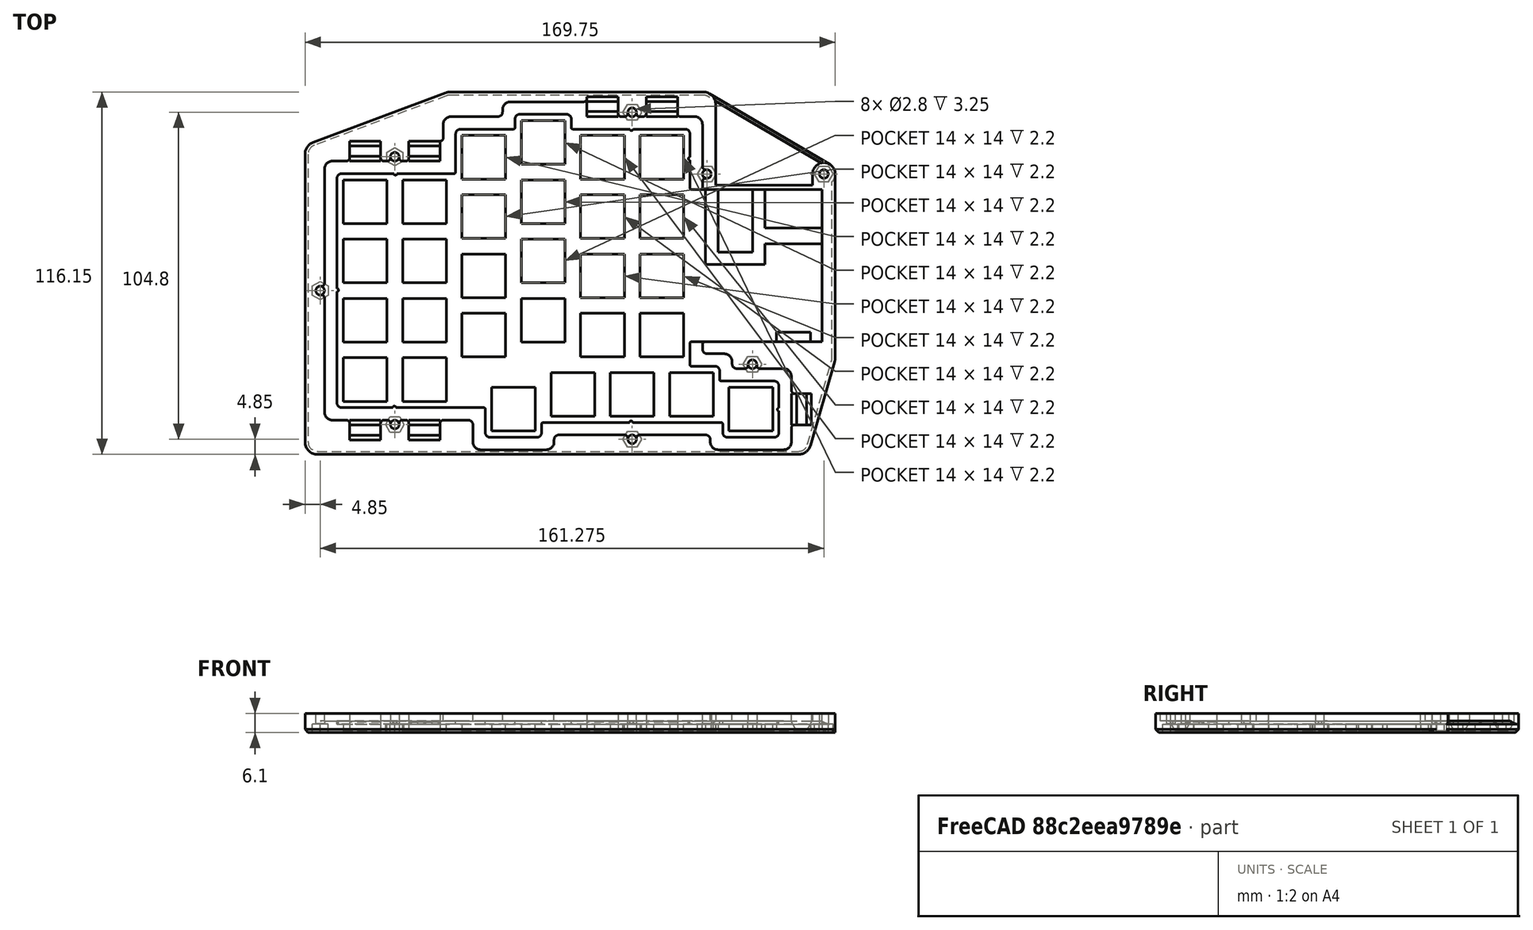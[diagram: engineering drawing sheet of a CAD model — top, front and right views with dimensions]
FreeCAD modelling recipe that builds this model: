
FCSTD DOCUMENT  (FreeCAD 0.21R33771 (Git))
Label: bottom
License: All rights reserved
LicenseURL: http://en.wikipedia.org/wiki/All_rights_reserved
objects: Sketcher::SketchObject×34, PartDesign::Pocket×21, PartDesign::Pad×14, PartDesign::Fillet×11, PartDesign::SubtractivePipe×5, PartDesign::Chamfer×4, PartDesign::Plane×3, Spreadsheet::Sheet×1, PartDesign::Body×1
note: 148 computed .brp shape members not serialized (recipe doc carries the construction recipe); baked Part::Feature solids carry a one-line shape summary decoded from their .brp

FEATURE [Sketcher::SketchObject] Sketch
  FullyConstrained = true
  MapMode = 5
  Support = -> [XY_Plane]
  expr: Constraints[10] = Spreadsheet.sw_wi
  expr: Constraints[11] = Spreadsheet.sw_he
  expr: Constraints[23] = Spreadsheet.pl_spacing
  expr: Constraints[343] = Spreadsheet.pl_spacing
  expr: Constraints[344] = Spreadsheet.pl_spacing
  expr: Constraints[345] = Spreadsheet.pl_spacing
  expr: Constraints[346] = Spreadsheet.pl_spacing
  expr: Constraints[347] = Spreadsheet.pl_spacing
  expr: Constraints[348] = Spreadsheet.pl_sp4
  expr: Constraints[349] = Spreadsheet.pl_sp4
  expr: Constraints[350] = Spreadsheet.pl_sp2
  expr: Constraints[351] = Spreadsheet.pl_spacing
  expr: Constraints[352] = Spreadsheet.pl_spacing
  expr: Constraints[353] = Spreadsheet.pl_spacing
  expr: Constraints[354] = Spreadsheet.pl_spacing
  expr: Constraints[355] = Spreadsheet.pl_spacing
  expr: Constraints[356] = Spreadsheet.pl_spacing
  expr: Constraints[357] = Spreadsheet.pl_spacing
  expr: Constraints[358] = Spreadsheet.pl_spacing
  expr: Constraints[359] = Spreadsheet.pl_spacing
  expr: Constraints[360] = Spreadsheet.pl_spacing
  expr: Constraints[361] = Spreadsheet.pl_spacing
  expr: Constraints[362] = Spreadsheet.pl_spacing
  expr: Constraints[363] = Spreadsheet.pl_spacing
  expr: Constraints[364] = Spreadsheet.pl_spacing
  expr: Constraints[365] = Spreadsheet.pl_spacing
  expr: Constraints[366] = Spreadsheet.pl_spacing
  expr: Constraints[367] = Spreadsheet.pl_spacing
  expr: Constraints[368] = Spreadsheet.pl_spacing
  expr: Constraints[369] = Spreadsheet.pl_spacing
  expr: Constraints[370] = Spreadsheet.pl_spacing
  expr: Constraints[373] = Spreadsheet.pl_sp4
  expr: Constraints[375] = Spreadsheet.pl_sp4
  expr: Constraints[379] = Spreadsheet.pl_case_ext
  expr: Constraints[37] = Spreadsheet.pl_spacing
  expr: Constraints[380] = Spreadsheet.pl_case
  expr: Constraints[381] = Spreadsheet.pl_case
  expr: Constraints[50] = Spreadsheet.pl_spacing
  sketch-geometry (149):
    g0: LineSegment StartX=-7 StartY=7 StartZ=0 EndX=-7 EndY=-7 EndZ=0
    g1: LineSegment StartX=-7 StartY=-7 StartZ=0 EndX=7 EndY=-7 EndZ=0
    g2: LineSegment StartX=7 StartY=-7 StartZ=0 EndX=7 EndY=7 EndZ=0
    g3: LineSegment StartX=7 StartY=7 StartZ=0 EndX=-7 EndY=7 EndZ=0
    g4: GeomPoint X=0 Y=0 Z=0
    g5: LineSegment StartX=-7 StartY=-12 StartZ=0 EndX=-7 EndY=-26 EndZ=0
    g6: LineSegment StartX=-7 StartY=-26 StartZ=0 EndX=7 EndY=-26 EndZ=0
    g7: LineSegment StartX=7 StartY=-26 StartZ=0 EndX=7 EndY=-12 EndZ=0
    g8: LineSegment StartX=7 StartY=-12 StartZ=0 EndX=-7 EndY=-12 EndZ=0
    g9: GeomPoint X=0 Y=-19 Z=0
    g10: LineSegment StartX=-7 StartY=26 StartZ=0 EndX=-7 EndY=12 EndZ=0
    g11: LineSegment StartX=-7 StartY=12 StartZ=0 EndX=7 EndY=12 EndZ=0
    g12: LineSegment StartX=7 StartY=12 StartZ=0 EndX=7 EndY=26 EndZ=0
    g13: LineSegment StartX=7 StartY=26 StartZ=0 EndX=-7 EndY=26 EndZ=0
    g14: GeomPoint X=0 Y=19 Z=0
    g15: LineSegment StartX=-7 StartY=45 StartZ=0 EndX=-7 EndY=31 EndZ=0
    g16: LineSegment StartX=-7 StartY=31 StartZ=0 EndX=7 EndY=31 EndZ=0
    g17: LineSegment StartX=7 StartY=31 StartZ=0 EndX=7 EndY=45 EndZ=0
    g18: LineSegment StartX=7 StartY=45 StartZ=0 EndX=-7 EndY=45 EndZ=0
    g19: GeomPoint X=0 Y=38 Z=0
    g20: LineSegment StartX=-26 StartY=45 StartZ=0 EndX=-26 EndY=31 EndZ=0
    g21: LineSegment StartX=-26 StartY=31 StartZ=0 EndX=-12 EndY=31 EndZ=0
    g22: LineSegment StartX=-12 StartY=31 StartZ=0 EndX=-12 EndY=45 EndZ=0
    g23: LineSegment StartX=-12 StartY=45 StartZ=0 EndX=-26 EndY=45 EndZ=0
    g24: GeomPoint X=-19 Y=38 Z=0
    g25: LineSegment StartX=-26 StartY=26 StartZ=0 EndX=-26 EndY=12 EndZ=0
    g26: LineSegment StartX=-26 StartY=12 StartZ=0 EndX=-12 EndY=12 EndZ=0
    g27: LineSegment StartX=-12 StartY=12 StartZ=0 EndX=-12 EndY=26 EndZ=0
    g28: LineSegment StartX=-12 StartY=26 StartZ=0 EndX=-26 EndY=26 EndZ=0
    g29: GeomPoint X=-19 Y=19 Z=0
    g30: LineSegment StartX=-26 StartY=7 StartZ=0 EndX=-26 EndY=-7 EndZ=0
    g31: LineSegment StartX=-26 StartY=-7 StartZ=0 EndX=-12 EndY=-7 EndZ=0
    g32: LineSegment StartX=-12 StartY=-7 StartZ=0 EndX=-12 EndY=7 EndZ=0
    g33: LineSegment StartX=-12 StartY=7 StartZ=0 EndX=-26 EndY=7 EndZ=0
    g34: GeomPoint X=-19 Y=0 Z=0
    g35: LineSegment StartX=-26 StartY=-12 StartZ=0 EndX=-26 EndY=-26 EndZ=0
    g36: LineSegment StartX=-26 StartY=-26 StartZ=0 EndX=-12 EndY=-26 EndZ=0
    g37: LineSegment StartX=-12 StartY=-26 StartZ=0 EndX=-12 EndY=-12 EndZ=0
    g38: LineSegment StartX=-12 StartY=-12 StartZ=0 EndX=-26 EndY=-12 EndZ=0
    g39: GeomPoint X=-19 Y=-19 Z=0
    g40: LineSegment StartX=-45 StartY=49.75 StartZ=0 EndX=-45 EndY=35.75 EndZ=0
    g41: LineSegment StartX=-45 StartY=35.75 StartZ=0 EndX=-31 EndY=35.75 EndZ=0
    g42: LineSegment StartX=-31 StartY=35.75 StartZ=0 EndX=-31 EndY=49.75 EndZ=0
    g43: LineSegment StartX=-31 StartY=49.75 StartZ=0 EndX=-45 EndY=49.75 EndZ=0
    g44: GeomPoint X=-38 Y=42.75 Z=0
    g45: LineSegment StartX=-45 StartY=30.75 StartZ=0 EndX=-45 EndY=16.75 EndZ=0
    g46: LineSegment StartX=-45 StartY=16.75 StartZ=0 EndX=-31 EndY=16.75 EndZ=0
    g47: LineSegment StartX=-31 StartY=16.75 StartZ=0 EndX=-31 EndY=30.75 EndZ=0
    g48: LineSegment StartX=-31 StartY=30.75 StartZ=0 EndX=-45 EndY=30.75 EndZ=0
    g49: GeomPoint X=-38 Y=23.75 Z=0
    g50: LineSegment StartX=-45 StartY=11.75 StartZ=0 EndX=-45 EndY=-2.25 EndZ=0
    g51: LineSegment StartX=-45 StartY=-2.25 StartZ=0 EndX=-31 EndY=-2.25 EndZ=0
    g52: LineSegment StartX=-31 StartY=-2.25 StartZ=0 EndX=-31 EndY=11.75 EndZ=0
    g53: LineSegment StartX=-31 StartY=11.75 StartZ=0 EndX=-45 EndY=11.75 EndZ=0
    g54: GeomPoint X=-38 Y=4.75 Z=0
    g55: LineSegment StartX=-45 StartY=-7.25 StartZ=0 EndX=-45 EndY=-21.25 EndZ=0
    g56: LineSegment StartX=-45 StartY=-21.25 StartZ=0 EndX=-31 EndY=-21.25 EndZ=0
    g57: LineSegment StartX=-31 StartY=-21.25 StartZ=0 EndX=-31 EndY=-7.25 EndZ=0
    g58: LineSegment StartX=-31 StartY=-7.25 StartZ=0 EndX=-45 EndY=-7.25 EndZ=0
    g59: GeomPoint X=-38 Y=-14.25 Z=0
    g60: LineSegment StartX=-64 StartY=45 StartZ=0 EndX=-64 EndY=31 EndZ=0
    g61: LineSegment StartX=-64 StartY=31 StartZ=0 EndX=-50 EndY=31 EndZ=0
    g62: LineSegment StartX=-50 StartY=31 StartZ=0 EndX=-50 EndY=45 EndZ=0
    g63: LineSegment StartX=-50 StartY=45 StartZ=0 EndX=-64 EndY=45 EndZ=0
    g64: GeomPoint X=-57 Y=38 Z=0
    g65: LineSegment StartX=-64 StartY=26 StartZ=0 EndX=-64 EndY=12 EndZ=0
    g66: LineSegment StartX=-64 StartY=12 StartZ=0 EndX=-50 EndY=12 EndZ=0
    g67: LineSegment StartX=-50 StartY=12 StartZ=0 EndX=-50 EndY=26 EndZ=0
    g68: LineSegment StartX=-50 StartY=26 StartZ=0 EndX=-64 EndY=26 EndZ=0
    g69: GeomPoint X=-57 Y=19 Z=0
    g70: LineSegment StartX=-64 StartY=7 StartZ=0 EndX=-64 EndY=-7 EndZ=0
    g71: LineSegment StartX=-64 StartY=-7 StartZ=0 EndX=-50 EndY=-7 EndZ=0
    g72: LineSegment StartX=-50 StartY=-7 StartZ=0 EndX=-50 EndY=7 EndZ=0
    g73: LineSegment StartX=-50 StartY=7 StartZ=0 EndX=-64 EndY=7 EndZ=0
    g74: GeomPoint X=-57 Y=0 Z=0
    g75: LineSegment StartX=-64 StartY=-12 StartZ=0 EndX=-64 EndY=-26 EndZ=0
    g76: LineSegment StartX=-64 StartY=-26 StartZ=0 EndX=-50 EndY=-26 EndZ=0
    g77: LineSegment StartX=-50 StartY=-26 StartZ=0 EndX=-50 EndY=-12 EndZ=0
    g78: LineSegment StartX=-50 StartY=-12 StartZ=0 EndX=-64 EndY=-12 EndZ=0
    g79: GeomPoint X=-57 Y=-19 Z=0
    g80: LineSegment StartX=-83 StartY=30.75 StartZ=0 EndX=-83 EndY=16.75 EndZ=0
    g81: LineSegment StartX=-83 StartY=16.75 StartZ=0 EndX=-69 EndY=16.75 EndZ=0
    g82: LineSegment StartX=-69 StartY=16.75 StartZ=0 EndX=-69 EndY=30.75 EndZ=0
    g83: LineSegment StartX=-69 StartY=30.75 StartZ=0 EndX=-83 EndY=30.75 EndZ=0
    g84: GeomPoint X=-76 Y=23.75 Z=0
    g85: LineSegment StartX=-102 StartY=30.75 StartZ=0 EndX=-102 EndY=16.75 EndZ=0
    g86: LineSegment StartX=-102 StartY=16.75 StartZ=0 EndX=-88 EndY=16.75 EndZ=0
    g87: LineSegment StartX=-88 StartY=16.75 StartZ=0 EndX=-88 EndY=30.75 EndZ=0
    g88: LineSegment StartX=-88 StartY=30.75 StartZ=0 EndX=-102 EndY=30.75 EndZ=0
    g89: GeomPoint X=-95 Y=23.75 Z=0
    g90: LineSegment StartX=-83 StartY=11.75 StartZ=0 EndX=-83 EndY=-2.25 EndZ=0
    g91: LineSegment StartX=-83 StartY=-2.25 StartZ=0 EndX=-69 EndY=-2.25 EndZ=0
    g92: LineSegment StartX=-69 StartY=-2.25 StartZ=0 EndX=-69 EndY=11.75 EndZ=0
    g93: LineSegment StartX=-69 StartY=11.75 StartZ=0 EndX=-83 EndY=11.75 EndZ=0
    g94: GeomPoint X=-76 Y=4.75 Z=0
    g95: LineSegment StartX=-83 StartY=-7.25 StartZ=0 EndX=-83 EndY=-21.25 EndZ=0
    g96: LineSegment StartX=-83 StartY=-21.25 StartZ=0 EndX=-69 EndY=-21.25 EndZ=0
    g97: LineSegment StartX=-69 StartY=-21.25 StartZ=0 EndX=-69 EndY=-7.25 EndZ=0
    g98: LineSegment StartX=-69 StartY=-7.25 StartZ=0 EndX=-83 EndY=-7.25 EndZ=0
    g99: GeomPoint X=-76 Y=-14.25 Z=0
    g100: LineSegment StartX=-83 StartY=-26.25 StartZ=0 EndX=-83 EndY=-40.25 EndZ=0
    g101: LineSegment StartX=-83 StartY=-40.25 StartZ=0 EndX=-69 EndY=-40.25 EndZ=0
    g102: LineSegment StartX=-69 StartY=-40.25 StartZ=0 EndX=-69 EndY=-26.25 EndZ=0
    g103: LineSegment StartX=-69 StartY=-26.25 StartZ=0 EndX=-83 EndY=-26.25 EndZ=0
    g104: GeomPoint X=-76 Y=-33.25 Z=0
    g105: LineSegment StartX=-102 StartY=11.75 StartZ=0 EndX=-102 EndY=-2.25 EndZ=0
    g106: LineSegment StartX=-102 StartY=-2.25 StartZ=0 EndX=-88 EndY=-2.25 EndZ=0
    g107: LineSegment StartX=-88 StartY=-2.25 StartZ=0 EndX=-88 EndY=11.75 EndZ=0
    g108: LineSegment StartX=-88 StartY=11.75 StartZ=0 EndX=-102 EndY=11.75 EndZ=0
    g109: GeomPoint X=-95 Y=4.75 Z=0
    g110: LineSegment StartX=-102 StartY=-7.25 StartZ=0 EndX=-102 EndY=-21.25 EndZ=0
    g111: LineSegment StartX=-102 StartY=-21.25 StartZ=0 EndX=-88 EndY=-21.25 EndZ=0
    g112: LineSegment StartX=-88 StartY=-21.25 StartZ=0 EndX=-88 EndY=-7.25 EndZ=0
    g113: LineSegment StartX=-88 StartY=-7.25 StartZ=0 EndX=-102 EndY=-7.25 EndZ=0
    g114: GeomPoint X=-95 Y=-14.25 Z=0
    g115: LineSegment StartX=-102 StartY=-26.25 StartZ=0 EndX=-102 EndY=-40.25 EndZ=0
    g116: LineSegment StartX=-102 StartY=-40.25 StartZ=0 EndX=-88 EndY=-40.25 EndZ=0
    g117: LineSegment StartX=-88 StartY=-40.25 StartZ=0 EndX=-88 EndY=-26.25 EndZ=0
    g118: LineSegment StartX=-88 StartY=-26.25 StartZ=0 EndX=-102 EndY=-26.25 EndZ=0
    g119: GeomPoint X=-95 Y=-33.25 Z=0
    g120: LineSegment StartX=-16.5 StartY=-31 StartZ=0 EndX=-16.5 EndY=-45 EndZ=0
    g121: LineSegment StartX=-16.5 StartY=-45 StartZ=0 EndX=-2.5 EndY=-45 EndZ=0
    g122: LineSegment StartX=-2.5 StartY=-45 StartZ=0 EndX=-2.5 EndY=-31 EndZ=0
    g123: LineSegment StartX=-2.5 StartY=-31 StartZ=0 EndX=-16.5 EndY=-31 EndZ=0
    g124: GeomPoint X=-9.5 Y=-38 Z=0
    g125: LineSegment StartX=2.5 StartY=-31 StartZ=0 EndX=2.5 EndY=-45 EndZ=0
    g126: LineSegment StartX=2.5 StartY=-45 StartZ=0 EndX=16.5 EndY=-45 EndZ=0
    g127: LineSegment StartX=16.5 StartY=-45 StartZ=0 EndX=16.5 EndY=-31 EndZ=0
    g128: LineSegment StartX=16.5 StartY=-31 StartZ=0 EndX=2.5 EndY=-31 EndZ=0
    g129: GeomPoint X=9.5 Y=-38 Z=0
    g130: LineSegment StartX=-35.5 StartY=-31 StartZ=0 EndX=-35.5 EndY=-45 EndZ=0
    g131: LineSegment StartX=-35.5 StartY=-45 StartZ=0 EndX=-21.5 EndY=-45 EndZ=0
    g132: LineSegment StartX=-21.5 StartY=-45 StartZ=0 EndX=-21.5 EndY=-31 EndZ=0
    g133: LineSegment StartX=-21.5 StartY=-31 StartZ=0 EndX=-35.5 EndY=-31 EndZ=0
    g134: GeomPoint X=-28.5 Y=-38 Z=0
    g135: LineSegment StartX=21.5 StartY=-35.75 StartZ=0 EndX=21.5 EndY=-49.75 EndZ=0
    g136: LineSegment StartX=21.5 StartY=-49.75 StartZ=0 EndX=35.5 EndY=-49.75 EndZ=0
    g137: LineSegment StartX=35.5 StartY=-49.75 StartZ=0 EndX=35.5 EndY=-35.75 EndZ=0
    g138: LineSegment StartX=35.5 StartY=-35.75 StartZ=0 EndX=21.5 EndY=-35.75 EndZ=0
    g139: GeomPoint X=28.5 Y=-42.75 Z=0
    g140: LineSegment StartX=-54.5 StartY=-35.75 StartZ=0 EndX=-54.5 EndY=-49.75 EndZ=0
    g141: LineSegment StartX=-54.5 StartY=-49.75 StartZ=0 EndX=-40.5 EndY=-49.75 EndZ=0
    g142: LineSegment StartX=-40.5 StartY=-49.75 StartZ=0 EndX=-40.5 EndY=-35.75 EndZ=0
    g143: LineSegment StartX=-40.5 StartY=-35.75 StartZ=0 EndX=-54.5 EndY=-35.75 EndZ=0
    g144: GeomPoint X=-47.5 Y=-42.75 Z=0
    g145: LineSegment StartX=52.75 StartY=-57.25 StartZ=0 EndX=-114.25 EndY=-57.25 EndZ=0
    g146: LineSegment StartX=-114.25 StartY=-57.25 StartZ=0 EndX=-114.25 EndY=57.25 EndZ=0
    g147: LineSegment StartX=-114.25 StartY=57.25 StartZ=0 EndX=52.75 EndY=57.25 EndZ=0
    g148: LineSegment StartX=52.75 StartY=57.25 StartZ=0 EndX=52.75 EndY=-57.25 EndZ=0
  constraints (388):
    c: Coincident(g0,g1)
    c: Coincident(g1,g2)
    c: Coincident(g2,g3)
    c: Coincident(g3,g0)
    c: Horizontal(g1)
    c: Horizontal(g3)
    c: Vertical(g0)
    c: Vertical(g2)
    c: Symmetric(g1,g0,g4)
    c: Coincident(g4,g-1)
    c: DistanceX(g3,g3) = 14
    c: DistanceY(g0,g0) = 14
    c: Coincident(g5,g6)
    c: Coincident(g6,g7)
    c: Coincident(g7,g8)
    c: Coincident(g8,g5)
    c: Horizontal(g6)
    c: Horizontal(g8)
    c: Vertical(g5)
    c: Vertical(g7)
    c: Symmetric(g6,g5,g9)
    c: Equal(g3,g8) = 14.15
    c: Equal(g0,g5) = 14.15
    c: DistanceY(g9,g4) = 19
    c: Vertical(g9,g4)
    c: Coincident(g10,g11)
    c: Coincident(g11,g12)
    c: Coincident(g12,g13)
    c: Coincident(g13,g10)
    c: Horizontal(g11)
    c: Horizontal(g13)
    c: Vertical(g10)
    c: Vertical(g12)
    c: Symmetric(g11,g10,g14)
    c: Equal(g3,g13) = 14.15
    c: Equal(g0,g10) = 14.15
    c: Vertical(g4,g14)
    c: DistanceY(g4,g14) = 19
    c: Coincident(g15,g16)
    c: Coincident(g16,g17)
    c: Coincident(g17,g18)
    c: Coincident(g18,g15)
    c: Horizontal(g16)
    c: Horizontal(g18)
    c: Vertical(g15)
    c: Vertical(g17)
    c: Symmetric(g16,g15,g19)
    c: Equal(g3,g18) = 14.15
    c: Equal(g0,g15) = 14.15
    c: Vertical(g19,g4)
    c: DistanceY(g14,g19) = 19
    c: Coincident(g20,g21)
    c: Coincident(g21,g22)
    c: Coincident(g22,g23)
    c: Coincident(g23,g20)
    c: Horizontal(g21)
    c: Horizontal(g23)
    c: Vertical(g20)
    c: Vertical(g22)
    c: Symmetric(g21,g20,g24)
    c: Equal(g3,g23) = 14.15
    c: Equal(g0,g20) = 14.15
    c: Coincident(g25,g26)
    c: Coincident(g26,g27)
    c: Coincident(g27,g28)
    c: Coincident(g28,g25)
    c: Horizontal(g26)
    c: Horizontal(g28)
    c: Vertical(g25)
    c: Vertical(g27)
    c: Symmetric(g26,g25,g29)
    c: Equal(g3,g28) = 14.15
    c: Equal(g0,g25) = 14.15
    c: Coincident(g30,g31)
    c: Coincident(g31,g32)
    c: Coincident(g32,g33)
    c: Coincident(g33,g30)
    c: Horizontal(g31)
    c: Horizontal(g33)
    c: Vertical(g30)
    c: Vertical(g32)
    c: Symmetric(g31,g30,g34)
    c: Equal(g3,g33) = 14.15
    c: Equal(g0,g30) = 14.15
    c: Coincident(g35,g36)
    c: Coincident(g36,g37)
    c: Coincident(g37,g38)
    c: Coincident(g38,g35)
    c: Horizontal(g36)
    c: Horizontal(g38)
    c: Vertical(g35)
    c: Vertical(g37)
    c: Symmetric(g36,g35,g39)
    c: Equal(g3,g38) = 14.15
    c: Equal(g0,g35) = 14.15
    c: Coincident(g40,g41)
    c: Coincident(g41,g42)
    c: Coincident(g42,g43)
    c: Coincident(g43,g40)
    c: Horizontal(g41)
    c: Horizontal(g43)
    c: Vertical(g40)
    c: Vertical(g42)
    c: Symmetric(g41,g40,g44)
    c: Equal(g3,g43) = 14.15
    c: Equal(g0,g40) = 14.15
    c: Coincident(g45,g46)
    c: Coincident(g46,g47)
    c: Coincident(g47,g48)
    c: Coincident(g48,g45)
    c: Horizontal(g46)
    c: Horizontal(g48)
    c: Vertical(g45)
    c: Vertical(g47)
    c: Symmetric(g46,g45,g49)
    c: Equal(g3,g48) = 14.15
    c: Equal(g0,g45) = 14.15
    c: Coincident(g50,g51)
    c: Coincident(g51,g52)
    c: Coincident(g52,g53)
    c: Coincident(g53,g50)
    c: Horizontal(g51)
    c: Horizontal(g53)
    c: Vertical(g50)
    c: Vertical(g52)
    c: Symmetric(g51,g50,g54)
    c: Equal(g3,g53) = 14.15
    c: Equal(g0,g50) = 14.15
    c: Coincident(g55,g56)
    c: Coincident(g56,g57)
    c: Coincident(g57,g58)
    c: Coincident(g58,g55)
    c: Horizontal(g56)
    c: Horizontal(g58)
    c: Vertical(g55)
    c: Vertical(g57)
    c: Symmetric(g56,g55,g59)
    c: Equal(g3,g58) = 14.15
    c: Equal(g0,g55) = 14.15
    c: Coincident(g60,g61)
    c: Coincident(g61,g62)
    c: Coincident(g62,g63)
    c: Coincident(g63,g60)
    c: Horizontal(g61)
    c: Horizontal(g63)
    c: Vertical(g60)
    c: Vertical(g62)
    c: Symmetric(g61,g60,g64)
    c: Equal(g3,g63) = 14.15
    c: Equal(g0,g60) = 14.15
    c: Coincident(g65,g66)
    c: Coincident(g66,g67)
    c: Coincident(g67,g68)
    c: Coincident(g68,g65)
    c: Horizontal(g66)
    c: Horizontal(g68)
    c: Vertical(g65)
    c: Vertical(g67)
    c: Symmetric(g66,g65,g69)
    c: Equal(g3,g68) = 14.15
    c: Equal(g0,g65) = 14.15
    c: Coincident(g70,g71)
    c: Coincident(g71,g72)
    c: Coincident(g72,g73)
    c: Coincident(g73,g70)
    c: Horizontal(g71)
    c: Horizontal(g73)
    c: Vertical(g70)
    c: Vertical(g72)
    c: Symmetric(g71,g70,g74)
    c: Equal(g3,g73) = 14.15
    c: Equal(g0,g70) = 14.15
    c: Coincident(g75,g76)
    c: Coincident(g76,g77)
    c: Coincident(g77,g78)
    c: Coincident(g78,g75)
    c: Horizontal(g76)
    c: Horizontal(g78)
    c: Vertical(g75)
    c: Vertical(g77)
    c: Symmetric(g76,g75,g79)
    c: Equal(g3,g78) = 14.15
    c: Equal(g0,g75) = 14.15
    c: Coincident(g80,g81)
    c: Coincident(g81,g82)
    c: Coincident(g82,g83)
    c: Coincident(g83,g80)
    c: Horizontal(g81)
    c: Horizontal(g83)
    c: Vertical(g80)
    c: Vertical(g82)
    c: Symmetric(g81,g80,g84)
    c: Equal(g3,g83) = 14.15
    c: Equal(g0,g80) = 14.15
    c: Coincident(g85,g86)
    c: Coincident(g86,g87)
    c: Coincident(g87,g88)
    c: Coincident(g88,g85)
    c: Horizontal(g86)
    c: Horizontal(g88)
    c: Vertical(g85)
    c: Vertical(g87)
    c: Symmetric(g86,g85,g89)
    c: Equal(g3,g88) = 14.15
    c: Equal(g0,g85) = 14.15
    c: Coincident(g90,g91)
    c: Coincident(g91,g92)
    c: Coincident(g92,g93)
    c: Coincident(g93,g90)
    c: Horizontal(g91)
    c: Horizontal(g93)
    c: Vertical(g90)
    c: Vertical(g92)
    c: Symmetric(g91,g90,g94)
    c: Equal(g3,g93) = 14.15
    c: Equal(g0,g90) = 14.15
    c: Coincident(g95,g96)
    c: Coincident(g96,g97)
    c: Coincident(g97,g98)
    c: Coincident(g98,g95)
    c: Horizontal(g96)
    c: Horizontal(g98)
    c: Vertical(g95)
    c: Vertical(g97)
    c: Symmetric(g96,g95,g99)
    c: Equal(g3,g98) = 14.15
    c: Equal(g0,g95) = 14.15
    c: Coincident(g100,g101)
    c: Coincident(g101,g102)
    c: Coincident(g102,g103)
    c: Coincident(g103,g100)
    c: Horizontal(g101)
    c: Horizontal(g103)
    c: Vertical(g100)
    c: Vertical(g102)
    c: Symmetric(g101,g100,g104)
    c: Equal(g3,g103) = 14.15
    c: Equal(g0,g100) = 14.15
    c: Coincident(g105,g106)
    c: Coincident(g106,g107)
    c: Coincident(g107,g108)
    c: Coincident(g108,g105)
    c: Horizontal(g106)
    c: Horizontal(g108)
    c: Vertical(g105)
    c: Vertical(g107)
    c: Symmetric(g106,g105,g109)
    c: Equal(g3,g108) = 14.15
    c: Equal(g0,g105) = 14.15
    c: Coincident(g110,g111)
    c: Coincident(g111,g112)
    c: Coincident(g112,g113)
    c: Coincident(g113,g110)
    c: Horizontal(g111)
    c: Horizontal(g113)
    c: Vertical(g110)
    c: Vertical(g112)
    c: Symmetric(g111,g110,g114)
    c: Equal(g3,g113) = 14.15
    c: Equal(g0,g110) = 14.15
    c: Coincident(g115,g116)
    c: Coincident(g116,g117)
    c: Coincident(g117,g118)
    c: Coincident(g118,g115)
    c: Horizontal(g116)
    c: Horizontal(g118)
    c: Vertical(g115)
    c: Vertical(g117)
    c: Symmetric(g116,g115,g119)
    c: Equal(g3,g118) = 14.15
    c: Equal(g0,g115) = 14.15
    c: Coincident(g120,g121)
    c: Coincident(g121,g122)
    c: Coincident(g122,g123)
    c: Coincident(g123,g120)
    c: Horizontal(g121)
    c: Horizontal(g123)
    c: Vertical(g120)
    c: Vertical(g122)
    c: Symmetric(g121,g120,g124)
    c: Equal(g3,g123) = 14.15
    c: Equal(g0,g120) = 14.15
    c: Coincident(g125,g126)
    c: Coincident(g126,g127)
    c: Coincident(g127,g128)
    c: Coincident(g128,g125)
    c: Horizontal(g126)
    c: Horizontal(g128)
    c: Vertical(g125)
    c: Vertical(g127)
    c: Symmetric(g126,g125,g129)
    c: Equal(g3,g128) = 14.15
    c: Equal(g0,g125) = 14.15
    c: Coincident(g130,g131)
    c: Coincident(g131,g132)
    c: Coincident(g132,g133)
    c: Coincident(g133,g130)
    c: Horizontal(g131)
    c: Horizontal(g133)
    c: Vertical(g130)
    c: Vertical(g132)
    c: Symmetric(g131,g130,g134)
    c: Equal(g3,g133) = 14.15
    c: Equal(g0,g130) = 14.15
    c: Coincident(g135,g136)
    c: Coincident(g136,g137)
    c: Coincident(g137,g138)
    c: Coincident(g138,g135)
    c: Horizontal(g136)
    c: Horizontal(g138)
    c: Vertical(g135)
    c: Vertical(g137)
    c: Symmetric(g136,g135,g139)
    c: Equal(g3,g138) = 14.15
    c: Equal(g0,g135) = 14.15
    c: Coincident(g140,g141)
    c: Coincident(g141,g142)
    c: Coincident(g142,g143)
    c: Coincident(g143,g140)
    c: Horizontal(g141)
    c: Horizontal(g143)
    c: Vertical(g140)
    c: Vertical(g142)
    c: Symmetric(g141,g140,g144)
    c: Equal(g3,g143) = 14.15
    c: Equal(g0,g140) = 14.15
    c: Vertical(g39,g34)
    c: Vertical(g34,g29)
    c: Vertical(g29,g24)
    c: Vertical(g59,g54)
    c: Vertical(g54,g49)
    c: Vertical(g49,g44)
    c: Vertical(g79,g74)
    c: Vertical(g74,g69)
    c: Vertical(g69,g64)
    c: Vertical(g104,g99)
    c: Vertical(g99,g94)
    c: Vertical(g94,g84)
    c: Vertical(g119,g114)
    c: Vertical(g114,g109)
    c: Vertical(g109,g89)
    c: Horizontal(g134,g124)
    c: Horizontal(g124,g129)
    c: DistanceY(g129,g9) = 19
    c: DistanceX(g129,g139) = 19
    c: DistanceX(g124,g129) = 19
    c: DistanceX(g134,g124) = 19
    c: DistanceX(g144,g134) = 19
    c: DistanceY(g139,g129) = 4.75
    c: DistanceY(g144,g134) = 4.75
    c: DistanceX(g9,g129) = 9.5
    c: DistanceY(g39,g34) = 19
    c: DistanceY(g34,g29) = 19
    c: DistanceY(g29,g24) = 19
    c: DistanceY(g59,g54) = 19
    c: DistanceY(g54,g49) = 19
    c: DistanceY(g49,g44) = 19
    c: DistanceY(g79,g74) = 19
    c: DistanceY(g74,g69) = 19
    c: DistanceY(g69,g64) = 19
    c: DistanceY(g104,g99) = 19
    c: DistanceY(g99,g94) = 19
    c: DistanceY(g94,g84) = 19
    c: DistanceY(g119,g114) = 19
    c: DistanceY(g114,g109) = 19
    c: DistanceY(g109,g89) = 19
    c: DistanceX(g34,g4) = 19
    c: DistanceX(g54,g34) = 19
    c: DistanceX(g74,g54) = 19
    c: DistanceX(g99,g74) = 19
    c: DistanceX(g114,g99) = 19
    c: Horizontal(g34,g4)
    c: Horizontal(g74,g34)
    c: DistanceY(g34,g54) = 4.75
    c: Horizontal(g114,g99)
    c: DistanceY(g74,g94) = 4.75
    c: Horizontal(g145)
    c: Vertical(g146)
    c: Horizontal(g147)
    c: DistanceX(g146,g89) = 19.25
    c: DistanceY(g44,g147) = 14.5
    c: DistanceY(g145,g139) = 14.5
    c: Coincident(g146,g145)
    c: Coincident(g147,g146)
    c: Coincident(g148,g147)
    c: Vertical(g148)
    c: Coincident(g148,g145)
    c: DistanceX(g4,g147) = 52.75
FEATURE [Spreadsheet::Sheet] Spreadsheet
  cells = B2='Switch Opening; F2='Thickness; H2='Total; B3='width; C3(sw_wi)=14; F3='bottom; G3=1; H3(th_bottom)==G3; B4='height; C4(sw_he)=14; F4='switch; G4=2; H4(th_switch)==G4 + H3; F5='pcb; G5=1; H5(th_pcb)==G5 + H4; B11='Plate; G11='Hole pattern; B12='spacing; C12(pl_spacing)=19; G12='edge distance; H12(hole_ext)=4.85; B13='spacing/2; C13(pl_sp2)==C12 / 2; G13='internal edge; H13(hole_int)=1.4; B14='spcing/4; C14(pl_sp4)==C12 / 4; G14='dia; H14(hole_dia)=2.8; B15='PCB edge offset; C15==17 / 2 + 0.5; D15(pl_edge)==C15; G15='hex; H15(hexnut)=5.1; B16='Case edge offset; C16==25 / 2 + 2; D16(pl_case)==C16; E16(pl_case_ext)==D16 + C14; B17='Plate edge offset; C17==25 / 2 + 0.5; D17(pl_plate)==C17
FEATURE [Sketcher::SketchObject] Sketch001
  AttachmentOffset = pos=(0,0,1) rot=(0,0,1;0rad)
  FullyConstrained = true
  MapMode = 5
  Placement = pos=(0,0,1) rot=(0,0,1;0rad)
  Support = -> [XY_Plane]
  expr: .AttachmentOffset.Base.z = Spreadsheet.th_bottom
  expr: Constraints[10] = Spreadsheet.sw_wi
  expr: Constraints[11] = Spreadsheet.sw_he
  expr: Constraints[23] = Spreadsheet.pl_spacing
  expr: Constraints[343] = Spreadsheet.pl_spacing
  expr: Constraints[344] = Spreadsheet.pl_spacing
  expr: Constraints[345] = Spreadsheet.pl_spacing
  expr: Constraints[346] = Spreadsheet.pl_spacing
  expr: Constraints[347] = Spreadsheet.pl_spacing
  expr: Constraints[348] = Spreadsheet.pl_sp4
  expr: Constraints[349] = Spreadsheet.pl_sp4
  expr: Constraints[350] = Spreadsheet.pl_sp2
  expr: Constraints[351] = Spreadsheet.pl_spacing
  expr: Constraints[352] = Spreadsheet.pl_spacing
  expr: Constraints[353] = Spreadsheet.pl_spacing
  expr: Constraints[354] = Spreadsheet.pl_spacing
  expr: Constraints[355] = Spreadsheet.pl_spacing
  expr: Constraints[356] = Spreadsheet.pl_spacing
  expr: Constraints[357] = Spreadsheet.pl_spacing
  expr: Constraints[358] = Spreadsheet.pl_spacing
  expr: Constraints[359] = Spreadsheet.pl_spacing
  expr: Constraints[360] = Spreadsheet.pl_spacing
  expr: Constraints[361] = Spreadsheet.pl_spacing
  expr: Constraints[362] = Spreadsheet.pl_spacing
  expr: Constraints[363] = Spreadsheet.pl_spacing
  expr: Constraints[364] = Spreadsheet.pl_spacing
  expr: Constraints[365] = Spreadsheet.pl_spacing
  expr: Constraints[366] = Spreadsheet.pl_spacing
  expr: Constraints[367] = Spreadsheet.pl_spacing
  expr: Constraints[368] = Spreadsheet.pl_spacing
  expr: Constraints[369] = Spreadsheet.pl_spacing
  expr: Constraints[370] = Spreadsheet.pl_spacing
  expr: Constraints[373] = Spreadsheet.pl_sp4
  expr: Constraints[375] = Spreadsheet.pl_sp4
  expr: Constraints[37] = Spreadsheet.pl_spacing
  expr: Constraints[50] = Spreadsheet.pl_spacing
  sketch-geometry (145):
    g0: LineSegment StartX=-7 StartY=7 StartZ=0 EndX=-7 EndY=-7 EndZ=0
    g1: LineSegment StartX=-7 StartY=-7 StartZ=0 EndX=7 EndY=-7 EndZ=0
    g2: LineSegment StartX=7 StartY=-7 StartZ=0 EndX=7 EndY=7 EndZ=0
    g3: LineSegment StartX=7 StartY=7 StartZ=0 EndX=-7 EndY=7 EndZ=0
    g4: GeomPoint X=0 Y=0 Z=0
    g5: LineSegment StartX=-7 StartY=-12 StartZ=0 EndX=-7 EndY=-26 EndZ=0
    g6: LineSegment StartX=-7 StartY=-26 StartZ=0 EndX=7 EndY=-26 EndZ=0
    g7: LineSegment StartX=7 StartY=-26 StartZ=0 EndX=7 EndY=-12 EndZ=0
    g8: LineSegment StartX=7 StartY=-12 StartZ=0 EndX=-7 EndY=-12 EndZ=0
    g9: GeomPoint X=0 Y=-19 Z=0
    g10: LineSegment StartX=-7 StartY=26 StartZ=0 EndX=-7 EndY=12 EndZ=0
    g11: LineSegment StartX=-7 StartY=12 StartZ=0 EndX=7 EndY=12 EndZ=0
    g12: LineSegment StartX=7 StartY=12 StartZ=0 EndX=7 EndY=26 EndZ=0
    g13: LineSegment StartX=7 StartY=26 StartZ=0 EndX=-7 EndY=26 EndZ=0
    g14: GeomPoint X=0 Y=19 Z=0
    g15: LineSegment StartX=-7 StartY=45 StartZ=0 EndX=-7 EndY=31 EndZ=0
    g16: LineSegment StartX=-7 StartY=31 StartZ=0 EndX=7 EndY=31 EndZ=0
    g17: LineSegment StartX=7 StartY=31 StartZ=0 EndX=7 EndY=45 EndZ=0
    g18: LineSegment StartX=7 StartY=45 StartZ=0 EndX=-7 EndY=45 EndZ=0
    g19: GeomPoint X=0 Y=38 Z=0
    g20: LineSegment StartX=-26 StartY=45 StartZ=0 EndX=-26 EndY=31 EndZ=0
    g21: LineSegment StartX=-26 StartY=31 StartZ=0 EndX=-12 EndY=31 EndZ=0
    g22: LineSegment StartX=-12 StartY=31 StartZ=0 EndX=-12 EndY=45 EndZ=0
    g23: LineSegment StartX=-12 StartY=45 StartZ=0 EndX=-26 EndY=45 EndZ=0
    g24: GeomPoint X=-19 Y=38 Z=0
    g25: LineSegment StartX=-26 StartY=26 StartZ=0 EndX=-26 EndY=12 EndZ=0
    g26: LineSegment StartX=-26 StartY=12 StartZ=0 EndX=-12 EndY=12 EndZ=0
    g27: LineSegment StartX=-12 StartY=12 StartZ=0 EndX=-12 EndY=26 EndZ=0
    g28: LineSegment StartX=-12 StartY=26 StartZ=0 EndX=-26 EndY=26 EndZ=0
    g29: GeomPoint X=-19 Y=19 Z=0
    g30: LineSegment StartX=-26 StartY=7 StartZ=0 EndX=-26 EndY=-7 EndZ=0
    g31: LineSegment StartX=-26 StartY=-7 StartZ=0 EndX=-12 EndY=-7 EndZ=0
    g32: LineSegment StartX=-12 StartY=-7 StartZ=0 EndX=-12 EndY=7 EndZ=0
    g33: LineSegment StartX=-12 StartY=7 StartZ=0 EndX=-26 EndY=7 EndZ=0
    g34: GeomPoint X=-19 Y=0 Z=0
    g35: LineSegment StartX=-26 StartY=-12 StartZ=0 EndX=-26 EndY=-26 EndZ=0
    g36: LineSegment StartX=-26 StartY=-26 StartZ=0 EndX=-12 EndY=-26 EndZ=0
    g37: LineSegment StartX=-12 StartY=-26 StartZ=0 EndX=-12 EndY=-12 EndZ=0
    g38: LineSegment StartX=-12 StartY=-12 StartZ=0 EndX=-26 EndY=-12 EndZ=0
    g39: GeomPoint X=-19 Y=-19 Z=0
    g40: LineSegment StartX=-45 StartY=49.75 StartZ=0 EndX=-45 EndY=35.75 EndZ=0
    g41: LineSegment StartX=-45 StartY=35.75 StartZ=0 EndX=-31 EndY=35.75 EndZ=0
    g42: LineSegment StartX=-31 StartY=35.75 StartZ=0 EndX=-31 EndY=49.75 EndZ=0
    g43: LineSegment StartX=-31 StartY=49.75 StartZ=0 EndX=-45 EndY=49.75 EndZ=0
    g44: GeomPoint X=-38 Y=42.75 Z=0
    g45: LineSegment StartX=-45 StartY=30.75 StartZ=0 EndX=-45 EndY=16.75 EndZ=0
    g46: LineSegment StartX=-45 StartY=16.75 StartZ=0 EndX=-31 EndY=16.75 EndZ=0
    g47: LineSegment StartX=-31 StartY=16.75 StartZ=0 EndX=-31 EndY=30.75 EndZ=0
    g48: LineSegment StartX=-31 StartY=30.75 StartZ=0 EndX=-45 EndY=30.75 EndZ=0
    g49: GeomPoint X=-38 Y=23.75 Z=0
    g50: LineSegment StartX=-45 StartY=11.75 StartZ=0 EndX=-45 EndY=-2.25 EndZ=0
    g51: LineSegment StartX=-45 StartY=-2.25 StartZ=0 EndX=-31 EndY=-2.25 EndZ=0
    g52: LineSegment StartX=-31 StartY=-2.25 StartZ=0 EndX=-31 EndY=11.75 EndZ=0
    g53: LineSegment StartX=-31 StartY=11.75 StartZ=0 EndX=-45 EndY=11.75 EndZ=0
    g54: GeomPoint X=-38 Y=4.75 Z=0
    g55: LineSegment StartX=-45 StartY=-7.25 StartZ=0 EndX=-45 EndY=-21.25 EndZ=0
    g56: LineSegment StartX=-45 StartY=-21.25 StartZ=0 EndX=-31 EndY=-21.25 EndZ=0
    g57: LineSegment StartX=-31 StartY=-21.25 StartZ=0 EndX=-31 EndY=-7.25 EndZ=0
    g58: LineSegment StartX=-31 StartY=-7.25 StartZ=0 EndX=-45 EndY=-7.25 EndZ=0
    g59: GeomPoint X=-38 Y=-14.25 Z=0
    g60: LineSegment StartX=-64 StartY=45 StartZ=0 EndX=-64 EndY=31 EndZ=0
    g61: LineSegment StartX=-64 StartY=31 StartZ=0 EndX=-50 EndY=31 EndZ=0
    g62: LineSegment StartX=-50 StartY=31 StartZ=0 EndX=-50 EndY=45 EndZ=0
    g63: LineSegment StartX=-50 StartY=45 StartZ=0 EndX=-64 EndY=45 EndZ=0
    g64: GeomPoint X=-57 Y=38 Z=0
    g65: LineSegment StartX=-64 StartY=26 StartZ=0 EndX=-64 EndY=12 EndZ=0
    g66: LineSegment StartX=-64 StartY=12 StartZ=0 EndX=-50 EndY=12 EndZ=0
    g67: LineSegment StartX=-50 StartY=12 StartZ=0 EndX=-50 EndY=26 EndZ=0
    g68: LineSegment StartX=-50 StartY=26 StartZ=0 EndX=-64 EndY=26 EndZ=0
    g69: GeomPoint X=-57 Y=19 Z=0
    g70: LineSegment StartX=-64 StartY=7 StartZ=0 EndX=-64 EndY=-7 EndZ=0
    g71: LineSegment StartX=-64 StartY=-7 StartZ=0 EndX=-50 EndY=-7 EndZ=0
    g72: LineSegment StartX=-50 StartY=-7 StartZ=0 EndX=-50 EndY=7 EndZ=0
    g73: LineSegment StartX=-50 StartY=7 StartZ=0 EndX=-64 EndY=7 EndZ=0
    g74: GeomPoint X=-57 Y=0 Z=0
    g75: LineSegment StartX=-64 StartY=-12 StartZ=0 EndX=-64 EndY=-26 EndZ=0
    g76: LineSegment StartX=-64 StartY=-26 StartZ=0 EndX=-50 EndY=-26 EndZ=0
    g77: LineSegment StartX=-50 StartY=-26 StartZ=0 EndX=-50 EndY=-12 EndZ=0
    g78: LineSegment StartX=-50 StartY=-12 StartZ=0 EndX=-64 EndY=-12 EndZ=0
    g79: GeomPoint X=-57 Y=-19 Z=0
    g80: LineSegment StartX=-83 StartY=30.75 StartZ=0 EndX=-83 EndY=16.75 EndZ=0
    g81: LineSegment StartX=-83 StartY=16.75 StartZ=0 EndX=-69 EndY=16.75 EndZ=0
    g82: LineSegment StartX=-69 StartY=16.75 StartZ=0 EndX=-69 EndY=30.75 EndZ=0
    g83: LineSegment StartX=-69 StartY=30.75 StartZ=0 EndX=-83 EndY=30.75 EndZ=0
    g84: GeomPoint X=-76 Y=23.75 Z=0
    g85: LineSegment StartX=-102 StartY=30.75 StartZ=0 EndX=-102 EndY=16.75 EndZ=0
    g86: LineSegment StartX=-102 StartY=16.75 StartZ=0 EndX=-88 EndY=16.75 EndZ=0
    g87: LineSegment StartX=-88 StartY=16.75 StartZ=0 EndX=-88 EndY=30.75 EndZ=0
    g88: LineSegment StartX=-88 StartY=30.75 StartZ=0 EndX=-102 EndY=30.75 EndZ=0
    g89: GeomPoint X=-95 Y=23.75 Z=0
    g90: LineSegment StartX=-83 StartY=11.75 StartZ=0 EndX=-83 EndY=-2.25 EndZ=0
    g91: LineSegment StartX=-83 StartY=-2.25 StartZ=0 EndX=-69 EndY=-2.25 EndZ=0
    g92: LineSegment StartX=-69 StartY=-2.25 StartZ=0 EndX=-69 EndY=11.75 EndZ=0
    g93: LineSegment StartX=-69 StartY=11.75 StartZ=0 EndX=-83 EndY=11.75 EndZ=0
    g94: GeomPoint X=-76 Y=4.75 Z=0
    g95: LineSegment StartX=-83 StartY=-7.25 StartZ=0 EndX=-83 EndY=-21.25 EndZ=0
    g96: LineSegment StartX=-83 StartY=-21.25 StartZ=0 EndX=-69 EndY=-21.25 EndZ=0
    g97: LineSegment StartX=-69 StartY=-21.25 StartZ=0 EndX=-69 EndY=-7.25 EndZ=0
    g98: LineSegment StartX=-69 StartY=-7.25 StartZ=0 EndX=-83 EndY=-7.25 EndZ=0
    g99: GeomPoint X=-76 Y=-14.25 Z=0
    g100: LineSegment StartX=-83 StartY=-26.25 StartZ=0 EndX=-83 EndY=-40.25 EndZ=0
    g101: LineSegment StartX=-83 StartY=-40.25 StartZ=0 EndX=-69 EndY=-40.25 EndZ=0
    g102: LineSegment StartX=-69 StartY=-40.25 StartZ=0 EndX=-69 EndY=-26.25 EndZ=0
    g103: LineSegment StartX=-69 StartY=-26.25 StartZ=0 EndX=-83 EndY=-26.25 EndZ=0
    g104: GeomPoint X=-76 Y=-33.25 Z=0
    g105: LineSegment StartX=-102 StartY=11.75 StartZ=0 EndX=-102 EndY=-2.25 EndZ=0
    g106: LineSegment StartX=-102 StartY=-2.25 StartZ=0 EndX=-88 EndY=-2.25 EndZ=0
    g107: LineSegment StartX=-88 StartY=-2.25 StartZ=0 EndX=-88 EndY=11.75 EndZ=0
    g108: LineSegment StartX=-88 StartY=11.75 StartZ=0 EndX=-102 EndY=11.75 EndZ=0
    g109: GeomPoint X=-95 Y=4.75 Z=0
    g110: LineSegment StartX=-102 StartY=-7.25 StartZ=0 EndX=-102 EndY=-21.25 EndZ=0
    g111: LineSegment StartX=-102 StartY=-21.25 StartZ=0 EndX=-88 EndY=-21.25 EndZ=0
    g112: LineSegment StartX=-88 StartY=-21.25 StartZ=0 EndX=-88 EndY=-7.25 EndZ=0
    g113: LineSegment StartX=-88 StartY=-7.25 StartZ=0 EndX=-102 EndY=-7.25 EndZ=0
    g114: GeomPoint X=-95 Y=-14.25 Z=0
    g115: LineSegment StartX=-102 StartY=-26.25 StartZ=0 EndX=-102 EndY=-40.25 EndZ=0
    g116: LineSegment StartX=-102 StartY=-40.25 StartZ=0 EndX=-88 EndY=-40.25 EndZ=0
    g117: LineSegment StartX=-88 StartY=-40.25 StartZ=0 EndX=-88 EndY=-26.25 EndZ=0
    g118: LineSegment StartX=-88 StartY=-26.25 StartZ=0 EndX=-102 EndY=-26.25 EndZ=0
    g119: GeomPoint X=-95 Y=-33.25 Z=0
    g120: LineSegment StartX=-16.5 StartY=-31 StartZ=0 EndX=-16.5 EndY=-45 EndZ=0
    g121: LineSegment StartX=-16.5 StartY=-45 StartZ=0 EndX=-2.5 EndY=-45 EndZ=0
    g122: LineSegment StartX=-2.5 StartY=-45 StartZ=0 EndX=-2.5 EndY=-31 EndZ=0
    g123: LineSegment StartX=-2.5 StartY=-31 StartZ=0 EndX=-16.5 EndY=-31 EndZ=0
    g124: GeomPoint X=-9.5 Y=-38 Z=0
    g125: LineSegment StartX=2.5 StartY=-31 StartZ=0 EndX=2.5 EndY=-45 EndZ=0
    g126: LineSegment StartX=2.5 StartY=-45 StartZ=0 EndX=16.5 EndY=-45 EndZ=0
    g127: LineSegment StartX=16.5 StartY=-45 StartZ=0 EndX=16.5 EndY=-31 EndZ=0
    g128: LineSegment StartX=16.5 StartY=-31 StartZ=0 EndX=2.5 EndY=-31 EndZ=0
    g129: GeomPoint X=9.5 Y=-38 Z=0
    g130: LineSegment StartX=-35.5 StartY=-31 StartZ=0 EndX=-35.5 EndY=-45 EndZ=0
    g131: LineSegment StartX=-35.5 StartY=-45 StartZ=0 EndX=-21.5 EndY=-45 EndZ=0
    g132: LineSegment StartX=-21.5 StartY=-45 StartZ=0 EndX=-21.5 EndY=-31 EndZ=0
    g133: LineSegment StartX=-21.5 StartY=-31 StartZ=0 EndX=-35.5 EndY=-31 EndZ=0
    g134: GeomPoint X=-28.5 Y=-38 Z=0
    g135: LineSegment StartX=21.5 StartY=-35.75 StartZ=0 EndX=21.5 EndY=-49.75 EndZ=0
    g136: LineSegment StartX=21.5 StartY=-49.75 StartZ=0 EndX=35.5 EndY=-49.75 EndZ=0
    g137: LineSegment StartX=35.5 StartY=-49.75 StartZ=0 EndX=35.5 EndY=-35.75 EndZ=0
    g138: LineSegment StartX=35.5 StartY=-35.75 StartZ=0 EndX=21.5 EndY=-35.75 EndZ=0
    g139: GeomPoint X=28.5 Y=-42.75 Z=0
    g140: LineSegment StartX=-54.5 StartY=-35.75 StartZ=0 EndX=-54.5 EndY=-49.75 EndZ=0
    g141: LineSegment StartX=-54.5 StartY=-49.75 StartZ=0 EndX=-40.5 EndY=-49.75 EndZ=0
    g142: LineSegment StartX=-40.5 StartY=-49.75 StartZ=0 EndX=-40.5 EndY=-35.75 EndZ=0
    g143: LineSegment StartX=-40.5 StartY=-35.75 StartZ=0 EndX=-54.5 EndY=-35.75 EndZ=0
    g144: GeomPoint X=-47.5 Y=-42.75 Z=0
  constraints (376):
    c: Coincident(g0,g1)
    c: Coincident(g1,g2)
    c: Coincident(g2,g3)
    c: Coincident(g3,g0)
    c: Horizontal(g1)
    c: Horizontal(g3)
    c: Vertical(g0)
    c: Vertical(g2)
    c: Symmetric(g1,g0,g4)
    c: Coincident(g4,g-1)
    c: DistanceX(g3,g3) = 14
    c: DistanceY(g0,g0) = 14
    c: Coincident(g5,g6)
    c: Coincident(g6,g7)
    c: Coincident(g7,g8)
    c: Coincident(g8,g5)
    c: Horizontal(g6)
    c: Horizontal(g8)
    c: Vertical(g5)
    c: Vertical(g7)
    c: Symmetric(g6,g5,g9)
    c: Equal(g3,g8) = 14.15
    c: Equal(g0,g5) = 14.15
    c: DistanceY(g9,g4) = 19
    c: Vertical(g9,g4)
    c: Coincident(g10,g11)
    c: Coincident(g11,g12)
    c: Coincident(g12,g13)
    c: Coincident(g13,g10)
    c: Horizontal(g11)
    c: Horizontal(g13)
    c: Vertical(g10)
    c: Vertical(g12)
    c: Symmetric(g11,g10,g14)
    c: Equal(g3,g13) = 14.15
    c: Equal(g0,g10) = 14.15
    c: Vertical(g4,g14)
    c: DistanceY(g4,g14) = 19
    c: Coincident(g15,g16)
    c: Coincident(g16,g17)
    c: Coincident(g17,g18)
    c: Coincident(g18,g15)
    c: Horizontal(g16)
    c: Horizontal(g18)
    c: Vertical(g15)
    c: Vertical(g17)
    c: Symmetric(g16,g15,g19)
    c: Equal(g3,g18) = 14.15
    c: Equal(g0,g15) = 14.15
    c: Vertical(g19,g4)
    c: DistanceY(g14,g19) = 19
    c: Coincident(g20,g21)
    c: Coincident(g21,g22)
    c: Coincident(g22,g23)
    c: Coincident(g23,g20)
    c: Horizontal(g21)
    c: Horizontal(g23)
    c: Vertical(g20)
    c: Vertical(g22)
    c: Symmetric(g21,g20,g24)
    c: Equal(g3,g23) = 14.15
    c: Equal(g0,g20) = 14.15
    c: Coincident(g25,g26)
    c: Coincident(g26,g27)
    c: Coincident(g27,g28)
    c: Coincident(g28,g25)
    c: Horizontal(g26)
    c: Horizontal(g28)
    c: Vertical(g25)
    c: Vertical(g27)
    c: Symmetric(g26,g25,g29)
    c: Equal(g3,g28) = 14.15
    c: Equal(g0,g25) = 14.15
    c: Coincident(g30,g31)
    c: Coincident(g31,g32)
    c: Coincident(g32,g33)
    c: Coincident(g33,g30)
    c: Horizontal(g31)
    c: Horizontal(g33)
    c: Vertical(g30)
    c: Vertical(g32)
    c: Symmetric(g31,g30,g34)
    c: Equal(g3,g33) = 14.15
    c: Equal(g0,g30) = 14.15
    c: Coincident(g35,g36)
    c: Coincident(g36,g37)
    c: Coincident(g37,g38)
    c: Coincident(g38,g35)
    c: Horizontal(g36)
    c: Horizontal(g38)
    c: Vertical(g35)
    c: Vertical(g37)
    c: Symmetric(g36,g35,g39)
    c: Equal(g3,g38) = 14.15
    c: Equal(g0,g35) = 14.15
    c: Coincident(g40,g41)
    c: Coincident(g41,g42)
    c: Coincident(g42,g43)
    c: Coincident(g43,g40)
    c: Horizontal(g41)
    c: Horizontal(g43)
    c: Vertical(g40)
    c: Vertical(g42)
    c: Symmetric(g41,g40,g44)
    c: Equal(g3,g43) = 14.15
    c: Equal(g0,g40) = 14.15
    c: Coincident(g45,g46)
    c: Coincident(g46,g47)
    c: Coincident(g47,g48)
    c: Coincident(g48,g45)
    c: Horizontal(g46)
    c: Horizontal(g48)
    c: Vertical(g45)
    c: Vertical(g47)
    c: Symmetric(g46,g45,g49)
    c: Equal(g3,g48) = 14.15
    c: Equal(g0,g45) = 14.15
    c: Coincident(g50,g51)
    c: Coincident(g51,g52)
    c: Coincident(g52,g53)
    c: Coincident(g53,g50)
    c: Horizontal(g51)
    c: Horizontal(g53)
    c: Vertical(g50)
    c: Vertical(g52)
    c: Symmetric(g51,g50,g54)
    c: Equal(g3,g53) = 14.15
    c: Equal(g0,g50) = 14.15
    c: Coincident(g55,g56)
    c: Coincident(g56,g57)
    c: Coincident(g57,g58)
    c: Coincident(g58,g55)
    c: Horizontal(g56)
    c: Horizontal(g58)
    c: Vertical(g55)
    c: Vertical(g57)
    c: Symmetric(g56,g55,g59)
    c: Equal(g3,g58) = 14.15
    c: Equal(g0,g55) = 14.15
    c: Coincident(g60,g61)
    c: Coincident(g61,g62)
    c: Coincident(g62,g63)
    c: Coincident(g63,g60)
    c: Horizontal(g61)
    c: Horizontal(g63)
    c: Vertical(g60)
    c: Vertical(g62)
    c: Symmetric(g61,g60,g64)
    c: Equal(g3,g63) = 14.15
    c: Equal(g0,g60) = 14.15
    c: Coincident(g65,g66)
    c: Coincident(g66,g67)
    c: Coincident(g67,g68)
    c: Coincident(g68,g65)
    c: Horizontal(g66)
    c: Horizontal(g68)
    c: Vertical(g65)
    c: Vertical(g67)
    c: Symmetric(g66,g65,g69)
    c: Equal(g3,g68) = 14.15
    c: Equal(g0,g65) = 14.15
    c: Coincident(g70,g71)
    c: Coincident(g71,g72)
    c: Coincident(g72,g73)
    c: Coincident(g73,g70)
    c: Horizontal(g71)
    c: Horizontal(g73)
    c: Vertical(g70)
    c: Vertical(g72)
    c: Symmetric(g71,g70,g74)
    c: Equal(g3,g73) = 14.15
    c: Equal(g0,g70) = 14.15
    c: Coincident(g75,g76)
    c: Coincident(g76,g77)
    c: Coincident(g77,g78)
    c: Coincident(g78,g75)
    c: Horizontal(g76)
    c: Horizontal(g78)
    c: Vertical(g75)
    c: Vertical(g77)
    c: Symmetric(g76,g75,g79)
    c: Equal(g3,g78) = 14.15
    c: Equal(g0,g75) = 14.15
    c: Coincident(g80,g81)
    c: Coincident(g81,g82)
    c: Coincident(g82,g83)
    c: Coincident(g83,g80)
    c: Horizontal(g81)
    c: Horizontal(g83)
    c: Vertical(g80)
    c: Vertical(g82)
    c: Symmetric(g81,g80,g84)
    c: Equal(g3,g83) = 14.15
    c: Equal(g0,g80) = 14.15
    c: Coincident(g85,g86)
    c: Coincident(g86,g87)
    c: Coincident(g87,g88)
    c: Coincident(g88,g85)
    c: Horizontal(g86)
    c: Horizontal(g88)
    c: Vertical(g85)
    c: Vertical(g87)
    c: Symmetric(g86,g85,g89)
    c: Equal(g3,g88) = 14.15
    c: Equal(g0,g85) = 14.15
    c: Coincident(g90,g91)
    c: Coincident(g91,g92)
    c: Coincident(g92,g93)
    c: Coincident(g93,g90)
    c: Horizontal(g91)
    c: Horizontal(g93)
    c: Vertical(g90)
    c: Vertical(g92)
    c: Symmetric(g91,g90,g94)
    c: Equal(g3,g93) = 14.15
    c: Equal(g0,g90) = 14.15
    c: Coincident(g95,g96)
    c: Coincident(g96,g97)
    c: Coincident(g97,g98)
    c: Coincident(g98,g95)
    c: Horizontal(g96)
    c: Horizontal(g98)
    c: Vertical(g95)
    c: Vertical(g97)
    c: Symmetric(g96,g95,g99)
    c: Equal(g3,g98) = 14.15
    c: Equal(g0,g95) = 14.15
    c: Coincident(g100,g101)
    c: Coincident(g101,g102)
    c: Coincident(g102,g103)
    c: Coincident(g103,g100)
    c: Horizontal(g101)
    c: Horizontal(g103)
    c: Vertical(g100)
    c: Vertical(g102)
    c: Symmetric(g101,g100,g104)
    c: Equal(g3,g103) = 14.15
    c: Equal(g0,g100) = 14.15
    c: Coincident(g105,g106)
    c: Coincident(g106,g107)
    c: Coincident(g107,g108)
    c: Coincident(g108,g105)
    c: Horizontal(g106)
    c: Horizontal(g108)
    c: Vertical(g105)
    c: Vertical(g107)
    c: Symmetric(g106,g105,g109)
    c: Equal(g3,g108) = 14.15
    c: Equal(g0,g105) = 14.15
    c: Coincident(g110,g111)
    c: Coincident(g111,g112)
    c: Coincident(g112,g113)
    c: Coincident(g113,g110)
    c: Horizontal(g111)
    c: Horizontal(g113)
    c: Vertical(g110)
    c: Vertical(g112)
    c: Symmetric(g111,g110,g114)
    c: Equal(g3,g113) = 14.15
    c: Equal(g0,g110) = 14.15
    c: Coincident(g115,g116)
    c: Coincident(g116,g117)
    c: Coincident(g117,g118)
    c: Coincident(g118,g115)
    c: Horizontal(g116)
    c: Horizontal(g118)
    c: Vertical(g115)
    c: Vertical(g117)
    c: Symmetric(g116,g115,g119)
    c: Equal(g3,g118) = 14.15
    c: Equal(g0,g115) = 14.15
    c: Coincident(g120,g121)
    c: Coincident(g121,g122)
    c: Coincident(g122,g123)
    c: Coincident(g123,g120)
    c: Horizontal(g121)
    c: Horizontal(g123)
    c: Vertical(g120)
    c: Vertical(g122)
    c: Symmetric(g121,g120,g124)
    c: Equal(g3,g123) = 14.15
    c: Equal(g0,g120) = 14.15
    c: Coincident(g125,g126)
    c: Coincident(g126,g127)
    c: Coincident(g127,g128)
    c: Coincident(g128,g125)
    c: Horizontal(g126)
    c: Horizontal(g128)
    c: Vertical(g125)
    c: Vertical(g127)
    c: Symmetric(g126,g125,g129)
    c: Equal(g3,g128) = 14.15
    c: Equal(g0,g125) = 14.15
    c: Coincident(g130,g131)
    c: Coincident(g131,g132)
    c: Coincident(g132,g133)
    c: Coincident(g133,g130)
    c: Horizontal(g131)
    c: Horizontal(g133)
    c: Vertical(g130)
    c: Vertical(g132)
    c: Symmetric(g131,g130,g134)
    c: Equal(g3,g133) = 14.15
    c: Equal(g0,g130) = 14.15
    c: Coincident(g135,g136)
    c: Coincident(g136,g137)
    c: Coincident(g137,g138)
    c: Coincident(g138,g135)
    c: Horizontal(g136)
    c: Horizontal(g138)
    c: Vertical(g135)
    c: Vertical(g137)
    c: Symmetric(g136,g135,g139)
    c: Equal(g3,g138) = 14.15
    c: Equal(g0,g135) = 14.15
    c: Coincident(g140,g141)
    c: Coincident(g141,g142)
    c: Coincident(g142,g143)
    c: Coincident(g143,g140)
    c: Horizontal(g141)
    c: Horizontal(g143)
    c: Vertical(g140)
    c: Vertical(g142)
    c: Symmetric(g141,g140,g144)
    c: Equal(g3,g143) = 14.15
    c: Equal(g0,g140) = 14.15
    c: Vertical(g39,g34)
    c: Vertical(g34,g29)
    c: Vertical(g29,g24)
    c: Vertical(g59,g54)
    c: Vertical(g54,g49)
    c: Vertical(g49,g44)
    c: Vertical(g79,g74)
    c: Vertical(g74,g69)
    c: Vertical(g69,g64)
    c: Vertical(g104,g99)
    c: Vertical(g99,g94)
    c: Vertical(g94,g84)
    c: Vertical(g119,g114)
    c: Vertical(g114,g109)
    c: Vertical(g109,g89)
    c: Horizontal(g134,g124)
    c: Horizontal(g124,g129)
    c: DistanceY(g129,g9) = 19
    c: DistanceX(g129,g139) = 19
    c: DistanceX(g124,g129) = 19
    c: DistanceX(g134,g124) = 19
    c: DistanceX(g144,g134) = 19
    c: DistanceY(g139,g129) = 4.75
    c: DistanceY(g144,g134) = 4.75
    c: DistanceX(g9,g129) = 9.5
    c: DistanceY(g39,g34) = 19
    c: DistanceY(g34,g29) = 19
    c: DistanceY(g29,g24) = 19
    c: DistanceY(g59,g54) = 19
    c: DistanceY(g54,g49) = 19
    c: DistanceY(g49,g44) = 19
    c: DistanceY(g79,g74) = 19
    c: DistanceY(g74,g69) = 19
    c: DistanceY(g69,g64) = 19
    c: DistanceY(g104,g99) = 19
    c: DistanceY(g99,g94) = 19
    c: DistanceY(g94,g84) = 19
    c: DistanceY(g119,g114) = 19
    c: DistanceY(g114,g109) = 19
    c: DistanceY(g109,g89) = 19
    c: DistanceX(g34,g4) = 19
    c: DistanceX(g54,g34) = 19
    c: DistanceX(g74,g54) = 19
    c: DistanceX(g99,g74) = 19
    c: DistanceX(g114,g99) = 19
    c: Horizontal(g34,g4)
    c: Horizontal(g74,g34)
    c: DistanceY(g34,g54) = 4.75
    c: Horizontal(g114,g99)
    c: DistanceY(g74,g94) = 4.75
FEATURE [PartDesign::Pad] Pad  label="Base"
  Direction = (0,0,1)
  Length = 6.4
  Length2 = 10
  Profile = -> Sketch
  ReferenceAxis = -> Sketch [N_Axis]
  Type = 0
FEATURE [PartDesign::Pocket] Pocket  label="Switch Pocket"
  BaseFeature = -> Pad
  Direction = (0,0,-1)
  Length = 5
  Length2 = 5
  Profile = -> Sketch001
  ReferenceAxis = -> Sketch001 [N_Axis]
  Reversed = true
  Type = 1
FEATURE [Sketcher::SketchObject] Sketch002
  AttachmentOffset = pos=(0,0,3) rot=(0,0,1;0rad)
  FullyConstrained = true
  MapMode = 5
  Placement = pos=(0,0,3) rot=(0,0,1;0rad)
  Support = -> [XY_Plane]
  expr: .AttachmentOffset.Base.z = Spreadsheet.th_switch
  expr: Constraints[10] = Spreadsheet.sw_wi
  expr: Constraints[11] = Spreadsheet.sw_he
  expr: Constraints[23] = Spreadsheet.pl_spacing
  expr: Constraints[343] = Spreadsheet.pl_spacing
  expr: Constraints[344] = Spreadsheet.pl_spacing
  expr: Constraints[345] = Spreadsheet.pl_spacing
  expr: Constraints[346] = Spreadsheet.pl_spacing
  expr: Constraints[347] = Spreadsheet.pl_spacing
  expr: Constraints[348] = Spreadsheet.pl_sp4
  expr: Constraints[349] = Spreadsheet.pl_sp4
  expr: Constraints[350] = Spreadsheet.pl_sp2
  expr: Constraints[351] = Spreadsheet.pl_spacing
  expr: Constraints[352] = Spreadsheet.pl_spacing
  expr: Constraints[353] = Spreadsheet.pl_spacing
  expr: Constraints[354] = Spreadsheet.pl_spacing
  expr: Constraints[355] = Spreadsheet.pl_spacing
  expr: Constraints[356] = Spreadsheet.pl_spacing
  expr: Constraints[357] = Spreadsheet.pl_spacing
  expr: Constraints[358] = Spreadsheet.pl_spacing
  expr: Constraints[359] = Spreadsheet.pl_spacing
  expr: Constraints[360] = Spreadsheet.pl_spacing
  expr: Constraints[361] = Spreadsheet.pl_spacing
  expr: Constraints[362] = Spreadsheet.pl_spacing
  expr: Constraints[363] = Spreadsheet.pl_spacing
  expr: Constraints[364] = Spreadsheet.pl_spacing
  expr: Constraints[365] = Spreadsheet.pl_spacing
  expr: Constraints[366] = Spreadsheet.pl_spacing
  expr: Constraints[367] = Spreadsheet.pl_spacing
  expr: Constraints[368] = Spreadsheet.pl_spacing
  expr: Constraints[369] = Spreadsheet.pl_spacing
  expr: Constraints[370] = Spreadsheet.pl_spacing
  expr: Constraints[373] = Spreadsheet.pl_sp4
  expr: Constraints[375] = Spreadsheet.pl_sp4
  expr: Constraints[37] = Spreadsheet.pl_spacing
  expr: Constraints[413] = Spreadsheet.pl_edge
  expr: Constraints[414] = Spreadsheet.D15
  expr: Constraints[415] = Spreadsheet.D15
  expr: Constraints[416] = Spreadsheet.D15
  expr: Constraints[417] = Spreadsheet.D15
  expr: Constraints[418] = Spreadsheet.D15
  expr: Constraints[419] = Spreadsheet.D15
  expr: Constraints[420] = Spreadsheet.D15
  expr: Constraints[421] = Spreadsheet.D15
  expr: Constraints[422] = Spreadsheet.D15
  expr: Constraints[423] = Spreadsheet.D15
  expr: Constraints[424] = Spreadsheet.D15
  expr: Constraints[425] = Spreadsheet.D15
  expr: Constraints[426] = Spreadsheet.D15
  expr: Constraints[427] = Spreadsheet.D15
  expr: Constraints[428] = Spreadsheet.D15
  expr: Constraints[429] = Spreadsheet.D15
  expr: Constraints[430] = Spreadsheet.D15
  expr: Constraints[431] = Spreadsheet.D15
  expr: Constraints[432] = Spreadsheet.D15
  expr: Constraints[444] = Spreadsheet.pl_edge
  expr: Constraints[50] = Spreadsheet.pl_spacing
  sketch-geometry (169):
    g0: LineSegment StartX=-7 StartY=7 StartZ=0 EndX=-7 EndY=-7 EndZ=0
    g1: LineSegment StartX=-7 StartY=-7 StartZ=0 EndX=7 EndY=-7 EndZ=0
    g2: LineSegment StartX=7 StartY=-7 StartZ=0 EndX=7 EndY=7 EndZ=0
    g3: LineSegment StartX=7 StartY=7 StartZ=0 EndX=-7 EndY=7 EndZ=0
    g4: GeomPoint X=0 Y=0 Z=0
    g5: LineSegment StartX=-7 StartY=-12 StartZ=0 EndX=-7 EndY=-26 EndZ=0
    g6: LineSegment StartX=-7 StartY=-26 StartZ=0 EndX=7 EndY=-26 EndZ=0
    g7: LineSegment StartX=7 StartY=-26 StartZ=0 EndX=7 EndY=-12 EndZ=0
    g8: LineSegment StartX=7 StartY=-12 StartZ=0 EndX=-7 EndY=-12 EndZ=0
    g9: GeomPoint X=0 Y=-19 Z=0
    g10: LineSegment StartX=-7 StartY=26 StartZ=0 EndX=-7 EndY=12 EndZ=0
    g11: LineSegment StartX=-7 StartY=12 StartZ=0 EndX=7 EndY=12 EndZ=0
    g12: LineSegment StartX=7 StartY=12 StartZ=0 EndX=7 EndY=26 EndZ=0
    g13: LineSegment StartX=7 StartY=26 StartZ=0 EndX=-7 EndY=26 EndZ=0
    g14: GeomPoint X=0 Y=19 Z=0
    g15: LineSegment StartX=-7 StartY=45 StartZ=0 EndX=-7 EndY=31 EndZ=0
    g16: LineSegment StartX=-7 StartY=31 StartZ=0 EndX=7 EndY=31 EndZ=0
    g17: LineSegment StartX=7 StartY=31 StartZ=0 EndX=7 EndY=45 EndZ=0
    g18: LineSegment StartX=7 StartY=45 StartZ=0 EndX=-7 EndY=45 EndZ=0
    g19: GeomPoint X=0 Y=38 Z=0
    g20: LineSegment StartX=-26 StartY=45 StartZ=0 EndX=-26 EndY=31 EndZ=0
    g21: LineSegment StartX=-26 StartY=31 StartZ=0 EndX=-12 EndY=31 EndZ=0
    g22: LineSegment StartX=-12 StartY=31 StartZ=0 EndX=-12 EndY=45 EndZ=0
    g23: LineSegment StartX=-12 StartY=45 StartZ=0 EndX=-26 EndY=45 EndZ=0
    g24: GeomPoint X=-19 Y=38 Z=0
    g25: LineSegment StartX=-26 StartY=26 StartZ=0 EndX=-26 EndY=12 EndZ=0
    g26: LineSegment StartX=-26 StartY=12 StartZ=0 EndX=-12 EndY=12 EndZ=0
    g27: LineSegment StartX=-12 StartY=12 StartZ=0 EndX=-12 EndY=26 EndZ=0
    g28: LineSegment StartX=-12 StartY=26 StartZ=0 EndX=-26 EndY=26 EndZ=0
    g29: GeomPoint X=-19 Y=19 Z=0
    g30: LineSegment StartX=-26 StartY=7 StartZ=0 EndX=-26 EndY=-7 EndZ=0
    g31: LineSegment StartX=-26 StartY=-7 StartZ=0 EndX=-12 EndY=-7 EndZ=0
    g32: LineSegment StartX=-12 StartY=-7 StartZ=0 EndX=-12 EndY=7 EndZ=0
    g33: LineSegment StartX=-12 StartY=7 StartZ=0 EndX=-26 EndY=7 EndZ=0
    g34: GeomPoint X=-19 Y=0 Z=0
    g35: LineSegment StartX=-26 StartY=-12 StartZ=0 EndX=-26 EndY=-26 EndZ=0
    g36: LineSegment StartX=-26 StartY=-26 StartZ=0 EndX=-12 EndY=-26 EndZ=0
    g37: LineSegment StartX=-12 StartY=-26 StartZ=0 EndX=-12 EndY=-12 EndZ=0
    g38: LineSegment StartX=-12 StartY=-12 StartZ=0 EndX=-26 EndY=-12 EndZ=0
    g39: GeomPoint X=-19 Y=-19 Z=0
    g40: LineSegment StartX=-45 StartY=49.75 StartZ=0 EndX=-45 EndY=35.75 EndZ=0
    g41: LineSegment StartX=-45 StartY=35.75 StartZ=0 EndX=-31 EndY=35.75 EndZ=0
    g42: LineSegment StartX=-31 StartY=35.75 StartZ=0 EndX=-31 EndY=49.75 EndZ=0
    g43: LineSegment StartX=-31 StartY=49.75 StartZ=0 EndX=-45 EndY=49.75 EndZ=0
    g44: GeomPoint X=-38 Y=42.75 Z=0
    g45: LineSegment StartX=-45 StartY=30.75 StartZ=0 EndX=-45 EndY=16.75 EndZ=0
    g46: LineSegment StartX=-45 StartY=16.75 StartZ=0 EndX=-31 EndY=16.75 EndZ=0
    g47: LineSegment StartX=-31 StartY=16.75 StartZ=0 EndX=-31 EndY=30.75 EndZ=0
    g48: LineSegment StartX=-31 StartY=30.75 StartZ=0 EndX=-45 EndY=30.75 EndZ=0
    g49: GeomPoint X=-38 Y=23.75 Z=0
    g50: LineSegment StartX=-45 StartY=11.75 StartZ=0 EndX=-45 EndY=-2.25 EndZ=0
    g51: LineSegment StartX=-45 StartY=-2.25 StartZ=0 EndX=-31 EndY=-2.25 EndZ=0
    g52: LineSegment StartX=-31 StartY=-2.25 StartZ=0 EndX=-31 EndY=11.75 EndZ=0
    g53: LineSegment StartX=-31 StartY=11.75 StartZ=0 EndX=-45 EndY=11.75 EndZ=0
    g54: GeomPoint X=-38 Y=4.75 Z=0
    g55: LineSegment StartX=-45 StartY=-7.25 StartZ=0 EndX=-45 EndY=-21.25 EndZ=0
    g56: LineSegment StartX=-45 StartY=-21.25 StartZ=0 EndX=-31 EndY=-21.25 EndZ=0
    g57: LineSegment StartX=-31 StartY=-21.25 StartZ=0 EndX=-31 EndY=-7.25 EndZ=0
    g58: LineSegment StartX=-31 StartY=-7.25 StartZ=0 EndX=-45 EndY=-7.25 EndZ=0
    g59: GeomPoint X=-38 Y=-14.25 Z=0
    g60: LineSegment StartX=-64 StartY=45 StartZ=0 EndX=-64 EndY=31 EndZ=0
    g61: LineSegment StartX=-64 StartY=31 StartZ=0 EndX=-50 EndY=31 EndZ=0
    g62: LineSegment StartX=-50 StartY=31 StartZ=0 EndX=-50 EndY=45 EndZ=0
    g63: LineSegment StartX=-50 StartY=45 StartZ=0 EndX=-64 EndY=45 EndZ=0
    g64: GeomPoint X=-57 Y=38 Z=0
    g65: LineSegment StartX=-64 StartY=26 StartZ=0 EndX=-64 EndY=12 EndZ=0
    g66: LineSegment StartX=-64 StartY=12 StartZ=0 EndX=-50 EndY=12 EndZ=0
    g67: LineSegment StartX=-50 StartY=12 StartZ=0 EndX=-50 EndY=26 EndZ=0
    g68: LineSegment StartX=-50 StartY=26 StartZ=0 EndX=-64 EndY=26 EndZ=0
    g69: GeomPoint X=-57 Y=19 Z=0
    g70: LineSegment StartX=-64 StartY=7 StartZ=0 EndX=-64 EndY=-7 EndZ=0
    g71: LineSegment StartX=-64 StartY=-7 StartZ=0 EndX=-50 EndY=-7 EndZ=0
    g72: LineSegment StartX=-50 StartY=-7 StartZ=0 EndX=-50 EndY=7 EndZ=0
    g73: LineSegment StartX=-50 StartY=7 StartZ=0 EndX=-64 EndY=7 EndZ=0
    g74: GeomPoint X=-57 Y=0 Z=0
    g75: LineSegment StartX=-64 StartY=-12 StartZ=0 EndX=-64 EndY=-26 EndZ=0
    g76: LineSegment StartX=-64 StartY=-26 StartZ=0 EndX=-50 EndY=-26 EndZ=0
    g77: LineSegment StartX=-50 StartY=-26 StartZ=0 EndX=-50 EndY=-12 EndZ=0
    g78: LineSegment StartX=-50 StartY=-12 StartZ=0 EndX=-64 EndY=-12 EndZ=0
    g79: GeomPoint X=-57 Y=-19 Z=0
    g80: LineSegment StartX=-83 StartY=30.75 StartZ=0 EndX=-83 EndY=16.75 EndZ=0
    g81: LineSegment StartX=-83 StartY=16.75 StartZ=0 EndX=-69 EndY=16.75 EndZ=0
    g82: LineSegment StartX=-69 StartY=16.75 StartZ=0 EndX=-69 EndY=30.75 EndZ=0
    g83: LineSegment StartX=-69 StartY=30.75 StartZ=0 EndX=-83 EndY=30.75 EndZ=0
    g84: GeomPoint X=-76 Y=23.75 Z=0
    g85: LineSegment StartX=-102 StartY=30.75 StartZ=0 EndX=-102 EndY=16.75 EndZ=0
    g86: LineSegment StartX=-102 StartY=16.75 StartZ=0 EndX=-88 EndY=16.75 EndZ=0
    g87: LineSegment StartX=-88 StartY=16.75 StartZ=0 EndX=-88 EndY=30.75 EndZ=0
    g88: LineSegment StartX=-88 StartY=30.75 StartZ=0 EndX=-102 EndY=30.75 EndZ=0
    g89: GeomPoint X=-95 Y=23.75 Z=0
    g90: LineSegment StartX=-83 StartY=11.75 StartZ=0 EndX=-83 EndY=-2.25 EndZ=0
    g91: LineSegment StartX=-83 StartY=-2.25 StartZ=0 EndX=-69 EndY=-2.25 EndZ=0
    g92: LineSegment StartX=-69 StartY=-2.25 StartZ=0 EndX=-69 EndY=11.75 EndZ=0
    g93: LineSegment StartX=-69 StartY=11.75 StartZ=0 EndX=-83 EndY=11.75 EndZ=0
    g94: GeomPoint X=-76 Y=4.75 Z=0
    g95: LineSegment StartX=-83 StartY=-7.25 StartZ=0 EndX=-83 EndY=-21.25 EndZ=0
    g96: LineSegment StartX=-83 StartY=-21.25 StartZ=0 EndX=-69 EndY=-21.25 EndZ=0
    g97: LineSegment StartX=-69 StartY=-21.25 StartZ=0 EndX=-69 EndY=-7.25 EndZ=0
    g98: LineSegment StartX=-69 StartY=-7.25 StartZ=0 EndX=-83 EndY=-7.25 EndZ=0
    g99: GeomPoint X=-76 Y=-14.25 Z=0
    g100: LineSegment StartX=-83 StartY=-26.25 StartZ=0 EndX=-83 EndY=-40.25 EndZ=0
    g101: LineSegment StartX=-83 StartY=-40.25 StartZ=0 EndX=-69 EndY=-40.25 EndZ=0
    g102: LineSegment StartX=-69 StartY=-40.25 StartZ=0 EndX=-69 EndY=-26.25 EndZ=0
    g103: LineSegment StartX=-69 StartY=-26.25 StartZ=0 EndX=-83 EndY=-26.25 EndZ=0
    g104: GeomPoint X=-76 Y=-33.25 Z=0
    g105: LineSegment StartX=-102 StartY=11.75 StartZ=0 EndX=-102 EndY=-2.25 EndZ=0
    g106: LineSegment StartX=-102 StartY=-2.25 StartZ=0 EndX=-88 EndY=-2.25 EndZ=0
    g107: LineSegment StartX=-88 StartY=-2.25 StartZ=0 EndX=-88 EndY=11.75 EndZ=0
    g108: LineSegment StartX=-88 StartY=11.75 StartZ=0 EndX=-102 EndY=11.75 EndZ=0
    g109: GeomPoint X=-95 Y=4.75 Z=0
    g110: LineSegment StartX=-102 StartY=-7.25 StartZ=0 EndX=-102 EndY=-21.25 EndZ=0
    g111: LineSegment StartX=-102 StartY=-21.25 StartZ=0 EndX=-88 EndY=-21.25 EndZ=0
    g112: LineSegment StartX=-88 StartY=-21.25 StartZ=0 EndX=-88 EndY=-7.25 EndZ=0
    g113: LineSegment StartX=-88 StartY=-7.25 StartZ=0 EndX=-102 EndY=-7.25 EndZ=0
    g114: GeomPoint X=-95 Y=-14.25 Z=0
    g115: LineSegment StartX=-102 StartY=-26.25 StartZ=0 EndX=-102 EndY=-40.25 EndZ=0
    g116: LineSegment StartX=-102 StartY=-40.25 StartZ=0 EndX=-88 EndY=-40.25 EndZ=0
    g117: LineSegment StartX=-88 StartY=-40.25 StartZ=0 EndX=-88 EndY=-26.25 EndZ=0
    g118: LineSegment StartX=-88 StartY=-26.25 StartZ=0 EndX=-102 EndY=-26.25 EndZ=0
    g119: GeomPoint X=-95 Y=-33.25 Z=0
    g120: LineSegment StartX=-16.5 StartY=-31 StartZ=0 EndX=-16.5 EndY=-45 EndZ=0
    g121: LineSegment StartX=-16.5 StartY=-45 StartZ=0 EndX=-2.5 EndY=-45 EndZ=0
    g122: LineSegment StartX=-2.5 StartY=-45 StartZ=0 EndX=-2.5 EndY=-31 EndZ=0
    g123: LineSegment StartX=-2.5 StartY=-31 StartZ=0 EndX=-16.5 EndY=-31 EndZ=0
    g124: GeomPoint X=-9.5 Y=-38 Z=0
    g125: LineSegment StartX=2.5 StartY=-31 StartZ=0 EndX=2.5 EndY=-45 EndZ=0
    g126: LineSegment StartX=2.5 StartY=-45 StartZ=0 EndX=16.5 EndY=-45 EndZ=0
    g127: LineSegment StartX=16.5 StartY=-45 StartZ=0 EndX=16.5 EndY=-31 EndZ=0
    g128: LineSegment StartX=16.5 StartY=-31 StartZ=0 EndX=2.5 EndY=-31 EndZ=0
    g129: GeomPoint X=9.5 Y=-38 Z=0
    g130: LineSegment StartX=-35.5 StartY=-31 StartZ=0 EndX=-35.5 EndY=-45 EndZ=0
    g131: LineSegment StartX=-35.5 StartY=-45 StartZ=0 EndX=-21.5 EndY=-45 EndZ=0
    g132: LineSegment StartX=-21.5 StartY=-45 StartZ=0 EndX=-21.5 EndY=-31 EndZ=0
    g133: LineSegment StartX=-21.5 StartY=-31 StartZ=0 EndX=-35.5 EndY=-31 EndZ=0
    g134: GeomPoint X=-28.5 Y=-38 Z=0
    g135: LineSegment StartX=21.5 StartY=-35.75 StartZ=0 EndX=21.5 EndY=-49.75 EndZ=0
    g136: LineSegment StartX=21.5 StartY=-49.75 StartZ=0 EndX=35.5 EndY=-49.75 EndZ=0
    g137: LineSegment StartX=35.5 StartY=-49.75 StartZ=0 EndX=35.5 EndY=-35.75 EndZ=0
    g138: LineSegment StartX=35.5 StartY=-35.75 StartZ=0 EndX=21.5 EndY=-35.75 EndZ=0
    g139: GeomPoint X=28.5 Y=-42.75 Z=0
    g140: LineSegment StartX=-54.5 StartY=-35.75 StartZ=0 EndX=-54.5 EndY=-49.75 EndZ=0
    g141: LineSegment StartX=-54.5 StartY=-49.75 StartZ=0 EndX=-40.5 EndY=-49.75 EndZ=0
    g142: LineSegment StartX=-40.5 StartY=-49.75 StartZ=0 EndX=-40.5 EndY=-35.75 EndZ=0
    g143: LineSegment StartX=-40.5 StartY=-35.75 StartZ=0 EndX=-54.5 EndY=-35.75 EndZ=0
    g144: GeomPoint X=-47.5 Y=-42.75 Z=0
    g145: LineSegment StartX=9 StartY=-29 StartZ=0 EndX=18.5 EndY=-29 EndZ=0
    g146: LineSegment StartX=18.5 StartY=-29 StartZ=0 EndX=18.5 EndY=-33.75 EndZ=0
    g147: LineSegment StartX=18.5 StartY=-33.75 StartZ=0 EndX=37.5 EndY=-33.75 EndZ=0
    g148: LineSegment StartX=37.5 StartY=-33.75 StartZ=0 EndX=37.5 EndY=-51.75 EndZ=0
    g149: LineSegment StartX=37.5 StartY=-51.75 StartZ=0 EndX=19.5 EndY=-51.75 EndZ=0
    g150: LineSegment StartX=19.5 StartY=-51.75 StartZ=0 EndX=19.5 EndY=-47 EndZ=0
    g151: LineSegment StartX=19.5 StartY=-47 StartZ=0 EndX=-38.5 EndY=-47 EndZ=0
    g152: LineSegment StartX=-38.5 StartY=-47 StartZ=0 EndX=-38.5 EndY=-51.75 EndZ=0
    g153: LineSegment StartX=-38.5 StartY=-51.75 StartZ=0 EndX=-56.5 EndY=-51.75 EndZ=0
    g154: LineSegment StartX=-56.5 StartY=-51.75 StartZ=0 EndX=-56.5 EndY=-42.25 EndZ=0
    g155: LineSegment StartX=-56.5 StartY=-42.25 StartZ=0 EndX=-104 EndY=-42.25 EndZ=0
    g156: LineSegment StartX=-104 StartY=-42.25 StartZ=0 EndX=-104 EndY=32.75 EndZ=0
    g157: LineSegment StartX=-104 StartY=32.75 StartZ=0 EndX=-66 EndY=32.75 EndZ=0
    g158: LineSegment StartX=-66 StartY=32.75 StartZ=0 EndX=-66 EndY=47 EndZ=0
    g159: LineSegment StartX=-66 StartY=47 StartZ=0 EndX=-47 EndY=47 EndZ=0
    g160: LineSegment StartX=-47 StartY=47 StartZ=0 EndX=-47 EndY=51.75 EndZ=0
    g161: LineSegment StartX=-47 StartY=51.75 StartZ=0 EndX=-29 EndY=51.75 EndZ=0
    g162: LineSegment StartX=-29 StartY=51.75 StartZ=0 EndX=-29 EndY=47 EndZ=0
    g163: LineSegment StartX=-29 StartY=47 StartZ=0 EndX=9 EndY=47 EndZ=0
    g164: LineSegment StartX=9 StartY=-29 StartZ=0 EndX=9 EndY=-21.1 EndZ=0
    g165: LineSegment StartX=9 StartY=-21.1 StartZ=0 EndX=51.25 EndY=-21.1 EndZ=0
    g166: LineSegment StartX=51.25 StartY=-21.1 StartZ=0 EndX=51.25 EndY=27.6 EndZ=0
    g167: LineSegment StartX=51.25 StartY=27.6 StartZ=0 EndX=9 EndY=27.6 EndZ=0
    g168: LineSegment StartX=9 StartY=27.6 StartZ=0 EndX=9 EndY=47 EndZ=0
  constraints (448):
    c: Coincident(g0,g1)
    c: Coincident(g1,g2)
    c: Coincident(g2,g3)
    c: Coincident(g3,g0)
    c: Horizontal(g1)
    c: Horizontal(g3)
    c: Vertical(g0)
    c: Vertical(g2)
    c: Symmetric(g1,g0,g4)
    c: Coincident(g4,g-1)
    c: DistanceX(g3,g3) = 14
    c: DistanceY(g0,g0) = 14
    c: Coincident(g5,g6)
    c: Coincident(g6,g7)
    c: Coincident(g7,g8)
    c: Coincident(g8,g5)
    c: Horizontal(g6)
    c: Horizontal(g8)
    c: Vertical(g5)
    c: Vertical(g7)
    c: Symmetric(g6,g5,g9)
    c: Equal(g3,g8) = 14.15
    c: Equal(g0,g5) = 14.15
    c: DistanceY(g9,g4) = 19
    c: Vertical(g9,g4)
    c: Coincident(g10,g11)
    c: Coincident(g11,g12)
    c: Coincident(g12,g13)
    c: Coincident(g13,g10)
    c: Horizontal(g11)
    c: Horizontal(g13)
    c: Vertical(g10)
    c: Vertical(g12)
    c: Symmetric(g11,g10,g14)
    c: Equal(g3,g13) = 14.15
    c: Equal(g0,g10) = 14.15
    c: Vertical(g4,g14)
    c: DistanceY(g4,g14) = 19
    c: Coincident(g15,g16)
    c: Coincident(g16,g17)
    c: Coincident(g17,g18)
    c: Coincident(g18,g15)
    c: Horizontal(g16)
    c: Horizontal(g18)
    c: Vertical(g15)
    c: Vertical(g17)
    c: Symmetric(g16,g15,g19)
    c: Equal(g3,g18) = 14.15
    c: Equal(g0,g15) = 14.15
    c: Vertical(g19,g4)
    c: DistanceY(g14,g19) = 19
    c: Coincident(g20,g21)
    c: Coincident(g21,g22)
    c: Coincident(g22,g23)
    c: Coincident(g23,g20)
    c: Horizontal(g21)
    c: Horizontal(g23)
    c: Vertical(g20)
    c: Vertical(g22)
    c: Symmetric(g21,g20,g24)
    c: Equal(g3,g23) = 14.15
    c: Equal(g0,g20) = 14.15
    c: Coincident(g25,g26)
    c: Coincident(g26,g27)
    c: Coincident(g27,g28)
    c: Coincident(g28,g25)
    c: Horizontal(g26)
    c: Horizontal(g28)
    c: Vertical(g25)
    c: Vertical(g27)
    c: Symmetric(g26,g25,g29)
    c: Equal(g3,g28) = 14.15
    c: Equal(g0,g25) = 14.15
    c: Coincident(g30,g31)
    c: Coincident(g31,g32)
    c: Coincident(g32,g33)
    c: Coincident(g33,g30)
    c: Horizontal(g31)
    c: Horizontal(g33)
    c: Vertical(g30)
    c: Vertical(g32)
    c: Symmetric(g31,g30,g34)
    c: Equal(g3,g33) = 14.15
    c: Equal(g0,g30) = 14.15
    c: Coincident(g35,g36)
    c: Coincident(g36,g37)
    c: Coincident(g37,g38)
    c: Coincident(g38,g35)
    c: Horizontal(g36)
    c: Horizontal(g38)
    c: Vertical(g35)
    c: Vertical(g37)
    c: Symmetric(g36,g35,g39)
    c: Equal(g3,g38) = 14.15
    c: Equal(g0,g35) = 14.15
    c: Coincident(g40,g41)
    c: Coincident(g41,g42)
    c: Coincident(g42,g43)
    c: Coincident(g43,g40)
    c: Horizontal(g41)
    c: Horizontal(g43)
    c: Vertical(g40)
    c: Vertical(g42)
    c: Symmetric(g41,g40,g44)
    c: Equal(g3,g43) = 14.15
    c: Equal(g0,g40) = 14.15
    c: Coincident(g45,g46)
    c: Coincident(g46,g47)
    c: Coincident(g47,g48)
    c: Coincident(g48,g45)
    c: Horizontal(g46)
    c: Horizontal(g48)
    c: Vertical(g45)
    c: Vertical(g47)
    c: Symmetric(g46,g45,g49)
    c: Equal(g3,g48) = 14.15
    c: Equal(g0,g45) = 14.15
    c: Coincident(g50,g51)
    c: Coincident(g51,g52)
    c: Coincident(g52,g53)
    c: Coincident(g53,g50)
    c: Horizontal(g51)
    c: Horizontal(g53)
    c: Vertical(g50)
    c: Vertical(g52)
    c: Symmetric(g51,g50,g54)
    c: Equal(g3,g53) = 14.15
    c: Equal(g0,g50) = 14.15
    c: Coincident(g55,g56)
    c: Coincident(g56,g57)
    c: Coincident(g57,g58)
    c: Coincident(g58,g55)
    c: Horizontal(g56)
    c: Horizontal(g58)
    c: Vertical(g55)
    c: Vertical(g57)
    c: Symmetric(g56,g55,g59)
    c: Equal(g3,g58) = 14.15
    c: Equal(g0,g55) = 14.15
    c: Coincident(g60,g61)
    c: Coincident(g61,g62)
    c: Coincident(g62,g63)
    c: Coincident(g63,g60)
    c: Horizontal(g61)
    c: Horizontal(g63)
    c: Vertical(g60)
    c: Vertical(g62)
    c: Symmetric(g61,g60,g64)
    c: Equal(g3,g63) = 14.15
    c: Equal(g0,g60) = 14.15
    c: Coincident(g65,g66)
    c: Coincident(g66,g67)
    c: Coincident(g67,g68)
    c: Coincident(g68,g65)
    c: Horizontal(g66)
    c: Horizontal(g68)
    c: Vertical(g65)
    c: Vertical(g67)
    c: Symmetric(g66,g65,g69)
    c: Equal(g3,g68) = 14.15
    c: Equal(g0,g65) = 14.15
    c: Coincident(g70,g71)
    c: Coincident(g71,g72)
    c: Coincident(g72,g73)
    c: Coincident(g73,g70)
    c: Horizontal(g71)
    c: Horizontal(g73)
    c: Vertical(g70)
    c: Vertical(g72)
    c: Symmetric(g71,g70,g74)
    c: Equal(g3,g73) = 14.15
    c: Equal(g0,g70) = 14.15
    c: Coincident(g75,g76)
    c: Coincident(g76,g77)
    c: Coincident(g77,g78)
    c: Coincident(g78,g75)
    c: Horizontal(g76)
    c: Horizontal(g78)
    c: Vertical(g75)
    c: Vertical(g77)
    c: Symmetric(g76,g75,g79)
    c: Equal(g3,g78) = 14.15
    c: Equal(g0,g75) = 14.15
    c: Coincident(g80,g81)
    c: Coincident(g81,g82)
    c: Coincident(g82,g83)
    c: Coincident(g83,g80)
    c: Horizontal(g81)
    c: Horizontal(g83)
    c: Vertical(g80)
    c: Vertical(g82)
    c: Symmetric(g81,g80,g84)
    c: Equal(g3,g83) = 14.15
    c: Equal(g0,g80) = 14.15
    c: Coincident(g85,g86)
    c: Coincident(g86,g87)
    c: Coincident(g87,g88)
    c: Coincident(g88,g85)
    c: Horizontal(g86)
    c: Horizontal(g88)
    c: Vertical(g85)
    c: Vertical(g87)
    c: Symmetric(g86,g85,g89)
    c: Equal(g3,g88) = 14.15
    c: Equal(g0,g85) = 14.15
    c: Coincident(g90,g91)
    c: Coincident(g91,g92)
    c: Coincident(g92,g93)
    c: Coincident(g93,g90)
    c: Horizontal(g91)
    c: Horizontal(g93)
    c: Vertical(g90)
    c: Vertical(g92)
    c: Symmetric(g91,g90,g94)
    c: Equal(g3,g93) = 14.15
    c: Equal(g0,g90) = 14.15
    c: Coincident(g95,g96)
    c: Coincident(g96,g97)
    c: Coincident(g97,g98)
    c: Coincident(g98,g95)
    c: Horizontal(g96)
    c: Horizontal(g98)
    c: Vertical(g95)
    c: Vertical(g97)
    c: Symmetric(g96,g95,g99)
    c: Equal(g3,g98) = 14.15
    c: Equal(g0,g95) = 14.15
    c: Coincident(g100,g101)
    c: Coincident(g101,g102)
    c: Coincident(g102,g103)
    c: Coincident(g103,g100)
    c: Horizontal(g101)
    c: Horizontal(g103)
    c: Vertical(g100)
    c: Vertical(g102)
    c: Symmetric(g101,g100,g104)
    c: Equal(g3,g103) = 14.15
    c: Equal(g0,g100) = 14.15
    c: Coincident(g105,g106)
    c: Coincident(g106,g107)
    c: Coincident(g107,g108)
    c: Coincident(g108,g105)
    c: Horizontal(g106)
    c: Horizontal(g108)
    c: Vertical(g105)
    c: Vertical(g107)
    c: Symmetric(g106,g105,g109)
    c: Equal(g3,g108) = 14.15
    c: Equal(g0,g105) = 14.15
    c: Coincident(g110,g111)
    c: Coincident(g111,g112)
    c: Coincident(g112,g113)
    c: Coincident(g113,g110)
    c: Horizontal(g111)
    c: Horizontal(g113)
    c: Vertical(g110)
    c: Vertical(g112)
    c: Symmetric(g111,g110,g114)
    c: Equal(g3,g113) = 14.15
    c: Equal(g0,g110) = 14.15
    c: Coincident(g115,g116)
    c: Coincident(g116,g117)
    c: Coincident(g117,g118)
    c: Coincident(g118,g115)
    c: Horizontal(g116)
    c: Horizontal(g118)
    c: Vertical(g115)
    c: Vertical(g117)
    c: Symmetric(g116,g115,g119)
    c: Equal(g3,g118) = 14.15
    c: Equal(g0,g115) = 14.15
    c: Coincident(g120,g121)
    c: Coincident(g121,g122)
    c: Coincident(g122,g123)
    c: Coincident(g123,g120)
    c: Horizontal(g121)
    c: Horizontal(g123)
    c: Vertical(g120)
    c: Vertical(g122)
    c: Symmetric(g121,g120,g124)
    c: Equal(g3,g123) = 14.15
    c: Equal(g0,g120) = 14.15
    c: Coincident(g125,g126)
    c: Coincident(g126,g127)
    c: Coincident(g127,g128)
    c: Coincident(g128,g125)
    c: Horizontal(g126)
    c: Horizontal(g128)
    c: Vertical(g125)
    c: Vertical(g127)
    c: Symmetric(g126,g125,g129)
    c: Equal(g3,g128) = 14.15
    c: Equal(g0,g125) = 14.15
    c: Coincident(g130,g131)
    c: Coincident(g131,g132)
    c: Coincident(g132,g133)
    c: Coincident(g133,g130)
    c: Horizontal(g131)
    c: Horizontal(g133)
    c: Vertical(g130)
    c: Vertical(g132)
    c: Symmetric(g131,g130,g134)
    c: Equal(g3,g133) = 14.15
    c: Equal(g0,g130) = 14.15
    c: Coincident(g135,g136)
    c: Coincident(g136,g137)
    c: Coincident(g137,g138)
    c: Coincident(g138,g135)
    c: Horizontal(g136)
    c: Horizontal(g138)
    c: Vertical(g135)
    c: Vertical(g137)
    c: Symmetric(g136,g135,g139)
    c: Equal(g3,g138) = 14.15
    c: Equal(g0,g135) = 14.15
    c: Coincident(g140,g141)
    c: Coincident(g141,g142)
    c: Coincident(g142,g143)
    c: Coincident(g143,g140)
    c: Horizontal(g141)
    c: Horizontal(g143)
    c: Vertical(g140)
    c: Vertical(g142)
    c: Symmetric(g141,g140,g144)
    c: Equal(g3,g143) = 14.15
    c: Equal(g0,g140) = 14.15
    c: Vertical(g39,g34)
    c: Vertical(g34,g29)
    c: Vertical(g29,g24)
    c: Vertical(g59,g54)
    c: Vertical(g54,g49)
    c: Vertical(g49,g44)
    c: Vertical(g79,g74)
    c: Vertical(g74,g69)
    c: Vertical(g69,g64)
    c: Vertical(g104,g99)
    c: Vertical(g99,g94)
    c: Vertical(g94,g84)
    c: Vertical(g119,g114)
    c: Vertical(g114,g109)
    c: Vertical(g109,g89)
    c: Horizontal(g134,g124)
    c: Horizontal(g124,g129)
    c: DistanceY(g129,g9) = 19
    c: DistanceX(g129,g139) = 19
    c: DistanceX(g124,g129) = 19
    c: DistanceX(g134,g124) = 19
    c: DistanceX(g144,g134) = 19
    c: DistanceY(g139,g129) = 4.75
    c: DistanceY(g144,g134) = 4.75
    c: DistanceX(g9,g129) = 9.5
    c: DistanceY(g39,g34) = 19
    c: DistanceY(g34,g29) = 19
    c: DistanceY(g29,g24) = 19
    c: DistanceY(g59,g54) = 19
    c: DistanceY(g54,g49) = 19
    c: DistanceY(g49,g44) = 19
    c: DistanceY(g79,g74) = 19
    c: DistanceY(g74,g69) = 19
    c: DistanceY(g69,g64) = 19
    c: DistanceY(g104,g99) = 19
    c: DistanceY(g99,g94) = 19
    c: DistanceY(g94,g84) = 19
    c: DistanceY(g119,g114) = 19
    c: DistanceY(g114,g109) = 19
    c: DistanceY(g109,g89) = 19
    c: DistanceX(g34,g4) = 19
    c: DistanceX(g54,g34) = 19
    c: DistanceX(g74,g54) = 19
    c: DistanceX(g99,g74) = 19
    c: DistanceX(g114,g99) = 19
    c: Horizontal(g34,g4)
    c: Horizontal(g74,g34)
    c: DistanceY(g34,g54) = 4.75
    c: Horizontal(g114,g99)
    c: DistanceY(g74,g94) = 4.75
    c: Horizontal(g145)
    c: Coincident(g145,g146)
    c: Vertical(g146)
    c: Coincident(g146,g147)
    c: Horizontal(g147)
    c: Coincident(g147,g148)
    c: Vertical(g148)
    c: Coincident(g148,g149)
    c: Horizontal(g149)
    c: Coincident(g149,g150)
    c: Vertical(g150)
    c: Coincident(g150,g151)
    c: Horizontal(g151)
    c: Coincident(g151,g152)
    c: Vertical(g152)
    c: Coincident(g152,g153)
    c: Horizontal(g153)
    c: Coincident(g153,g154)
    c: Vertical(g154)
    c: Coincident(g154,g155)
    c: Horizontal(g155)
    c: Coincident(g155,g156)
    c: Vertical(g156)
    c: Coincident(g156,g157)
    c: Horizontal(g157)
    c: Coincident(g157,g158)
    c: Vertical(g158)
    c: Coincident(g158,g159)
    c: Horizontal(g159)
    c: Coincident(g159,g160)
    c: Vertical(g160)
    c: Coincident(g160,g161)
    c: Horizontal(g161)
    c: Coincident(g161,g162)
    c: Vertical(g162)
    c: Coincident(g162,g163)
    c: Horizontal(g163)
    c: DistanceX(g19,g163) = 9
    c: DistanceX(g44,g161) = 9
    c: DistanceX(g160,g44) = 9
    c: DistanceX(g158,g64) = 9
    c: DistanceX(g156,g89) = 9
    c: DistanceX(g153,g144) = 9
    c: DistanceX(g144,g152) = 9
    c: DistanceX(g149,g139) = 9
    c: DistanceX(g139,g148) = 9
    c: DistanceX(g129,g145) = 9
    c: DistanceY(g19,g163) = 9
    c: DistanceY(g44,g161) = 9
    c: DistanceY(g64,g158) = 9
    c: DistanceY(g89,g156) = 9
    c: DistanceY(g155,g119) = 9
    c: DistanceY(g153,g144) = 9
    c: DistanceY(g151,g134) = 9
    c: DistanceY(g148,g139) = 9
    c: DistanceY(g139,g147) = 9
    c: DistanceY(g129,g145) = 9
    c: Coincident(g145,g164)
    c: Vertical(g164)
    c: Coincident(g164,g165)
    c: Horizontal(g165)
    c: Coincident(g165,g166)
    c: Vertical(g166)
    c: Coincident(g166,g167)
    c: Horizontal(g167)
    c: Coincident(g167,g168)
    c: Vertical(g168)
    c: Coincident(g163,g168)
    c: DistanceX(g9,g145) = 9
    c: DistanceY(g166,g166) = 48.7
    c: DistanceY(g167,g19) = 10.4
    c: DistanceX(g14,g166) = 51.25
FEATURE [PartDesign::Pocket] Pocket001  label="PCB Pocket"
  BaseFeature = -> Pocket
  Direction = (0,0,-1)
  Length = 5
  Length2 = 5
  Profile = -> Sketch002
  ReferenceAxis = -> Sketch002 [N_Axis]
  Reversed = true
  Type = 1
FEATURE [Sketcher::SketchObject] Sketch003
  AttachmentOffset = pos=(0,0,4) rot=(0,0,1;0rad)
  FullyConstrained = true
  MapMode = 5
  Placement = pos=(0,0,4) rot=(0,0,1;0rad)
  Support = -> [XY_Plane]
  expr: Constraints[10] = Spreadsheet.sw_wi
  expr: Constraints[11] = Spreadsheet.sw_he
  expr: Constraints[23] = Spreadsheet.pl_spacing
  expr: Constraints[343] = Spreadsheet.pl_spacing
  expr: Constraints[344] = Spreadsheet.pl_spacing
  expr: Constraints[345] = Spreadsheet.pl_spacing
  expr: Constraints[346] = Spreadsheet.pl_spacing
  expr: Constraints[347] = Spreadsheet.pl_spacing
  expr: Constraints[348] = Spreadsheet.pl_sp4
  expr: Constraints[349] = Spreadsheet.pl_sp4
  expr: Constraints[350] = Spreadsheet.pl_sp2
  expr: Constraints[351] = Spreadsheet.pl_spacing
  expr: Constraints[352] = Spreadsheet.pl_spacing
  expr: Constraints[353] = Spreadsheet.pl_spacing
  expr: Constraints[354] = Spreadsheet.pl_spacing
  expr: Constraints[355] = Spreadsheet.pl_spacing
  expr: Constraints[356] = Spreadsheet.pl_spacing
  expr: Constraints[357] = Spreadsheet.pl_spacing
  expr: Constraints[358] = Spreadsheet.pl_spacing
  expr: Constraints[359] = Spreadsheet.pl_spacing
  expr: Constraints[360] = Spreadsheet.pl_spacing
  expr: Constraints[361] = Spreadsheet.pl_spacing
  expr: Constraints[362] = Spreadsheet.pl_spacing
  expr: Constraints[363] = Spreadsheet.pl_spacing
  expr: Constraints[364] = Spreadsheet.pl_spacing
  expr: Constraints[365] = Spreadsheet.pl_spacing
  expr: Constraints[366] = Spreadsheet.pl_spacing
  expr: Constraints[367] = Spreadsheet.pl_spacing
  expr: Constraints[368] = Spreadsheet.pl_spacing
  expr: Constraints[369] = Spreadsheet.pl_spacing
  expr: Constraints[370] = Spreadsheet.pl_spacing
  expr: Constraints[373] = Spreadsheet.pl_sp4
  expr: Constraints[375] = Spreadsheet.pl_sp4
  expr: Constraints[37] = Spreadsheet.pl_spacing
  expr: Constraints[413] = Spreadsheet.pl_plate
  expr: Constraints[414] = Spreadsheet.pl_plate
  expr: Constraints[415] = Spreadsheet.pl_plate
  expr: Constraints[416] = Spreadsheet.pl_plate
  expr: Constraints[417] = Spreadsheet.pl_plate
  expr: Constraints[418] = Spreadsheet.pl_plate
  expr: Constraints[419] = Spreadsheet.pl_plate
  expr: Constraints[420] = Spreadsheet.pl_plate
  expr: Constraints[421] = Spreadsheet.pl_plate
  expr: Constraints[422] = Spreadsheet.pl_plate
  expr: Constraints[423] = Spreadsheet.pl_plate
  expr: Constraints[424] = Spreadsheet.pl_plate
  expr: Constraints[425] = Spreadsheet.pl_plate
  expr: Constraints[426] = Spreadsheet.pl_plate
  expr: Constraints[427] = Spreadsheet.pl_plate
  expr: Constraints[428] = Spreadsheet.pl_plate
  expr: Constraints[429] = Spreadsheet.pl_plate
  expr: Constraints[430] = Spreadsheet.pl_plate
  expr: Constraints[431] = Spreadsheet.pl_plate
  expr: Constraints[432] = Spreadsheet.pl_plate
  expr: Constraints[444] = Spreadsheet.pl_plate
  expr: Constraints[50] = Spreadsheet.pl_spacing
  sketch-geometry (169):
    g0: LineSegment StartX=-7 StartY=7 StartZ=0 EndX=-7 EndY=-7 EndZ=0
    g1: LineSegment StartX=-7 StartY=-7 StartZ=0 EndX=7 EndY=-7 EndZ=0
    g2: LineSegment StartX=7 StartY=-7 StartZ=0 EndX=7 EndY=7 EndZ=0
    g3: LineSegment StartX=7 StartY=7 StartZ=0 EndX=-7 EndY=7 EndZ=0
    g4: GeomPoint X=0 Y=0 Z=0
    g5: LineSegment StartX=-7 StartY=-12 StartZ=0 EndX=-7 EndY=-26 EndZ=0
    g6: LineSegment StartX=-7 StartY=-26 StartZ=0 EndX=7 EndY=-26 EndZ=0
    g7: LineSegment StartX=7 StartY=-26 StartZ=0 EndX=7 EndY=-12 EndZ=0
    g8: LineSegment StartX=7 StartY=-12 StartZ=0 EndX=-7 EndY=-12 EndZ=0
    g9: GeomPoint X=0 Y=-19 Z=0
    g10: LineSegment StartX=-7 StartY=26 StartZ=0 EndX=-7 EndY=12 EndZ=0
    g11: LineSegment StartX=-7 StartY=12 StartZ=0 EndX=7 EndY=12 EndZ=0
    g12: LineSegment StartX=7 StartY=12 StartZ=0 EndX=7 EndY=26 EndZ=0
    g13: LineSegment StartX=7 StartY=26 StartZ=0 EndX=-7 EndY=26 EndZ=0
    g14: GeomPoint X=0 Y=19 Z=0
    g15: LineSegment StartX=-7 StartY=45 StartZ=0 EndX=-7 EndY=31 EndZ=0
    g16: LineSegment StartX=-7 StartY=31 StartZ=0 EndX=7 EndY=31 EndZ=0
    g17: LineSegment StartX=7 StartY=31 StartZ=0 EndX=7 EndY=45 EndZ=0
    g18: LineSegment StartX=7 StartY=45 StartZ=0 EndX=-7 EndY=45 EndZ=0
    g19: GeomPoint X=0 Y=38 Z=0
    g20: LineSegment StartX=-26 StartY=45 StartZ=0 EndX=-26 EndY=31 EndZ=0
    g21: LineSegment StartX=-26 StartY=31 StartZ=0 EndX=-12 EndY=31 EndZ=0
    g22: LineSegment StartX=-12 StartY=31 StartZ=0 EndX=-12 EndY=45 EndZ=0
    g23: LineSegment StartX=-12 StartY=45 StartZ=0 EndX=-26 EndY=45 EndZ=0
    g24: GeomPoint X=-19 Y=38 Z=0
    g25: LineSegment StartX=-26 StartY=26 StartZ=0 EndX=-26 EndY=12 EndZ=0
    g26: LineSegment StartX=-26 StartY=12 StartZ=0 EndX=-12 EndY=12 EndZ=0
    g27: LineSegment StartX=-12 StartY=12 StartZ=0 EndX=-12 EndY=26 EndZ=0
    g28: LineSegment StartX=-12 StartY=26 StartZ=0 EndX=-26 EndY=26 EndZ=0
    g29: GeomPoint X=-19 Y=19 Z=0
    g30: LineSegment StartX=-26 StartY=7 StartZ=0 EndX=-26 EndY=-7 EndZ=0
    g31: LineSegment StartX=-26 StartY=-7 StartZ=0 EndX=-12 EndY=-7 EndZ=0
    g32: LineSegment StartX=-12 StartY=-7 StartZ=0 EndX=-12 EndY=7 EndZ=0
    g33: LineSegment StartX=-12 StartY=7 StartZ=0 EndX=-26 EndY=7 EndZ=0
    g34: GeomPoint X=-19 Y=0 Z=0
    g35: LineSegment StartX=-26 StartY=-12 StartZ=0 EndX=-26 EndY=-26 EndZ=0
    g36: LineSegment StartX=-26 StartY=-26 StartZ=0 EndX=-12 EndY=-26 EndZ=0
    g37: LineSegment StartX=-12 StartY=-26 StartZ=0 EndX=-12 EndY=-12 EndZ=0
    g38: LineSegment StartX=-12 StartY=-12 StartZ=0 EndX=-26 EndY=-12 EndZ=0
    g39: GeomPoint X=-19 Y=-19 Z=0
    g40: LineSegment StartX=-45 StartY=49.75 StartZ=0 EndX=-45 EndY=35.75 EndZ=0
    g41: LineSegment StartX=-45 StartY=35.75 StartZ=0 EndX=-31 EndY=35.75 EndZ=0
    g42: LineSegment StartX=-31 StartY=35.75 StartZ=0 EndX=-31 EndY=49.75 EndZ=0
    g43: LineSegment StartX=-31 StartY=49.75 StartZ=0 EndX=-45 EndY=49.75 EndZ=0
    g44: GeomPoint X=-38 Y=42.75 Z=0
    g45: LineSegment StartX=-45 StartY=30.75 StartZ=0 EndX=-45 EndY=16.75 EndZ=0
    g46: LineSegment StartX=-45 StartY=16.75 StartZ=0 EndX=-31 EndY=16.75 EndZ=0
    g47: LineSegment StartX=-31 StartY=16.75 StartZ=0 EndX=-31 EndY=30.75 EndZ=0
    g48: LineSegment StartX=-31 StartY=30.75 StartZ=0 EndX=-45 EndY=30.75 EndZ=0
    g49: GeomPoint X=-38 Y=23.75 Z=0
    g50: LineSegment StartX=-45 StartY=11.75 StartZ=0 EndX=-45 EndY=-2.25 EndZ=0
    g51: LineSegment StartX=-45 StartY=-2.25 StartZ=0 EndX=-31 EndY=-2.25 EndZ=0
    g52: LineSegment StartX=-31 StartY=-2.25 StartZ=0 EndX=-31 EndY=11.75 EndZ=0
    g53: LineSegment StartX=-31 StartY=11.75 StartZ=0 EndX=-45 EndY=11.75 EndZ=0
    g54: GeomPoint X=-38 Y=4.75 Z=0
    g55: LineSegment StartX=-45 StartY=-7.25 StartZ=0 EndX=-45 EndY=-21.25 EndZ=0
    g56: LineSegment StartX=-45 StartY=-21.25 StartZ=0 EndX=-31 EndY=-21.25 EndZ=0
    g57: LineSegment StartX=-31 StartY=-21.25 StartZ=0 EndX=-31 EndY=-7.25 EndZ=0
    g58: LineSegment StartX=-31 StartY=-7.25 StartZ=0 EndX=-45 EndY=-7.25 EndZ=0
    g59: GeomPoint X=-38 Y=-14.25 Z=0
    g60: LineSegment StartX=-64 StartY=45 StartZ=0 EndX=-64 EndY=31 EndZ=0
    g61: LineSegment StartX=-64 StartY=31 StartZ=0 EndX=-50 EndY=31 EndZ=0
    g62: LineSegment StartX=-50 StartY=31 StartZ=0 EndX=-50 EndY=45 EndZ=0
    g63: LineSegment StartX=-50 StartY=45 StartZ=0 EndX=-64 EndY=45 EndZ=0
    g64: GeomPoint X=-57 Y=38 Z=0
    g65: LineSegment StartX=-64 StartY=26 StartZ=0 EndX=-64 EndY=12 EndZ=0
    g66: LineSegment StartX=-64 StartY=12 StartZ=0 EndX=-50 EndY=12 EndZ=0
    g67: LineSegment StartX=-50 StartY=12 StartZ=0 EndX=-50 EndY=26 EndZ=0
    g68: LineSegment StartX=-50 StartY=26 StartZ=0 EndX=-64 EndY=26 EndZ=0
    g69: GeomPoint X=-57 Y=19 Z=0
    g70: LineSegment StartX=-64 StartY=7 StartZ=0 EndX=-64 EndY=-7 EndZ=0
    g71: LineSegment StartX=-64 StartY=-7 StartZ=0 EndX=-50 EndY=-7 EndZ=0
    g72: LineSegment StartX=-50 StartY=-7 StartZ=0 EndX=-50 EndY=7 EndZ=0
    g73: LineSegment StartX=-50 StartY=7 StartZ=0 EndX=-64 EndY=7 EndZ=0
    g74: GeomPoint X=-57 Y=0 Z=0
    g75: LineSegment StartX=-64 StartY=-12 StartZ=0 EndX=-64 EndY=-26 EndZ=0
    g76: LineSegment StartX=-64 StartY=-26 StartZ=0 EndX=-50 EndY=-26 EndZ=0
    g77: LineSegment StartX=-50 StartY=-26 StartZ=0 EndX=-50 EndY=-12 EndZ=0
    g78: LineSegment StartX=-50 StartY=-12 StartZ=0 EndX=-64 EndY=-12 EndZ=0
    g79: GeomPoint X=-57 Y=-19 Z=0
    g80: LineSegment StartX=-83 StartY=30.75 StartZ=0 EndX=-83 EndY=16.75 EndZ=0
    g81: LineSegment StartX=-83 StartY=16.75 StartZ=0 EndX=-69 EndY=16.75 EndZ=0
    g82: LineSegment StartX=-69 StartY=16.75 StartZ=0 EndX=-69 EndY=30.75 EndZ=0
    g83: LineSegment StartX=-69 StartY=30.75 StartZ=0 EndX=-83 EndY=30.75 EndZ=0
    g84: GeomPoint X=-76 Y=23.75 Z=0
    g85: LineSegment StartX=-102 StartY=30.75 StartZ=0 EndX=-102 EndY=16.75 EndZ=0
    g86: LineSegment StartX=-102 StartY=16.75 StartZ=0 EndX=-88 EndY=16.75 EndZ=0
    g87: LineSegment StartX=-88 StartY=16.75 StartZ=0 EndX=-88 EndY=30.75 EndZ=0
    g88: LineSegment StartX=-88 StartY=30.75 StartZ=0 EndX=-102 EndY=30.75 EndZ=0
    g89: GeomPoint X=-95 Y=23.75 Z=0
    g90: LineSegment StartX=-83 StartY=11.75 StartZ=0 EndX=-83 EndY=-2.25 EndZ=0
    g91: LineSegment StartX=-83 StartY=-2.25 StartZ=0 EndX=-69 EndY=-2.25 EndZ=0
    g92: LineSegment StartX=-69 StartY=-2.25 StartZ=0 EndX=-69 EndY=11.75 EndZ=0
    g93: LineSegment StartX=-69 StartY=11.75 StartZ=0 EndX=-83 EndY=11.75 EndZ=0
    g94: GeomPoint X=-76 Y=4.75 Z=0
    g95: LineSegment StartX=-83 StartY=-7.25 StartZ=0 EndX=-83 EndY=-21.25 EndZ=0
    g96: LineSegment StartX=-83 StartY=-21.25 StartZ=0 EndX=-69 EndY=-21.25 EndZ=0
    g97: LineSegment StartX=-69 StartY=-21.25 StartZ=0 EndX=-69 EndY=-7.25 EndZ=0
    g98: LineSegment StartX=-69 StartY=-7.25 StartZ=0 EndX=-83 EndY=-7.25 EndZ=0
    g99: GeomPoint X=-76 Y=-14.25 Z=0
    g100: LineSegment StartX=-83 StartY=-26.25 StartZ=0 EndX=-83 EndY=-40.25 EndZ=0
    g101: LineSegment StartX=-83 StartY=-40.25 StartZ=0 EndX=-69 EndY=-40.25 EndZ=0
    g102: LineSegment StartX=-69 StartY=-40.25 StartZ=0 EndX=-69 EndY=-26.25 EndZ=0
    g103: LineSegment StartX=-69 StartY=-26.25 StartZ=0 EndX=-83 EndY=-26.25 EndZ=0
    g104: GeomPoint X=-76 Y=-33.25 Z=0
    g105: LineSegment StartX=-102 StartY=11.75 StartZ=0 EndX=-102 EndY=-2.25 EndZ=0
    g106: LineSegment StartX=-102 StartY=-2.25 StartZ=0 EndX=-88 EndY=-2.25 EndZ=0
    g107: LineSegment StartX=-88 StartY=-2.25 StartZ=0 EndX=-88 EndY=11.75 EndZ=0
    g108: LineSegment StartX=-88 StartY=11.75 StartZ=0 EndX=-102 EndY=11.75 EndZ=0
    g109: GeomPoint X=-95 Y=4.75 Z=0
    g110: LineSegment StartX=-102 StartY=-7.25 StartZ=0 EndX=-102 EndY=-21.25 EndZ=0
    g111: LineSegment StartX=-102 StartY=-21.25 StartZ=0 EndX=-88 EndY=-21.25 EndZ=0
    g112: LineSegment StartX=-88 StartY=-21.25 StartZ=0 EndX=-88 EndY=-7.25 EndZ=0
    g113: LineSegment StartX=-88 StartY=-7.25 StartZ=0 EndX=-102 EndY=-7.25 EndZ=0
    g114: GeomPoint X=-95 Y=-14.25 Z=0
    g115: LineSegment StartX=-102 StartY=-26.25 StartZ=0 EndX=-102 EndY=-40.25 EndZ=0
    g116: LineSegment StartX=-102 StartY=-40.25 StartZ=0 EndX=-88 EndY=-40.25 EndZ=0
    g117: LineSegment StartX=-88 StartY=-40.25 StartZ=0 EndX=-88 EndY=-26.25 EndZ=0
    g118: LineSegment StartX=-88 StartY=-26.25 StartZ=0 EndX=-102 EndY=-26.25 EndZ=0
    g119: GeomPoint X=-95 Y=-33.25 Z=0
    g120: LineSegment StartX=-16.5 StartY=-31 StartZ=0 EndX=-16.5 EndY=-45 EndZ=0
    g121: LineSegment StartX=-16.5 StartY=-45 StartZ=0 EndX=-2.5 EndY=-45 EndZ=0
    g122: LineSegment StartX=-2.5 StartY=-45 StartZ=0 EndX=-2.5 EndY=-31 EndZ=0
    g123: LineSegment StartX=-2.5 StartY=-31 StartZ=0 EndX=-16.5 EndY=-31 EndZ=0
    g124: GeomPoint X=-9.5 Y=-38 Z=0
    g125: LineSegment StartX=2.5 StartY=-31 StartZ=0 EndX=2.5 EndY=-45 EndZ=0
    g126: LineSegment StartX=2.5 StartY=-45 StartZ=0 EndX=16.5 EndY=-45 EndZ=0
    g127: LineSegment StartX=16.5 StartY=-45 StartZ=0 EndX=16.5 EndY=-31 EndZ=0
    g128: LineSegment StartX=16.5 StartY=-31 StartZ=0 EndX=2.5 EndY=-31 EndZ=0
    g129: GeomPoint X=9.5 Y=-38 Z=0
    g130: LineSegment StartX=-35.5 StartY=-31 StartZ=0 EndX=-35.5 EndY=-45 EndZ=0
    g131: LineSegment StartX=-35.5 StartY=-45 StartZ=0 EndX=-21.5 EndY=-45 EndZ=0
    g132: LineSegment StartX=-21.5 StartY=-45 StartZ=0 EndX=-21.5 EndY=-31 EndZ=0
    g133: LineSegment StartX=-21.5 StartY=-31 StartZ=0 EndX=-35.5 EndY=-31 EndZ=0
    g134: GeomPoint X=-28.5 Y=-38 Z=0
    g135: LineSegment StartX=21.5 StartY=-35.75 StartZ=0 EndX=21.5 EndY=-49.75 EndZ=0
    g136: LineSegment StartX=21.5 StartY=-49.75 StartZ=0 EndX=35.5 EndY=-49.75 EndZ=0
    g137: LineSegment StartX=35.5 StartY=-49.75 StartZ=0 EndX=35.5 EndY=-35.75 EndZ=0
    g138: LineSegment StartX=35.5 StartY=-35.75 StartZ=0 EndX=21.5 EndY=-35.75 EndZ=0
    g139: GeomPoint X=28.5 Y=-42.75 Z=0
    g140: LineSegment StartX=-54.5 StartY=-35.75 StartZ=0 EndX=-54.5 EndY=-49.75 EndZ=0
    g141: LineSegment StartX=-54.5 StartY=-49.75 StartZ=0 EndX=-40.5 EndY=-49.75 EndZ=0
    g142: LineSegment StartX=-40.5 StartY=-49.75 StartZ=0 EndX=-40.5 EndY=-35.75 EndZ=0
    g143: LineSegment StartX=-40.5 StartY=-35.75 StartZ=0 EndX=-54.5 EndY=-35.75 EndZ=0
    g144: GeomPoint X=-47.5 Y=-42.75 Z=0
    g145: LineSegment StartX=13 StartY=-25 StartZ=0 EndX=22.5 EndY=-25 EndZ=0
    g146: LineSegment StartX=22.5 StartY=-25 StartZ=0 EndX=22.5 EndY=-29.75 EndZ=0
    g147: LineSegment StartX=22.5 StartY=-29.75 StartZ=0 EndX=41.5 EndY=-29.75 EndZ=0
    g148: LineSegment StartX=41.5 StartY=-29.75 StartZ=0 EndX=41.5 EndY=-55.75 EndZ=0
    g149: LineSegment StartX=41.5 StartY=-55.75 StartZ=0 EndX=15.5 EndY=-55.75 EndZ=0
    g150: LineSegment StartX=15.5 StartY=-55.75 StartZ=0 EndX=15.5 EndY=-51 EndZ=0
    g151: LineSegment StartX=15.5 StartY=-51 StartZ=0 EndX=-34.5 EndY=-51 EndZ=0
    g152: LineSegment StartX=-34.5 StartY=-51 StartZ=0 EndX=-34.5 EndY=-55.75 EndZ=0
    g153: LineSegment StartX=-34.5 StartY=-55.75 StartZ=0 EndX=-60.5 EndY=-55.75 EndZ=0
    g154: LineSegment StartX=-60.5 StartY=-55.75 StartZ=0 EndX=-60.5 EndY=-46.25 EndZ=0
    g155: LineSegment StartX=-60.5 StartY=-46.25 StartZ=0 EndX=-108 EndY=-46.25 EndZ=0
    g156: LineSegment StartX=-108 StartY=-46.25 StartZ=0 EndX=-108 EndY=36.75 EndZ=0
    g157: LineSegment StartX=-108 StartY=36.75 StartZ=0 EndX=-70 EndY=36.75 EndZ=0
    g158: LineSegment StartX=-70 StartY=36.75 StartZ=0 EndX=-70 EndY=51 EndZ=0
    g159: LineSegment StartX=-70 StartY=51 StartZ=0 EndX=-51 EndY=51 EndZ=0
    g160: LineSegment StartX=-51 StartY=51 StartZ=0 EndX=-51 EndY=55.75 EndZ=0
    g161: LineSegment StartX=-51 StartY=55.75 StartZ=0 EndX=-25 EndY=55.75 EndZ=0
    g162: LineSegment StartX=-25 StartY=55.75 StartZ=0 EndX=-25 EndY=51 EndZ=0
    g163: LineSegment StartX=-25 StartY=51 StartZ=0 EndX=13 EndY=51 EndZ=0
    g164: LineSegment StartX=13 StartY=-25 StartZ=0 EndX=13 EndY=-21.1 EndZ=0
    g165: LineSegment StartX=13 StartY=-21.1 StartZ=0 EndX=50.8 EndY=-21.1 EndZ=0
    g166: LineSegment StartX=50.8 StartY=-21.1 StartZ=0 EndX=50.8 EndY=27.6 EndZ=0
    g167: LineSegment StartX=50.8 StartY=27.6 StartZ=0 EndX=13 EndY=27.6 EndZ=0
    g168: LineSegment StartX=13 StartY=27.6 StartZ=0 EndX=13 EndY=51 EndZ=0
  constraints (448):
    c: Coincident(g0,g1)
    c: Coincident(g1,g2)
    c: Coincident(g2,g3)
    c: Coincident(g3,g0)
    c: Horizontal(g1)
    c: Horizontal(g3)
    c: Vertical(g0)
    c: Vertical(g2)
    c: Symmetric(g1,g0,g4)
    c: Coincident(g4,g-1)
    c: DistanceX(g3,g3) = 14
    c: DistanceY(g0,g0) = 14
    c: Coincident(g5,g6)
    c: Coincident(g6,g7)
    c: Coincident(g7,g8)
    c: Coincident(g8,g5)
    c: Horizontal(g6)
    c: Horizontal(g8)
    c: Vertical(g5)
    c: Vertical(g7)
    c: Symmetric(g6,g5,g9)
    c: Equal(g3,g8) = 14.15
    c: Equal(g0,g5) = 14.15
    c: DistanceY(g9,g4) = 19
    c: Vertical(g9,g4)
    c: Coincident(g10,g11)
    c: Coincident(g11,g12)
    c: Coincident(g12,g13)
    c: Coincident(g13,g10)
    c: Horizontal(g11)
    c: Horizontal(g13)
    c: Vertical(g10)
    c: Vertical(g12)
    c: Symmetric(g11,g10,g14)
    c: Equal(g3,g13) = 14.15
    c: Equal(g0,g10) = 14.15
    c: Vertical(g4,g14)
    c: DistanceY(g4,g14) = 19
    c: Coincident(g15,g16)
    c: Coincident(g16,g17)
    c: Coincident(g17,g18)
    c: Coincident(g18,g15)
    c: Horizontal(g16)
    c: Horizontal(g18)
    c: Vertical(g15)
    c: Vertical(g17)
    c: Symmetric(g16,g15,g19)
    c: Equal(g3,g18) = 14.15
    c: Equal(g0,g15) = 14.15
    c: Vertical(g19,g4)
    c: DistanceY(g14,g19) = 19
    c: Coincident(g20,g21)
    c: Coincident(g21,g22)
    c: Coincident(g22,g23)
    c: Coincident(g23,g20)
    c: Horizontal(g21)
    c: Horizontal(g23)
    c: Vertical(g20)
    c: Vertical(g22)
    c: Symmetric(g21,g20,g24)
    c: Equal(g3,g23) = 14.15
    c: Equal(g0,g20) = 14.15
    c: Coincident(g25,g26)
    c: Coincident(g26,g27)
    c: Coincident(g27,g28)
    c: Coincident(g28,g25)
    c: Horizontal(g26)
    c: Horizontal(g28)
    c: Vertical(g25)
    c: Vertical(g27)
    c: Symmetric(g26,g25,g29)
    c: Equal(g3,g28) = 14.15
    c: Equal(g0,g25) = 14.15
    c: Coincident(g30,g31)
    c: Coincident(g31,g32)
    c: Coincident(g32,g33)
    c: Coincident(g33,g30)
    c: Horizontal(g31)
    c: Horizontal(g33)
    c: Vertical(g30)
    c: Vertical(g32)
    c: Symmetric(g31,g30,g34)
    c: Equal(g3,g33) = 14.15
    c: Equal(g0,g30) = 14.15
    c: Coincident(g35,g36)
    c: Coincident(g36,g37)
    c: Coincident(g37,g38)
    c: Coincident(g38,g35)
    c: Horizontal(g36)
    c: Horizontal(g38)
    c: Vertical(g35)
    c: Vertical(g37)
    c: Symmetric(g36,g35,g39)
    c: Equal(g3,g38) = 14.15
    c: Equal(g0,g35) = 14.15
    c: Coincident(g40,g41)
    c: Coincident(g41,g42)
    c: Coincident(g42,g43)
    c: Coincident(g43,g40)
    c: Horizontal(g41)
    c: Horizontal(g43)
    c: Vertical(g40)
    c: Vertical(g42)
    c: Symmetric(g41,g40,g44)
    c: Equal(g3,g43) = 14.15
    c: Equal(g0,g40) = 14.15
    c: Coincident(g45,g46)
    c: Coincident(g46,g47)
    c: Coincident(g47,g48)
    c: Coincident(g48,g45)
    c: Horizontal(g46)
    c: Horizontal(g48)
    c: Vertical(g45)
    c: Vertical(g47)
    c: Symmetric(g46,g45,g49)
    c: Equal(g3,g48) = 14.15
    c: Equal(g0,g45) = 14.15
    c: Coincident(g50,g51)
    c: Coincident(g51,g52)
    c: Coincident(g52,g53)
    c: Coincident(g53,g50)
    c: Horizontal(g51)
    c: Horizontal(g53)
    c: Vertical(g50)
    c: Vertical(g52)
    c: Symmetric(g51,g50,g54)
    c: Equal(g3,g53) = 14.15
    c: Equal(g0,g50) = 14.15
    c: Coincident(g55,g56)
    c: Coincident(g56,g57)
    c: Coincident(g57,g58)
    c: Coincident(g58,g55)
    c: Horizontal(g56)
    c: Horizontal(g58)
    c: Vertical(g55)
    c: Vertical(g57)
    c: Symmetric(g56,g55,g59)
    c: Equal(g3,g58) = 14.15
    c: Equal(g0,g55) = 14.15
    c: Coincident(g60,g61)
    c: Coincident(g61,g62)
    c: Coincident(g62,g63)
    c: Coincident(g63,g60)
    c: Horizontal(g61)
    c: Horizontal(g63)
    c: Vertical(g60)
    c: Vertical(g62)
    c: Symmetric(g61,g60,g64)
    c: Equal(g3,g63) = 14.15
    c: Equal(g0,g60) = 14.15
    c: Coincident(g65,g66)
    c: Coincident(g66,g67)
    c: Coincident(g67,g68)
    c: Coincident(g68,g65)
    c: Horizontal(g66)
    c: Horizontal(g68)
    c: Vertical(g65)
    c: Vertical(g67)
    c: Symmetric(g66,g65,g69)
    c: Equal(g3,g68) = 14.15
    c: Equal(g0,g65) = 14.15
    c: Coincident(g70,g71)
    c: Coincident(g71,g72)
    c: Coincident(g72,g73)
    c: Coincident(g73,g70)
    c: Horizontal(g71)
    c: Horizontal(g73)
    c: Vertical(g70)
    c: Vertical(g72)
    c: Symmetric(g71,g70,g74)
    c: Equal(g3,g73) = 14.15
    c: Equal(g0,g70) = 14.15
    c: Coincident(g75,g76)
    c: Coincident(g76,g77)
    c: Coincident(g77,g78)
    c: Coincident(g78,g75)
    c: Horizontal(g76)
    c: Horizontal(g78)
    c: Vertical(g75)
    c: Vertical(g77)
    c: Symmetric(g76,g75,g79)
    c: Equal(g3,g78) = 14.15
    c: Equal(g0,g75) = 14.15
    c: Coincident(g80,g81)
    c: Coincident(g81,g82)
    c: Coincident(g82,g83)
    c: Coincident(g83,g80)
    c: Horizontal(g81)
    c: Horizontal(g83)
    c: Vertical(g80)
    c: Vertical(g82)
    c: Symmetric(g81,g80,g84)
    c: Equal(g3,g83) = 14.15
    c: Equal(g0,g80) = 14.15
    c: Coincident(g85,g86)
    c: Coincident(g86,g87)
    c: Coincident(g87,g88)
    c: Coincident(g88,g85)
    c: Horizontal(g86)
    c: Horizontal(g88)
    c: Vertical(g85)
    c: Vertical(g87)
    c: Symmetric(g86,g85,g89)
    c: Equal(g3,g88) = 14.15
    c: Equal(g0,g85) = 14.15
    c: Coincident(g90,g91)
    c: Coincident(g91,g92)
    c: Coincident(g92,g93)
    c: Coincident(g93,g90)
    c: Horizontal(g91)
    c: Horizontal(g93)
    c: Vertical(g90)
    c: Vertical(g92)
    c: Symmetric(g91,g90,g94)
    c: Equal(g3,g93) = 14.15
    c: Equal(g0,g90) = 14.15
    c: Coincident(g95,g96)
    c: Coincident(g96,g97)
    c: Coincident(g97,g98)
    c: Coincident(g98,g95)
    c: Horizontal(g96)
    c: Horizontal(g98)
    c: Vertical(g95)
    c: Vertical(g97)
    c: Symmetric(g96,g95,g99)
    c: Equal(g3,g98) = 14.15
    c: Equal(g0,g95) = 14.15
    c: Coincident(g100,g101)
    c: Coincident(g101,g102)
    c: Coincident(g102,g103)
    c: Coincident(g103,g100)
    c: Horizontal(g101)
    c: Horizontal(g103)
    c: Vertical(g100)
    c: Vertical(g102)
    c: Symmetric(g101,g100,g104)
    c: Equal(g3,g103) = 14.15
    c: Equal(g0,g100) = 14.15
    c: Coincident(g105,g106)
    c: Coincident(g106,g107)
    c: Coincident(g107,g108)
    c: Coincident(g108,g105)
    c: Horizontal(g106)
    c: Horizontal(g108)
    c: Vertical(g105)
    c: Vertical(g107)
    c: Symmetric(g106,g105,g109)
    c: Equal(g3,g108) = 14.15
    c: Equal(g0,g105) = 14.15
    c: Coincident(g110,g111)
    c: Coincident(g111,g112)
    c: Coincident(g112,g113)
    c: Coincident(g113,g110)
    c: Horizontal(g111)
    c: Horizontal(g113)
    c: Vertical(g110)
    c: Vertical(g112)
    c: Symmetric(g111,g110,g114)
    c: Equal(g3,g113) = 14.15
    c: Equal(g0,g110) = 14.15
    c: Coincident(g115,g116)
    c: Coincident(g116,g117)
    c: Coincident(g117,g118)
    c: Coincident(g118,g115)
    c: Horizontal(g116)
    c: Horizontal(g118)
    c: Vertical(g115)
    c: Vertical(g117)
    c: Symmetric(g116,g115,g119)
    c: Equal(g3,g118) = 14.15
    c: Equal(g0,g115) = 14.15
    c: Coincident(g120,g121)
    c: Coincident(g121,g122)
    c: Coincident(g122,g123)
    c: Coincident(g123,g120)
    c: Horizontal(g121)
    c: Horizontal(g123)
    c: Vertical(g120)
    c: Vertical(g122)
    c: Symmetric(g121,g120,g124)
    c: Equal(g3,g123) = 14.15
    c: Equal(g0,g120) = 14.15
    c: Coincident(g125,g126)
    c: Coincident(g126,g127)
    c: Coincident(g127,g128)
    c: Coincident(g128,g125)
    c: Horizontal(g126)
    c: Horizontal(g128)
    c: Vertical(g125)
    c: Vertical(g127)
    c: Symmetric(g126,g125,g129)
    c: Equal(g3,g128) = 14.15
    c: Equal(g0,g125) = 14.15
    c: Coincident(g130,g131)
    c: Coincident(g131,g132)
    c: Coincident(g132,g133)
    c: Coincident(g133,g130)
    c: Horizontal(g131)
    c: Horizontal(g133)
    c: Vertical(g130)
    c: Vertical(g132)
    c: Symmetric(g131,g130,g134)
    c: Equal(g3,g133) = 14.15
    c: Equal(g0,g130) = 14.15
    c: Coincident(g135,g136)
    c: Coincident(g136,g137)
    c: Coincident(g137,g138)
    c: Coincident(g138,g135)
    c: Horizontal(g136)
    c: Horizontal(g138)
    c: Vertical(g135)
    c: Vertical(g137)
    c: Symmetric(g136,g135,g139)
    c: Equal(g3,g138) = 14.15
    c: Equal(g0,g135) = 14.15
    c: Coincident(g140,g141)
    c: Coincident(g141,g142)
    c: Coincident(g142,g143)
    c: Coincident(g143,g140)
    c: Horizontal(g141)
    c: Horizontal(g143)
    c: Vertical(g140)
    c: Vertical(g142)
    c: Symmetric(g141,g140,g144)
    c: Equal(g3,g143) = 14.15
    c: Equal(g0,g140) = 14.15
    c: Vertical(g39,g34)
    c: Vertical(g34,g29)
    c: Vertical(g29,g24)
    c: Vertical(g59,g54)
    c: Vertical(g54,g49)
    c: Vertical(g49,g44)
    c: Vertical(g79,g74)
    c: Vertical(g74,g69)
    c: Vertical(g69,g64)
    c: Vertical(g104,g99)
    c: Vertical(g99,g94)
    c: Vertical(g94,g84)
    c: Vertical(g119,g114)
    c: Vertical(g114,g109)
    c: Vertical(g109,g89)
    c: Horizontal(g134,g124)
    c: Horizontal(g124,g129)
    c: DistanceY(g129,g9) = 19
    c: DistanceX(g129,g139) = 19
    c: DistanceX(g124,g129) = 19
    c: DistanceX(g134,g124) = 19
    c: DistanceX(g144,g134) = 19
    c: DistanceY(g139,g129) = 4.75
    c: DistanceY(g144,g134) = 4.75
    c: DistanceX(g9,g129) = 9.5
    c: DistanceY(g39,g34) = 19
    c: DistanceY(g34,g29) = 19
    c: DistanceY(g29,g24) = 19
    c: DistanceY(g59,g54) = 19
    c: DistanceY(g54,g49) = 19
    c: DistanceY(g49,g44) = 19
    c: DistanceY(g79,g74) = 19
    c: DistanceY(g74,g69) = 19
    c: DistanceY(g69,g64) = 19
    c: DistanceY(g104,g99) = 19
    c: DistanceY(g99,g94) = 19
    c: DistanceY(g94,g84) = 19
    c: DistanceY(g119,g114) = 19
    c: DistanceY(g114,g109) = 19
    c: DistanceY(g109,g89) = 19
    c: DistanceX(g34,g4) = 19
    c: DistanceX(g54,g34) = 19
    c: DistanceX(g74,g54) = 19
    c: DistanceX(g99,g74) = 19
    c: DistanceX(g114,g99) = 19
    c: Horizontal(g34,g4)
    c: Horizontal(g74,g34)
    c: DistanceY(g34,g54) = 4.75
    c: Horizontal(g114,g99)
    c: DistanceY(g74,g94) = 4.75
    c: Horizontal(g145)
    c: Coincident(g145,g146)
    c: Vertical(g146)
    c: Coincident(g146,g147)
    c: Horizontal(g147)
    c: Coincident(g147,g148)
    c: Vertical(g148)
    c: Coincident(g148,g149)
    c: Horizontal(g149)
    c: Coincident(g149,g150)
    c: Vertical(g150)
    c: Coincident(g150,g151)
    c: Horizontal(g151)
    c: Coincident(g151,g152)
    c: Vertical(g152)
    c: Coincident(g152,g153)
    c: Horizontal(g153)
    c: Coincident(g153,g154)
    c: Vertical(g154)
    c: Coincident(g154,g155)
    c: Horizontal(g155)
    c: Coincident(g155,g156)
    c: Vertical(g156)
    c: Coincident(g156,g157)
    c: Horizontal(g157)
    c: Coincident(g157,g158)
    c: Vertical(g158)
    c: Coincident(g158,g159)
    c: Horizontal(g159)
    c: Coincident(g159,g160)
    c: Vertical(g160)
    c: Coincident(g160,g161)
    c: Horizontal(g161)
    c: Coincident(g161,g162)
    c: Vertical(g162)
    c: Coincident(g162,g163)
    c: Horizontal(g163)
    c: DistanceX(g19,g163) = 13
    c: DistanceX(g44,g161) = 13
    c: DistanceX(g160,g44) = 13
    c: DistanceX(g158,g64) = 13
    c: DistanceX(g156,g89) = 13
    c: DistanceX(g153,g144) = 13
    c: DistanceX(g144,g152) = 13
    c: DistanceX(g149,g139) = 13
    c: DistanceX(g139,g148) = 13
    c: DistanceX(g129,g145) = 13
    c: DistanceY(g19,g163) = 13
    c: DistanceY(g44,g161) = 13
    c: DistanceY(g64,g158) = 13
    c: DistanceY(g89,g156) = 13
    c: DistanceY(g155,g119) = 13
    c: DistanceY(g153,g144) = 13
    c: DistanceY(g151,g134) = 13
    c: DistanceY(g148,g139) = 13
    c: DistanceY(g139,g147) = 13
    c: DistanceY(g129,g145) = 13
    c: Coincident(g145,g164)
    c: Vertical(g164)
    c: Coincident(g164,g165)
    c: Horizontal(g165)
    c: Coincident(g165,g166)
    c: Vertical(g166)
    c: Coincident(g166,g167)
    c: Horizontal(g167)
    c: Coincident(g167,g168)
    c: Vertical(g168)
    c: Coincident(g163,g168)
    c: DistanceX(g9,g145) = 13
    c: DistanceY(g166,g166) = 48.7
    c: DistanceY(g167,g19) = 10.4
    c: DistanceX(g14,g166) = 50.8
FEATURE [PartDesign::Pocket] Pocket002  label="Backplate Pocket"
  BaseFeature = -> Pocket001
  Direction = (0,0,-1)
  Length = 5
  Length2 = 5
  Profile = -> Sketch003
  ReferenceAxis = -> Sketch003 [N_Axis]
  Refine = true
  Reversed = true
  Type = 1
FEATURE [Sketcher::SketchObject] Sketch004
  ExternalGeometry = -> [Pocket002]
  FullyConstrained = true
  MapMode = 5
  Placement = pos=(0,0,6.4) rot=(0,0,1;0rad)
  Support = -> [Pocket002]
  sketch-geometry (4):
    g0: LineSegment StartX=52.75 StartY=57.25 StartZ=0 EndX=15.75 EndY=57.25 EndZ=0
    g1: LineSegment StartX=15.75 StartY=57.25 StartZ=0 EndX=15.75 EndY=29.5 EndZ=0
    g2: LineSegment StartX=15.75 StartY=29.5 StartZ=0 EndX=52.75 EndY=29.5 EndZ=0
    g3: LineSegment StartX=52.75 StartY=29.5 StartZ=0 EndX=52.75 EndY=57.25 EndZ=0
  constraints (11):
    c: Coincident(g0,g1)
    c: Coincident(g1,g2)
    c: Coincident(g2,g3)
    c: Coincident(g3,g0)
    c: Horizontal(g0)
    c: Horizontal(g2)
    c: Vertical(g1)
    c: Vertical(g3)
    c: Coincident(g0,g-3)
    c: DistanceY(g1,g1) = 27.75
    c: DistanceX(g0,g0) = 37
FEATURE [PartDesign::Pocket] Pocket003  label="Cable Pocket"
  BaseFeature = -> Pocket002
  Direction = (0,0,-1)
  Length = 2.4
  Length2 = 5
  Profile = -> Sketch004
  ReferenceAxis = -> Sketch004 [N_Axis]
  Type = 0
FEATURE [PartDesign::Pocket] Pocket004
  BaseFeature = -> Pocket003
  Direction = (0,-1,0)
  Length = 0.5
  Length2 = 5
  Profile = -> Pocket003 [Face6]
  Type = 0
FEATURE [PartDesign::Pad] Pad001
  BaseFeature = -> Pocket004
  Direction = (1,0,0)
  Length = 2.75
  Length2 = 10
  Profile = -> Pocket004 [Face2]
  Refine = true
  Type = 0
FEATURE [Sketcher::SketchObject] Sketch005
  ExternalGeometry = -> [Pad001]
  FullyConstrained = true
  MapMode = 5
  Placement = pos=(0,0,6.4) rot=(0,0,1;0rad)
  Support = -> [Pad001]
  expr: Constraints[0] = Spreadsheet.hole_dia
  expr: Constraints[12] = Spreadsheet.hole_ext
  expr: Constraints[13] = Spreadsheet.hole_ext
  expr: Constraints[14] = Spreadsheet.hole_int
  expr: Constraints[15] = Spreadsheet.hole_int
  expr: Constraints[16] = Spreadsheet.hole_int
  expr: Constraints[1] = Spreadsheet.hole_ext
  expr: Constraints[7] = Spreadsheet.hole_dia
  sketch-geometry (6):
    g0: Circle CenterX=-9.5 CenterY=-52.4 CenterZ=0 NormalX=0 NormalY=0 NormalZ=1 AngleXU=0 Radius=1.4
    g1: Circle CenterX=-85.5 CenterY=-47.65 CenterZ=0 NormalX=0 NormalY=0 NormalZ=1 AngleXU=0 Radius=1.4
    g2: Circle CenterX=-109.4 CenterY=-4.75 CenterZ=0 NormalX=0 NormalY=0 NormalZ=1 AngleXU=0 Radius=1.4
    g3: Circle CenterX=-85.5 CenterY=38.15 CenterZ=0 NormalX=0 NormalY=0 NormalZ=1 AngleXU=0 Radius=1.4
    g4: Circle CenterX=-9.5 CenterY=52.4 CenterZ=0 NormalX=0 NormalY=0 NormalZ=1 AngleXU=0 Radius=1.4
    g5: Circle CenterX=29 CenterY=-28.35 CenterZ=0 NormalX=0 NormalY=0 NormalZ=1 AngleXU=0 Radius=1.4
  constraints (15):
    c: Diameter(g0) = 2.8
    c: DistanceY(g-4,g0) = 4.85
    c: DistanceX(g0,g-1) = 9.5
    c: Equal(g5, g1-g4) x4
    c: Diameter(g5) = 2.8
    c: DistanceX(g4,g-1) = 9.5
    c: DistanceX(g3,g-1) = 85.5
    c: DistanceX(g1,g-1) = 85.5
    c: DistanceY(g2,g-1) = 4.75
    c: DistanceX(g-8,g2) = 4.85
    c: DistanceY(g4,g-8) = 4.85
    c: DistanceY(g-6,g3) = 1.4
    c: DistanceY(g1,g-7) = 1.4
    c: DistanceY(g-9,g5) = 1.4
    c: DistanceX(g-1,g5) = 29
FEATURE [PartDesign::Pocket] Pocket005
  BaseFeature = -> Pad001
  Direction = (0,0,-1)
  Length = 5
  Length2 = 5
  Profile = -> Sketch005
  ReferenceAxis = -> Sketch005 [N_Axis]
  Type = 1
FEATURE [PartDesign::Fillet] Fillet  label="PCB internal Fillet"
  Base = -> Pocket005 [Edge315,Edge311,Edge305,Edge87,Edge137,Edge298,Edge300,Edge304,Edge306,Edge312]
  BaseFeature = -> Pocket005
  Radius = 0.5
  SupportTransform = false
  UseAllEdges = false
FEATURE [PartDesign::Fillet] Fillet002  label="PCB external Fillet"
  Base = -> Fillet [Edge290,Edge292,Edge291,Edge283,Edge277,Edge265,Edge271,Edge273,Edge274,Edge282,Edge284,Edge285]
  BaseFeature = -> Fillet
  Radius = 1.5
  SupportTransform = false
  UseAllEdges = false
FEATURE [Sketcher::SketchObject] Sketch006
  ExternalGeometry = -> [Fillet002]
  FullyConstrained = false
  MapMode = 5
  Placement = pos=(0,0,4) rot=(0,0,1;0rad)
  Support = -> [Fillet002]
  sketch-geometry (7):
    g0: Circle CenterX=-85.656 CenterY=-42.25 CenterZ=0 NormalX=0 NormalY=0 NormalZ=1 AngleXU=0 Radius=0.5
    g1: Circle CenterX=-104 CenterY=-4.58107 CenterZ=0 NormalX=0 NormalY=0 NormalZ=1 AngleXU=0 Radius=0.5
    g2: Circle CenterX=-85.2942 CenterY=32.75 CenterZ=0 NormalX=0 NormalY=0 NormalZ=1 AngleXU=0 Radius=0.5
    g3: Circle CenterX=-9.71042 CenterY=47 CenterZ=0 NormalX=0 NormalY=0 NormalZ=1 AngleXU=0 Radius=0.5
    g4: Circle CenterX=-9.85211 CenterY=-47 CenterZ=0 NormalX=0 NormalY=0 NormalZ=1 AngleXU=0 Radius=0.5
    g5: Circle CenterX=9 CenterY=37.5326 CenterZ=0 NormalX=0 NormalY=0 NormalZ=1 AngleXU=0 Radius=0.5
    g6: Circle CenterX=37.5 CenterY=-42.8288 CenterZ=0 NormalX=0 NormalY=0 NormalZ=1 AngleXU=0 Radius=0.5
  constraints (11):
    c: PointOnObject(g0,g-5)
    c: PointOnObject(g1,g-3)
    c: PointOnObject(g2,g-4)
    c: PointOnObject(g3,g-6)
    c: PointOnObject(g4,g-7)
    c: PointOnObject(g5,g-8)
    c: PointOnObject(g6,g-9)
    c: Equal(g6,g4)
    c: Equal(g6, g0-g3) x4
    c: Equal(g6,g5)
    c: Diameter(g6) = 1
FEATURE [PartDesign::Pad] Pad002  label="PCB push fit tabs"
  BaseFeature = -> Fillet002
  Direction = (0,0,1)
  Length = 1
  Length2 = 10
  Profile = -> Sketch006
  ReferenceAxis = -> Sketch006 [N_Axis]
  Refine = true
  Reversed = true
  Type = 0
FEATURE [Sketcher::SketchObject] Sketch007
  ExternalGeometry = -> [Pad002]
  FullyConstrained = true
  MapMode = 5
  Placement = pos=(0,0,6.4) rot=(0,0,1;0rad)
  Support = -> [Pad002]
  expr: Constraints[48] = Spreadsheet.hole_dia
  expr: Constraints[49] = Spreadsheet.hole_dia
  expr: Constraints[50] = Spreadsheet.hole_dia
  expr: Constraints[51] = Spreadsheet.hole_dia
  expr: Constraints[52] = Spreadsheet.hole_dia
  expr: Constraints[53] = Spreadsheet.hole_dia
  sketch-geometry (24):
    g0: LineSegment StartX=-109.4 StartY=-3.35 StartZ=0 EndX=-107.4 EndY=-3.35 EndZ=0
    g1: LineSegment StartX=-107.4 StartY=-3.35 StartZ=0 EndX=-107.4 EndY=-6.15 EndZ=0
    g2: LineSegment StartX=-107.4 StartY=-6.15 StartZ=0 EndX=-109.4 EndY=-6.15 EndZ=0
    g3: LineSegment StartX=-109.4 StartY=-6.15 StartZ=0 EndX=-109.4 EndY=-3.35 EndZ=0
    g4: LineSegment StartX=-86.9 StartY=-45.65 StartZ=0 EndX=-84.1 EndY=-45.65 EndZ=0
    g5: LineSegment StartX=-84.1 StartY=-45.65 StartZ=0 EndX=-84.1 EndY=-47.65 EndZ=0
    g6: LineSegment StartX=-84.1 StartY=-47.65 StartZ=0 EndX=-86.9 EndY=-47.65 EndZ=0
    g7: LineSegment StartX=-86.9 StartY=-47.65 StartZ=0 EndX=-86.9 EndY=-45.65 EndZ=0
    g8: LineSegment StartX=-10.9 StartY=-52.4 StartZ=0 EndX=-8.1 EndY=-52.4 EndZ=0
    g9: LineSegment StartX=-8.1 StartY=-52.4 StartZ=0 EndX=-8.1 EndY=-50.4 EndZ=0
    g10: LineSegment StartX=-8.1 StartY=-50.4 StartZ=0 EndX=-10.9 EndY=-50.4 EndZ=0
    g11: LineSegment StartX=-10.9 StartY=-50.4 StartZ=0 EndX=-10.9 EndY=-52.4 EndZ=0
    g12: LineSegment StartX=27.6 StartY=-28.35 StartZ=0 EndX=30.4 EndY=-28.35 EndZ=0
    g13: LineSegment StartX=30.4 StartY=-28.35 StartZ=0 EndX=30.4 EndY=-30.35 EndZ=0
    g14: LineSegment StartX=30.4 StartY=-30.35 StartZ=0 EndX=27.6 EndY=-30.35 EndZ=0
    g15: LineSegment StartX=27.6 StartY=-30.35 StartZ=0 EndX=27.6 EndY=-28.35 EndZ=0
    g16: LineSegment StartX=-10.9 StartY=52.4 StartZ=0 EndX=-8.1 EndY=52.4 EndZ=0
    g17: LineSegment StartX=-8.1 StartY=52.4 StartZ=0 EndX=-8.1 EndY=50.4 EndZ=0
    g18: LineSegment StartX=-8.1 StartY=50.4 StartZ=0 EndX=-10.9 EndY=50.4 EndZ=0
    g19: LineSegment StartX=-10.9 StartY=50.4 StartZ=0 EndX=-10.9 EndY=52.4 EndZ=0
    g20: LineSegment StartX=-86.9 StartY=36.15 StartZ=0 EndX=-84.1 EndY=36.15 EndZ=0
    g21: LineSegment StartX=-84.1 StartY=36.15 StartZ=0 EndX=-84.1 EndY=38.15 EndZ=0
    g22: LineSegment StartX=-84.1 StartY=38.15 StartZ=0 EndX=-86.9 EndY=38.15 EndZ=0
    g23: LineSegment StartX=-86.9 StartY=38.15 StartZ=0 EndX=-86.9 EndY=36.15 EndZ=0
  constraints (66):
    c: Coincident(g0,g1)
    c: Coincident(g1,g2)
    c: Coincident(g2,g3)
    c: Coincident(g3,g0)
    c: Horizontal(g0)
    c: Horizontal(g2)
    c: Vertical(g1)
    c: Vertical(g3)
    c: Coincident(g4,g5)
    c: Coincident(g5,g6)
    c: Coincident(g6,g7)
    c: Coincident(g7,g4)
    c: Horizontal(g4)
    c: Horizontal(g6)
    c: Vertical(g5)
    c: Vertical(g7)
    c: Coincident(g8,g9)
    c: Coincident(g9,g10)
    c: Coincident(g10,g11)
    c: Coincident(g11,g8)
    c: Horizontal(g8)
    c: Horizontal(g10)
    c: Vertical(g9)
    c: Vertical(g11)
    c: Coincident(g12,g13)
    c: Coincident(g13,g14)
    c: Coincident(g14,g15)
    c: Coincident(g15,g12)
    c: Horizontal(g12)
    c: Horizontal(g14)
    c: Vertical(g13)
    c: Vertical(g15)
    c: Coincident(g16,g17)
    c: Coincident(g17,g18)
    c: Coincident(g18,g19)
    c: Coincident(g19,g16)
    c: Horizontal(g16)
    c: Horizontal(g18)
    c: Vertical(g17)
    c: Vertical(g19)
    c: Coincident(g20,g21)
    c: Coincident(g21,g22)
    c: Coincident(g22,g23)
    c: Coincident(g23,g20)
    c: Horizontal(g20)
    c: Horizontal(g22)
    c: Vertical(g21)
    c: Vertical(g23)
    c: DistanceX(g22,g22) = 2.8
    c: DistanceX(g16,g16) = 2.8
    c: DistanceY(g3,g3) = 2.8
    c: DistanceX(g4,g4) = 2.8
    c: DistanceX(g10,g10) = 2.8
    c: DistanceX(g12,g12) = 2.8
    c: Symmetric(g12,g12,g-6)
    c: Symmetric(g8,g8,g-5)
    c: Symmetric(g6,g5,g-4)
    c: Symmetric(g2,g0,g-3)
    c: Symmetric(g22,g21,g-8)
    c: Symmetric(g16,g16,g-7)
    c: DistanceY(g23,g23) = 2
    c: DistanceY(g19,g19) = 2
    c: DistanceY(g15,g15) = 2
    c: DistanceY(g11,g11) = 2
    c: DistanceY(g7,g7) = 2
    c: DistanceX(g0,g0) = 2
FEATURE [PartDesign::Pocket] Pocket006  label="Hole fix Pocket"
  BaseFeature = -> Pad002
  Direction = (0,0,-1)
  Length = 2.4
  Length2 = 5
  Profile = -> Sketch007
  ReferenceAxis = -> Sketch007 [N_Axis]
  Refine = true
  Type = 0
FEATURE [PartDesign::Fillet] Fillet003  label="Hole fix Fillet"
  Base = -> Pocket006 [Edge622,Edge625,Edge627,Edge630,Edge642,Edge644,Edge595,Edge598,Edge606,Edge609,Edge617,Edge620]
  BaseFeature = -> Pocket006
  Radius = 1
  SupportTransform = false
  UseAllEdges = false
FEATURE [PartDesign::Fillet] Fillet004  label="Mid Plate Internal Fillet"
  Base = -> Fillet003 [Edge153,Edge164,Edge176,Edge178,Edge170,Edge124,Edge90,Edge78]
  BaseFeature = -> Fillet003
  Radius = 1.5
  SupportTransform = false
  UseAllEdges = false
FEATURE [PartDesign::Fillet] Fillet005  label="Mid Plate External Fillet"
  Base = -> Fillet004 [Edge138,Edge180,Edge192,Edge196,Edge222,Edge190,Edge148,Edge144,Edge140,Edge83,Edge87,Edge104]
  BaseFeature = -> Fillet004
  Radius = 2.5
  SupportTransform = false
  UseAllEdges = false
FEATURE [PartDesign::Fillet] Fillet006
  Base = -> Fillet005 [Edge279,Edge269]
  BaseFeature = -> Fillet005
  Radius = 4
  SupportTransform = false
  UseAllEdges = false
FEATURE [PartDesign::Fillet] Fillet007
  Base = -> Fillet006 [Edge95]
  BaseFeature = -> Fillet006
  Radius = 2
  SupportTransform = false
  UseAllEdges = false
FEATURE [Sketcher::SketchObject] Sketch008
  ExternalGeometry = -> [Fillet007]
  FullyConstrained = true
  MapMode = 5
  Placement = pos=(0,0,4) rot=(0,0,1;0rad)
  Support = -> [Fillet007]
  sketch-geometry (5):
    g0: ArcOfCircle CenterX=11.75 CenterY=53.25 CenterZ=0 NormalX=0 NormalY=0 NormalZ=1 AngleXU=0 Radius=4 StartAngle=0.968945 EndAngle=1.5708
    g1: ArcOfCircle CenterX=53.5 CenterY=27 CenterZ=0 NormalX=0 NormalY=0 NormalZ=1 AngleXU=0 Radius=2 StartAngle=8e-16 EndAngle=0.968945
    g2: LineSegment StartX=14.0147 StartY=56.5472 StartZ=0 EndX=54.6323 EndY=28.6486 EndZ=0
    g3: LineSegment StartX=55.5 StartY=27 StartZ=0 EndX=55.5 EndY=57.25 EndZ=0
    g4: LineSegment StartX=11.75 StartY=57.25 StartZ=0 EndX=55.5 EndY=57.25 EndZ=0
  constraints (10):
    c: Coincident(g0,g-3)
    c: Coincident(g0,g-3)
    c: Coincident(g1,g-4)
    c: Coincident(g1,g-4)
    c: Tangent(g2,g0) = 1.5708
    c: Tangent(g2,g1) = 1.5708
    c: Coincident(g3,g1)
    c: Coincident(g4,g0)
    c: Coincident(g4,g3)
    c: Coincident(g-5,g3)
FEATURE [PartDesign::Pocket] Pocket007
  BaseFeature = -> Fillet007
  Direction = (0,0,-1)
  Length = 5
  Length2 = 5
  Profile = -> Sketch008
  ReferenceAxis = -> Sketch008 [N_Axis]
  Type = 1
FEATURE [Sketcher::SketchObject] Sketch009
  ExternalGeometry = -> [Pocket007]
  FullyConstrained = true
  MapMode = 5
  Placement = pos=(0,0,6.4) rot=(0,0,1;0rad)
  Support = -> [Pocket007]
  sketch-geometry (10):
    g0: LineSegment StartX=-72.25 StartY=57.25 StartZ=0 EndX=-114.25 EndY=57.25 EndZ=0
    g1: LineSegment StartX=-114.25 StartY=57.25 StartZ=0 EndX=-114.25 EndY=39 EndZ=0
    g2: LineSegment StartX=55.5 StartY=-26.35 StartZ=0 EndX=55.5 EndY=-57.25 EndZ=0
    g3: LineSegment StartX=55.5 StartY=-57.25 StartZ=0 EndX=43.75 EndY=-57.25 EndZ=0
    g4: ArcOfCircle CenterX=43.75 CenterY=-53.25 CenterZ=0 NormalX=0 NormalY=0 NormalZ=1 AngleXU=0 Radius=4 StartAngle=4.71239 EndAngle=6.00268
    g5: ArcOfCircle CenterX=51.5 CenterY=-26.35 CenterZ=0 NormalX=0 NormalY=0 NormalZ=1 AngleXU=0 Radius=4 StartAngle=6.00268 EndAngle=6.28319
    g6: LineSegment StartX=55.3437 StartY=-27.4574 StartZ=0 EndX=47.5937 EndY=-54.3574 EndZ=0
    g7: ArcOfCircle CenterX=-110.25 CenterY=39 CenterZ=0 NormalX=0 NormalY=0 NormalZ=1 AngleXU=0 Radius=4 StartAngle=1.92957 EndAngle=3.14159
    g8: ArcOfCircle CenterX=-72.25 CenterY=53.25 CenterZ=0 NormalX=0 NormalY=0 NormalZ=1 AngleXU=0 Radius=4 StartAngle=1.5708 EndAngle=1.92957
    g9: LineSegment StartX=-111.654 StartY=42.7453 StartZ=0 EndX=-73.6545 EndY=56.9953 EndZ=0
  constraints (28):
    c: Coincident(g1,g0)
    c: Coincident(g3,g2)
    c: Coincident(g2,g-3)
    c: Vertical(g2)
    c: Horizontal(g3)
    c: Horizontal(g0)
    c: Vertical(g1)
    c: Coincident(g0,g-4)
    c: Coincident(g5,g2)
    c: Coincident(g4,g3)
    c: Vertical(g4,g3)
    c: Horizontal(g5,g2)
    c: Tangent(g6,g5) = 1.5708
    c: Tangent(g6,g4) = 1.5708
    c: DistanceY(g3,g4) = 4
    c: DistanceX(g5,g2) = 4
    c: DistanceX(g4,g2) = 11.75
    c: DistanceY(g2,g5) = 30.9
    c: Coincident(g7,g1)
    c: Coincident(g8,g0)
    c: DistanceY(g8,g0) = 4
    c: Vertical(g0,g8)
    c: DistanceX(g1,g7) = 4
    c: Horizontal(g7,g1)
    c: Tangent(g9,g7) = 1.5708
    c: Tangent(g9,g8) = 1.5708
    c: DistanceY(g7,g0) = 18.25
    c: DistanceX(g0,g8) = 42
FEATURE [PartDesign::Pocket] Pocket008
  BaseFeature = -> Pocket007
  Direction = (0,0,-1)
  Length = 5
  Length2 = 5
  Profile = -> Sketch009
  ReferenceAxis = -> Sketch009 [N_Axis]
  Type = 1
FEATURE [Sketcher::SketchObject] Sketch010
  ExternalGeometry = -> [Pocket008]
  FullyConstrained = true
  MapMode = 5
  Placement = pos=(0,0,0) rot=(1,0,0;3.14159rad)
  Support = -> [Pocket008]
  expr: Constraints[114] = Spreadsheet.hexnut
  expr: Constraints[115] = Spreadsheet.hexnut
  expr: Constraints[116] = Spreadsheet.hexnut
  expr: Constraints[117] = Spreadsheet.hexnut
  expr: Constraints[118] = Spreadsheet.hexnut
  expr: Constraints[119] = Spreadsheet.hexnut
  sketch-geometry (42):
    g0: LineSegment StartX=-84.0278 StartY=45.1 StartZ=0 EndX=-82.5555 EndY=47.65 EndZ=0
    g1: LineSegment StartX=-82.5555 StartY=47.65 StartZ=0 EndX=-84.0278 EndY=50.2 EndZ=0
    g2: LineSegment StartX=-84.0278 StartY=50.2 StartZ=0 EndX=-86.9722 EndY=50.2 EndZ=0
    g3: LineSegment StartX=-86.9722 StartY=50.2 StartZ=0 EndX=-88.4445 EndY=47.65 EndZ=0
    g4: LineSegment StartX=-88.4445 StartY=47.65 StartZ=0 EndX=-86.9722 EndY=45.1 EndZ=0
    g5: LineSegment StartX=-86.9722 StartY=45.1 StartZ=0 EndX=-84.0278 EndY=45.1 EndZ=0
    g6: Circle CenterX=-85.5 CenterY=47.65 CenterZ=0 NormalX=0 NormalY=0 NormalZ=1 AngleXU=0 Radius=2.94449
    g7: LineSegment StartX=-8.02776 StartY=49.85 StartZ=0 EndX=-6.55551 EndY=52.4 EndZ=0
    g8: LineSegment StartX=-6.55551 StartY=52.4 StartZ=0 EndX=-8.02776 EndY=54.95 EndZ=0
    g9: LineSegment StartX=-8.02776 StartY=54.95 StartZ=0 EndX=-10.9722 EndY=54.95 EndZ=0
    g10: LineSegment StartX=-10.9722 StartY=54.95 StartZ=0 EndX=-12.4445 EndY=52.4 EndZ=0
    g11: LineSegment StartX=-12.4445 StartY=52.4 StartZ=0 EndX=-10.9722 EndY=49.85 EndZ=0
    g12: LineSegment StartX=-10.9722 StartY=49.85 StartZ=0 EndX=-8.02776 EndY=49.85 EndZ=0
    g13: Circle CenterX=-9.5 CenterY=52.4 CenterZ=0 NormalX=0 NormalY=0 NormalZ=1 AngleXU=0 Radius=2.94449
    g14: LineSegment StartX=30.4722 StartY=25.8 StartZ=0 EndX=31.9445 EndY=28.35 EndZ=0
    g15: LineSegment StartX=31.9445 StartY=28.35 StartZ=0 EndX=30.4722 EndY=30.9 EndZ=0
    g16: LineSegment StartX=30.4722 StartY=30.9 StartZ=0 EndX=27.5278 EndY=30.9 EndZ=0
    g17: LineSegment StartX=27.5278 StartY=30.9 StartZ=0 EndX=26.0555 EndY=28.35 EndZ=0
    g18: LineSegment StartX=26.0555 StartY=28.35 StartZ=0 EndX=27.5278 EndY=25.8 EndZ=0
    g19: LineSegment StartX=27.5278 StartY=25.8 StartZ=0 EndX=30.4722 EndY=25.8 EndZ=0
    g20: Circle CenterX=29 CenterY=28.35 CenterZ=0 NormalX=0 NormalY=0 NormalZ=1 AngleXU=0 Radius=2.94449
    g21: LineSegment StartX=-8.02776 StartY=-49.85 StartZ=0 EndX=-10.9722 EndY=-49.85 EndZ=0
    g22: LineSegment StartX=-10.9722 StartY=-49.85 StartZ=0 EndX=-12.4445 EndY=-52.4 EndZ=0
    g23: LineSegment StartX=-12.4445 StartY=-52.4 StartZ=0 EndX=-10.9722 EndY=-54.95 EndZ=0
    g24: LineSegment StartX=-10.9722 StartY=-54.95 StartZ=0 EndX=-8.02776 EndY=-54.95 EndZ=0
    g25: LineSegment StartX=-8.02776 StartY=-54.95 StartZ=0 EndX=-6.55551 EndY=-52.4 EndZ=0
    g26: LineSegment StartX=-6.55551 StartY=-52.4 StartZ=0 EndX=-8.02776 EndY=-49.85 EndZ=0
    g27: Circle CenterX=-9.5 CenterY=-52.4 CenterZ=0 NormalX=0 NormalY=0 NormalZ=1 AngleXU=0 Radius=2.94449
    g28: LineSegment StartX=-82.95 StartY=-36.6778 StartZ=0 EndX=-85.5 EndY=-35.2055 EndZ=0
    g29: LineSegment StartX=-85.5 StartY=-35.2055 StartZ=0 EndX=-88.05 EndY=-36.6778 EndZ=0
    g30: LineSegment StartX=-88.05 StartY=-36.6778 StartZ=0 EndX=-88.05 EndY=-39.6222 EndZ=0
    g31: LineSegment StartX=-88.05 StartY=-39.6222 StartZ=0 EndX=-85.5 EndY=-41.0945 EndZ=0
    g32: LineSegment StartX=-85.5 StartY=-41.0945 StartZ=0 EndX=-82.95 EndY=-39.6222 EndZ=0
    g33: LineSegment StartX=-82.95 StartY=-39.6222 StartZ=0 EndX=-82.95 EndY=-36.6778 EndZ=0
    g34: Circle CenterX=-85.5 CenterY=-38.15 CenterZ=0 NormalX=0 NormalY=0 NormalZ=1 AngleXU=0 Radius=2.94449
    g35: LineSegment StartX=-111.95 StartY=6.22224 StartZ=0 EndX=-111.95 EndY=3.27776 EndZ=0
    g36: LineSegment StartX=-111.95 StartY=3.27776 StartZ=0 EndX=-109.4 EndY=1.80551 EndZ=0
    g37: LineSegment StartX=-109.4 StartY=1.80551 StartZ=0 EndX=-106.85 EndY=3.27776 EndZ=0
    g38: LineSegment StartX=-106.85 StartY=3.27776 StartZ=0 EndX=-106.85 EndY=6.22224 EndZ=0
    g39: LineSegment StartX=-106.85 StartY=6.22224 StartZ=0 EndX=-109.4 EndY=7.69449 EndZ=0
    g40: LineSegment StartX=-109.4 StartY=7.69449 StartZ=0 EndX=-111.95 EndY=6.22224 EndZ=0
    g41: Circle CenterX=-109.4 CenterY=4.75 CenterZ=0 NormalX=0 NormalY=0 NormalZ=1 AngleXU=0 Radius=2.94449
  constraints (96):
    c: Coincident(g0,g1)
    c: Coincident(g1,g2)
    c: Coincident(g2,g3)
    c: Coincident(g3,g4)
    c: Coincident(g4,g5)
    c: Coincident(g5,g0)
    c: Equal(g0, g1-g5) x5
    c: PointOnObject(g0,g6)
    c: PointOnObject(g1,g6)
    c: PointOnObject(g2,g6)
    c: PointOnObject(g3,g6)
    c: PointOnObject(g4,g6)
    c: PointOnObject(g5,g6)
    c: Coincident(g6,g-3)
    c: Coincident(g7,g8)
    c: Coincident(g8,g9)
    c: Coincident(g9,g10)
    c: Coincident(g10,g11)
    c: Coincident(g11,g12)
    c: Coincident(g12,g7)
    c: Equal(g7, g8-g12) x5
    c: PointOnObject(g7,g13)
    c: PointOnObject(g8,g13)
    c: PointOnObject(g9,g13)
    c: PointOnObject(g10,g13)
    c: PointOnObject(g11,g13)
    c: PointOnObject(g12,g13)
    c: Coincident(g13,g-7)
    c: Coincident(g14,g15)
    c: Coincident(g15,g16)
    c: Coincident(g16,g17)
    c: Coincident(g17,g18)
    c: Coincident(g18,g19)
    c: Coincident(g19,g14)
    c: Equal(g14, g15-g19) x5
    c: PointOnObject(g14,g20)
    c: PointOnObject(g15,g20)
    c: PointOnObject(g16,g20)
    c: PointOnObject(g17,g20)
    c: PointOnObject(g18,g20)
    c: PointOnObject(g19,g20)
    c: Coincident(g20,g-8)
    c: Coincident(g21,g22)
    c: Coincident(g22,g23)
    c: Coincident(g23,g24)
    c: Coincident(g24,g25)
    c: Coincident(g25,g26)
    c: Coincident(g26,g21)
    c: Equal(g21, g22-g26) x5
    c: PointOnObject(g21,g27)
    c: PointOnObject(g22,g27)
    c: PointOnObject(g23,g27)
    c: PointOnObject(g24,g27)
    c: PointOnObject(g25,g27)
    c: PointOnObject(g26,g27)
    c: Coincident(g27,g-6)
    c: Coincident(g28,g29)
    c: Coincident(g29,g30)
    c: Coincident(g30,g31)
    c: Coincident(g31,g32)
    c: Coincident(g32,g33)
    c: Coincident(g33,g28)
    c: Equal(g28, g29-g33) x5
    c: PointOnObject(g28,g34)
    c: PointOnObject(g29,g34)
    c: PointOnObject(g30,g34)
    c: PointOnObject(g31,g34)
    c: PointOnObject(g32,g34)
    c: PointOnObject(g33,g34)
    c: Coincident(g34,g-5)
    c: Coincident(g35,g36)
    c: Coincident(g36,g37)
    c: Coincident(g37,g38)
    c: Coincident(g38,g39)
    c: Coincident(g39,g40)
    c: Coincident(g40,g35)
    c: Equal(g35, g36-g40) x5
    c: PointOnObject(g35,g41)
    c: PointOnObject(g36,g41)
    c: PointOnObject(g37,g41)
    c: PointOnObject(g38,g41)
    c: PointOnObject(g39,g41)
    c: PointOnObject(g40,g41)
    c: Coincident(g41,g-4)
    c: Horizontal(g2)
    c: Horizontal(g9)
    c: Horizontal(g16)
    c: Vertical(g35)
    c: Vertical(g30)
    c: Horizontal(g21)
    c: DistanceY(g4,g2) = 5.1
    c: DistanceY(g11,g9) = 5.1
    c: DistanceY(g18,g16) = 5.1
    c: DistanceY(g23,g21) = 5.1
    c: DistanceX(g29,g28) = 5.1
    c: DistanceX(g35,g38) = 5.1
FEATURE [PartDesign::Pocket] Pocket009
  BaseFeature = -> Pocket008
  Direction = (0,0,1)
  Length = 3
  Length2 = 5
  Profile = -> Sketch010
  ReferenceAxis = -> Sketch010 [N_Axis]
  Type = 0
FEATURE [PartDesign::Chamfer] Chamfer
  Angle = 45
  Base = -> Pocket009 [Edge106]
  BaseFeature = -> Pocket009
  ChamferType = 0
  FlipDirection = false
  Size = 1
  Size2 = 1
  SupportTransform = false
  UseAllEdges = false
FEATURE [PartDesign::Plane] DatumPlane
  Length = 211.437
  MapMode = 7
  Placement = pos=(14.0147,56.5472,4) rot=(-0.348786,0.662702,0.662702;3.81278rad)
  ResizeMode = 0
  Support = -> [Chamfer]
  Width = 69.5882
FEATURE [Sketcher::SketchObject] Sketch011
  ExternalGeometry = -> [Chamfer]
  FullyConstrained = true
  MapMode = 5
  Placement = pos=(14.0147,56.5472,4) rot=(-0.348786,0.662702,0.662702;3.81278rad)
  Support = -> [DatumPlane]
  sketch-geometry (3):
    g0: LineSegment StartX=7.1e-15 StartY=0 StartZ=0 EndX=7.1e-15 EndY=-1 EndZ=0
    g1: LineSegment StartX=7.1e-15 StartY=-1 StartZ=0 EndX=1 EndY=-1e-16 EndZ=0
    g2: LineSegment StartX=1 StartY=0 StartZ=0 EndX=7.1e-15 EndY=0 EndZ=0
  constraints (8):
    c: Coincident(g0,g-3)
    c: Vertical(g0)
    c: Coincident(g1,g0)
    c: Coincident(g2,g0)
    c: Horizontal(g2)
    c: Coincident(g2,g1)
    c: DistanceY(g0,g0) = 1
    c: DistanceX(g2,g2) = 1
FEATURE [PartDesign::SubtractivePipe] SubtractivePipe
  AuxilleryCurvelinear = true
  AuxillerySpineTangent = false
  BaseFeature = -> Chamfer
  Binormal = (0,0,0)
  Mode = 0
  Profile = -> Sketch011
  Spine = -> Chamfer [Edge111]
  SpineTangent = false
  Transformation = 0
  Transition = 0
FEATURE [PartDesign::Pad] Pad003
  BaseFeature = -> SubtractivePipe
  Direction = (0,0,-1)
  Length = 1
  Length2 = 10
  Profile = -> SubtractivePipe [Face155,Face13]
  Refine = true
  Type = 0
FEATURE [Sketcher::SketchObject] Sketch012
  ExternalGeometry = -> [Pad003]
  FullyConstrained = true
  MapMode = 5
  Placement = pos=(0,0,3) rot=(1,0,0;3.14159rad)
  Support = -> [Pad003]
  expr: Constraints[11] = Spreadsheet.hole_dia
  sketch-geometry (6):
    g0: Circle CenterX=-85.5 CenterY=47.65 CenterZ=0 NormalX=0 NormalY=0 NormalZ=1 AngleXU=0 Radius=1.4
    g1: Circle CenterX=-109.4 CenterY=4.75 CenterZ=0 NormalX=0 NormalY=0 NormalZ=1 AngleXU=0 Radius=1.4
    g2: Circle CenterX=-85.5 CenterY=-38.15 CenterZ=0 NormalX=0 NormalY=0 NormalZ=1 AngleXU=0 Radius=1.4
    g3: Circle CenterX=-9.5 CenterY=-52.4 CenterZ=0 NormalX=0 NormalY=0 NormalZ=1 AngleXU=0 Radius=1.4
    g4: Circle CenterX=29 CenterY=28.35 CenterZ=0 NormalX=0 NormalY=0 NormalZ=1 AngleXU=0 Radius=1.4
    g5: Circle CenterX=-9.5 CenterY=52.4 CenterZ=0 NormalX=0 NormalY=0 NormalZ=1 AngleXU=0 Radius=1.4
  constraints (12):
    c: Coincident(g0,g-8)
    c: Coincident(g1,g-3)
    c: Coincident(g2,g-4)
    c: Coincident(g3,g-5)
    c: Coincident(g4,g-6)
    c: Coincident(g5,g-7)
    c: Equal(g0,g5)
    c: Equal(g0,g4)
    c: Equal(g0,g3)
    c: Equal(g0,g2)
    c: Equal(g0,g1)
    c: Diameter(g0) = 2.8
FEATURE [PartDesign::Pad] Pad004
  BaseFeature = -> Pad003
  Direction = (0,0,-1)
  Length = 0.15
  Length2 = 10
  Profile = -> Sketch012
  ReferenceAxis = -> Sketch012 [N_Axis]
  Refine = true
  Reversed = true
  Type = 0
FEATURE [Sketcher::SketchObject] Sketch013
  ExternalGeometry = -> [Pad004]
  FullyConstrained = true
  MapMode = 5
  Placement = pos=(0,0,3) rot=(0,0,1;0rad)
  Support = -> [Pad004]
  sketch-geometry (16):
    g0: LineSegment StartX=14 StartY=3.6 StartZ=0 EndX=33 EndY=3.6 EndZ=0
    g1: LineSegment StartX=33 StartY=3.6 StartZ=0 EndX=33 EndY=10.3 EndZ=0
    g2: LineSegment StartX=33 StartY=10.3 StartZ=0 EndX=51.25 EndY=10.3 EndZ=0
    g3: LineSegment StartX=51.25 StartY=10.3 StartZ=0 EndX=51.25 EndY=15.3 EndZ=0
    g4: LineSegment StartX=51.25 StartY=15.3 StartZ=0 EndX=33 EndY=15.3 EndZ=0
    g5: LineSegment StartX=33 StartY=15.3 StartZ=0 EndX=33 EndY=27.6 EndZ=0
    g6: LineSegment StartX=33 StartY=27.6 StartZ=0 EndX=29 EndY=27.6 EndZ=0
    g7: LineSegment StartX=18 StartY=27.6 StartZ=0 EndX=18 EndY=7.6 EndZ=0
    g8: LineSegment StartX=18 StartY=7.6 StartZ=0 EndX=29 EndY=7.6 EndZ=0
    g9: LineSegment StartX=29 StartY=7.6 StartZ=0 EndX=29 EndY=27.6 EndZ=0
    g10: LineSegment StartX=18 StartY=27.6 StartZ=0 EndX=14 EndY=27.6 EndZ=0
    g11: LineSegment StartX=14 StartY=27.6 StartZ=0 EndX=14 EndY=3.6 EndZ=0
    g12: LineSegment StartX=36.65 StartY=-18.1 StartZ=0 EndX=47.65 EndY=-18.1 EndZ=0
    g13: LineSegment StartX=47.65 StartY=-18.1 StartZ=0 EndX=47.65 EndY=-21.1 EndZ=0
    g14: LineSegment StartX=47.65 StartY=-21.1 StartZ=0 EndX=36.65 EndY=-21.1 EndZ=0
    g15: LineSegment StartX=36.65 StartY=-21.1 StartZ=0 EndX=36.65 EndY=-18.1 EndZ=0
  constraints (49):
    c: Horizontal(g0)
    c: Coincident(g1,g0)
    c: Vertical(g1)
    c: Coincident(g2,g1)
    c: PointOnObject(g2,g-4)
    c: Horizontal(g2)
    c: Coincident(g3,g2)
    c: PointOnObject(g3,g-4)
    c: Coincident(g4,g3)
    c: Horizontal(g4)
    c: Coincident(g5,g4)
    c: PointOnObject(g5,g-3)
    c: Coincident(g6,g5)
    c: PointOnObject(g6,g-3)
    c: PointOnObject(g7,g-3)
    c: Vertical(g7)
    c: Coincident(g8,g7)
    c: Horizontal(g8)
    c: Coincident(g9,g8)
    c: Coincident(g9,g6)
    c: Vertical(g9)
    c: Vertical(g5)
    c: DistanceY(g0,g-5) = 24
    c: DistanceX(g0,g0) = 19
    c: Vertical(g4,g1)
    c: DistanceY(g5,g5) = 12.3
    c: DistanceY(g3,g3) = 5
    c: DistanceY(g7,g7) = 20
    c: DistanceX(g8,g8) = 11
    c: DistanceX(g2,g2) = 18.25
    c: Coincident(g10,g7)
    c: PointOnObject(g10,g-3)
    c: Coincident(g11,g10)
    c: Coincident(g11,g0)
    c: DistanceX(g-5,g10) = 1
    c: DistanceX(g10,g10) = 4
    c: Vertical(g11)
    c: Coincident(g12,g13)
    c: Coincident(g13,g14)
    c: Coincident(g14,g15)
    c: Coincident(g15,g12)
    c: Horizontal(g12)
    c: Horizontal(g14)
    c: Vertical(g13)
    c: Vertical(g15)
    c: DistanceX(g12,g12) = 11
    c: DistanceY(g15,g15) = 3
    c: DistanceX(g13,g-6) = 3.6
    c: DistanceY(g-6,g13) = 0
FEATURE [PartDesign::Pocket] Pocket010  label="Pin clearance Pocket"
  BaseFeature = -> Pad004
  Direction = (0,0,-1)
  Length = 2
  Length2 = 5
  Profile = -> Sketch013
  ReferenceAxis = -> Sketch013 [N_Axis]
  Refine = true
  Type = 0
FEATURE [Sketcher::SketchObject] Sketch014
  ExternalGeometry = -> [Pocket010]
  FullyConstrained = true
  MapMode = 5
  Placement = pos=(0,0,0) rot=(1,0,0;3.14159rad)
  Support = -> [Pocket010]
  sketch-geometry (8):
    g0: Circle CenterX=47.5 CenterY=-23.8421 CenterZ=0 NormalX=0 NormalY=0 NormalZ=1 AngleXU=0 Radius=4.25
    g1: Circle CenterX=11.1293 CenterY=-51.25 CenterZ=0 NormalX=0 NormalY=0 NormalZ=1 AngleXU=0 Radius=3.25
    g2: Circle CenterX=-71.706 CenterY=-50.25 CenterZ=0 NormalX=0 NormalY=0 NormalZ=1 AngleXU=0 Radius=3.25
    g3: Circle CenterX=-107.25 CenterY=-36.921 CenterZ=0 NormalX=0 NormalY=0 NormalZ=1 AngleXU=0 Radius=3.25
    g4: Circle CenterX=-106.25 CenterY=49.25 CenterZ=0 NormalX=0 NormalY=0 NormalZ=1 AngleXU=0 Radius=4.25
    g5: Circle CenterX=42.2449 CenterY=51.25 CenterZ=0 NormalX=0 NormalY=0 NormalZ=1 AngleXU=0 Radius=3.25
    g6: Circle CenterX=46.8331 CenterY=28.1 CenterZ=0 NormalX=0 NormalY=0 NormalZ=1 AngleXU=0 Radius=4.25
    g7: Circle CenterX=-66.25 CenterY=49.25 CenterZ=0 NormalX=0 NormalY=0 NormalZ=1 AngleXU=0 Radius=4.25
  constraints (24):
    c: Equal(g6,g7)
    c: Equal(g6,g4)
    c: Equal(g6,g0)
    c: Diameter(g6) = 8.5
    c: Equal(g5,g1)
    c: Equal(g5,g2)
    c: Equal(g5,g3)
    c: Diameter(g5) = 6.5
    c: Distance(g5,g-50) = 5
    c: Distance(g5,g-44) = 5
    c: Distance(g7,g-44) = 7
    c: Distance(g4,g-44) = 7
    c: Distance(g4,g-45) = 7
    c: DistanceX(g4,g7) = 40
    c: Distance(g6,g-50) = 7
    c: Distance(g6,g-27) = 7
    c: Distance(g0,g-49) = 7
    c: Distance(g0,g-48) = 7
    c: Distance(g1,g-48) = 5
    c: Distance(g1,g-47) = 5
    c: Distance(g2,g-47) = 6
    c: Distance(g2,g-46) = 6
    c: Distance(g3,g-46) = 6
    c: Distance(g3,g-45) = 6
FEATURE [PartDesign::Pocket] Pocket011  label="Rubber Feet Pocket"
  BaseFeature = -> Pocket010
  Direction = (0,0,1)
  Length = 1
  Length2 = 5
  Profile = -> Sketch014
  ReferenceAxis = -> Sketch014 [N_Axis]
  Type = 0
FEATURE [PartDesign::Pocket] Pocket012
  BaseFeature = -> Pocket011
  Direction = (0,0,-1)
  Length = 0.2
  Length2 = 5
  Profile = -> Pocket011 [Face325,Face326,Face331,Face332,Face337,Face338,Face336,Face335,Face330,Face329,Face324,Face323,Face313,Face314,Face327,Face328,Face333,Face334,Face322,Face321,Face316,Face315,Face311,Face310,Face312,Face317,Face318,Face319,Face320]
  Refine = true
  Type = 0
FEATURE [Sketcher::SketchObject] Sketch015
  ExternalGeometry = -> [Pocket012]
  FullyConstrained = true
  MapMode = 5
  Placement = pos=(0,0,6.4) rot=(0,0,1;0rad)
  Support = -> [Pocket012]
  sketch-geometry (14):
    g0: LineSegment StartX=11.75 StartY=57.25 StartZ=0 EndX=13.25 EndY=57.25 EndZ=0
    g1: LineSegment StartX=55.5 StartY=32.625 StartZ=0 EndX=55.5 EndY=27 EndZ=0
    g2: ArcOfCircle CenterX=13.25 CenterY=53.25 CenterZ=0 NormalX=0 NormalY=0 NormalZ=1 AngleXU=0 Radius=4 StartAngle=0 EndAngle=1.5708
    g3: ArcOfCircle CenterX=51.875 CenterY=32.625 CenterZ=0 NormalX=0 NormalY=0 NormalZ=1 AngleXU=0 Radius=3.625 StartAngle=0 EndAngle=3.14159
    g4: LineSegment StartX=17.25 StartY=53.25 StartZ=0 EndX=17.25 EndY=29 EndZ=0
    g5: LineSegment StartX=15.75 StartY=53.25 StartZ=0 EndX=15.75 EndY=29 EndZ=0
    g6: LineSegment StartX=15.75 StartY=29 StartZ=0 EndX=17.25 EndY=29 EndZ=0
    g7: LineSegment StartX=48.25 StartY=32.625 StartZ=0 EndX=48.25 EndY=29 EndZ=0
    g8: LineSegment StartX=11.75 StartY=57.25 StartZ=0 EndX=11.75 EndY=55.75 EndZ=0
    g9: LineSegment StartX=11.75 StartY=55.75 StartZ=0 EndX=15.75 EndY=53.25 EndZ=0
    g10: LineSegment StartX=48.25 StartY=29 StartZ=0 EndX=51.5 EndY=29 EndZ=0
    g11: LineSegment StartX=51.5 StartY=29 StartZ=0 EndX=51.5 EndY=27 EndZ=0
    g12: LineSegment StartX=51.5 StartY=27 StartZ=0 EndX=55.5 EndY=27 EndZ=0
    g13: LineSegment StartX=48.25 StartY=29 StartZ=0 EndX=51.875 EndY=32.625 EndZ=0
  constraints (36):
    c: Coincident(g0,g-4)
    c: Horizontal(g0)
    c: Coincident(g1,g-6)
    c: Vertical(g1)
    c: Tangent(g0,g2) = 1.5708
    c: Tangent(g1,g3) = 1.5708
    c: Radius(g2) = 4
    c: Tangent(g4,g2) = 1.5708
    c: Vertical(g4)
    c: Coincident(g5,g-3)
    c: Coincident(g5,g-5)
    c: Horizontal(g3,g3)
    c: DistanceX(g0,g0) = 1.5
    c: Coincident(g6,g5)
    c: Coincident(g6,g4)
    c: Horizontal(g6)
    c: Coincident(g7,g3)
    c: PointOnObject(g7,g-5)
    c: Vertical(g7)
    c: Coincident(g8,g0)
    c: Vertical(g8)
    c: Coincident(g9,g8)
    c: Coincident(g9,g5)
    c: Coincident(g10,g7)
    c: Vertical(g11)
    c: Coincident(g12,g11)
    c: Coincident(g12,g1)
    c: Horizontal(g12)
    c: DistanceY(g8,g8) = 1.5
    c: DistanceX(g12,g12) = 4
    c: Coincident(g10,g11)
    c: Horizontal(g10)
    c: DistanceX(g7,g1) = 7.25
    c: Coincident(g13,g7)
    c: Coincident(g13,g3)
    c: Angle(g10,g13) = 0.785398
FEATURE [PartDesign::Pad] Pad005
  BaseFeature = -> Pocket012
  Direction = (0,0,1)
  Length = 6.4
  Length2 = 10
  Profile = -> Sketch015
  ReferenceAxis = -> Sketch015 [N_Axis]
  Refine = true
  Reversed = true
  Type = 0
FEATURE [Sketcher::SketchObject] Sketch016
  ExternalGeometry = -> [Pad005]
  FullyConstrained = true
  MapMode = 5
  Placement = pos=(0,0,0) rot=(1,0,0;3.14159rad)
  Support = -> [Pad005]
  sketch-geometry (6):
    g0: LineSegment StartX=17.25 StartY=-53.1118 StartZ=0 EndX=48.25 EndY=-31.8192 EndZ=0
    g1: LineSegment StartX=53.6098 StartY=-35.8079 StartZ=0 EndX=15.1643 EndY=-56.7622 EndZ=0
    g2: LineSegment StartX=17.25 StartY=-53.25 StartZ=0 EndX=17.25 EndY=-53.1118 EndZ=0
    g3: LineSegment StartX=48.25 StartY=-32.625 StartZ=0 EndX=48.25 EndY=-31.8192 EndZ=0
    g4: ArcOfCircle CenterX=51.875 CenterY=-32.625 CenterZ=0 NormalX=0 NormalY=0 NormalZ=1 AngleXU=0 Radius=3.625 StartAngle=3.14159 EndAngle=5.21141
    g5: ArcOfCircle CenterX=13.25 CenterY=-53.25 CenterZ=0 NormalX=0 NormalY=0 NormalZ=1 AngleXU=0 Radius=4 StartAngle=5.21141 EndAngle=6.28319
  constraints (14):
    c: Coincident(g0,g-5)
    c: Coincident(g0,g-5)
    c: Tangent(g1,g-4) = 1.5708
    c: Tangent(g1,g-3) = 1.5708
    c: Coincident(g2,g-3)
    c: Coincident(g2,g0)
    c: Coincident(g3,g-4)
    c: Coincident(g3,g0)
    c: Coincident(g4,g-4)
    c: Coincident(g4,g3)
    c: Coincident(g4,g1)
    c: Coincident(g5,g-3)
    c: Coincident(g5,g2)
    c: Coincident(g5,g1)
FEATURE [PartDesign::Pad] Pad006
  BaseFeature = -> Pad005
  Direction = (0,0,-1)
  Length = 4
  Length2 = 10
  Profile = -> Sketch016
  ReferenceAxis = -> Sketch016 [N_Axis]
  Refine = true
  Reversed = true
  Type = 0
FEATURE [PartDesign::SubtractivePipe] SubtractivePipe001
  AuxilleryCurvelinear = true
  AuxillerySpineTangent = false
  BaseFeature = -> Pad006
  Binormal = (0,0,0)
  Mode = 0
  Profile = -> Pad006 [Face101]
  Spine = -> Pad006 [Edge117,Edge105,Edge335,Edge110,Edge114]
  SpineTangent = false
  Transformation = 0
  Transition = 0
FEATURE [PartDesign::Plane] DatumPlane001
  Length = 202.365
  MapMode = 7
  Placement = pos=(53.6098,35.8079,4) rot=(0.765769,0.454752,0.454752;1.83456rad)
  ResizeMode = 0
  Support = -> [SubtractivePipe001]
  Width = 69.1428
FEATURE [Sketcher::SketchObject] Sketch017
  FullyConstrained = true
  MapMode = 5
  Placement = pos=(53.6098,35.8079,4) rot=(0.765769,0.454752,0.454752;1.83456rad)
  Support = -> [DatumPlane001]
  sketch-geometry (3):
    g0: LineSegment StartX=0 StartY=-1 StartZ=0 EndX=-1 EndY=0 EndZ=0
    g1: LineSegment StartX=-1 StartY=0 StartZ=0 EndX=0 EndY=0 EndZ=0
    g2: LineSegment StartX=0 StartY=0 StartZ=0 EndX=0 EndY=-1 EndZ=0
  constraints (8):
    c: Coincident(g1,g0)
    c: Coincident(g1,g-1)
    c: Coincident(g2,g1)
    c: Coincident(g2,g0)
    c: Vertical(g2)
    c: Horizontal(g1)
    c: DistanceX(g1,g1) = 1
    c: DistanceY(g2,g2) = 1
FEATURE [PartDesign::SubtractivePipe] SubtractivePipe002
  AuxilleryCurvelinear = true
  AuxillerySpineTangent = false
  BaseFeature = -> SubtractivePipe001
  Binormal = (0,0,0)
  Mode = 0
  Profile = -> Sketch017
  Spine = -> SubtractivePipe001 [Edge10]
  SpineTangent = false
  Transformation = 0
  Transition = 0
FEATURE [PartDesign::Pad] Pad007
  BaseFeature = -> SubtractivePipe002
  Direction = (1e-16,1e-16,-1)
  Length = 1
  Length2 = 10
  Profile = -> SubtractivePipe002 [Face105,Face103]
  Refine = true
  Type = 0
FEATURE [Sketcher::SketchObject] Sketch018
  ExternalGeometry = -> [Pad007]
  FullyConstrained = true
  MapMode = 5
  Placement = pos=(0,0,6.4) rot=(0,0,1;0rad)
  Support = -> [Pad007]
  sketch-geometry (2):
    g0: Circle CenterX=51.875 CenterY=32.625 CenterZ=0 NormalX=0 NormalY=0 NormalZ=1 AngleXU=0 Radius=1.4
    g1: Circle CenterX=14.4 CenterY=32.625 CenterZ=0 NormalX=0 NormalY=0 NormalZ=1 AngleXU=0 Radius=1.4
  constraints (6):
    c: Coincident(g0,g-3)
    c: DistanceX(g-5,g-5) = 2.8
    c: Diameter(g0) = 2.8
    c: Diameter(g1) = 2.8
    c: Horizontal(g1,g0)
    c: Tangent(g1,g-4)
FEATURE [PartDesign::Pocket] Pocket013
  BaseFeature = -> Pad007
  Direction = (0,0,-1)
  Length = 3.25
  Length2 = 5
  Profile = -> Sketch018
  ReferenceAxis = -> Sketch018 [N_Axis]
  Type = 0
FEATURE [Sketcher::SketchObject] Sketch019
  ExternalGeometry = -> [Pocket013]
  FullyConstrained = true
  MapMode = 5
  Placement = pos=(0,0,6.4) rot=(0,0,1;0rad)
  Support = -> [Pocket013]
  sketch-geometry (4):
    g0: LineSegment StartX=12.4 StartY=34.025 StartZ=0 EndX=14.4 EndY=34.025 EndZ=0
    g1: LineSegment StartX=14.4 StartY=34.025 StartZ=0 EndX=14.4 EndY=31.225 EndZ=0
    g2: LineSegment StartX=14.4 StartY=31.225 StartZ=0 EndX=12.4 EndY=31.225 EndZ=0
    g3: LineSegment StartX=12.4 StartY=31.225 StartZ=0 EndX=12.4 EndY=34.025 EndZ=0
  constraints (11):
    c: Coincident(g0,g1)
    c: Coincident(g1,g2)
    c: Coincident(g2,g3)
    c: Coincident(g3,g0)
    c: Horizontal(g0)
    c: Horizontal(g2)
    c: Vertical(g1)
    c: Vertical(g3)
    c: DistanceY(g3,g3) = 2.8
    c: DistanceX(g0,g0) = 2
    c: Symmetric(g0,g1,g-4)
FEATURE [PartDesign::Pocket] Pocket014
  BaseFeature = -> Pocket013
  Direction = (0,0,-1)
  Length = 2.4
  Length2 = 5
  Profile = -> Sketch019
  ReferenceAxis = -> Sketch019 [N_Axis]
  Refine = true
  Type = 0
FEATURE [PartDesign::Fillet] Fillet008
  Base = -> Pocket014 [Edge411,Edge402]
  BaseFeature = -> Pocket014
  Radius = 1
  SupportTransform = false
  UseAllEdges = false
FEATURE [Sketcher::SketchObject] Sketch020
  ExternalGeometry = -> [Fillet008]
  FullyConstrained = true
  MapMode = 5
  Placement = pos=(0,0,0) rot=(1,0,0;3.14159rad)
  Support = -> [Fillet008]
  sketch-geometry (14):
    g0: LineSegment StartX=12.9278 StartY=-35.175 StartZ=0 EndX=15.8722 EndY=-35.175 EndZ=0
    g1: LineSegment StartX=15.8722 StartY=-35.175 StartZ=0 EndX=17.3445 EndY=-32.625 EndZ=0
    g2: LineSegment StartX=17.3445 StartY=-32.625 StartZ=0 EndX=15.8722 EndY=-30.075 EndZ=0
    g3: LineSegment StartX=15.8722 StartY=-30.075 StartZ=0 EndX=12.9278 EndY=-30.075 EndZ=0
    g4: LineSegment StartX=12.9278 StartY=-30.075 StartZ=0 EndX=11.4555 EndY=-32.625 EndZ=0
    g5: LineSegment StartX=11.4555 StartY=-32.625 StartZ=0 EndX=12.9278 EndY=-35.175 EndZ=0
    g6: Circle CenterX=14.4 CenterY=-32.625 CenterZ=0 NormalX=0 NormalY=0 NormalZ=1 AngleXU=0 Radius=2.94449
    g7: LineSegment StartX=53.3472 StartY=-35.175 StartZ=0 EndX=54.8195 EndY=-32.625 EndZ=0
    g8: LineSegment StartX=54.8195 StartY=-32.625 StartZ=0 EndX=53.3472 EndY=-30.075 EndZ=0
    g9: LineSegment StartX=53.3472 StartY=-30.075 StartZ=0 EndX=50.4028 EndY=-30.075 EndZ=0
    g10: LineSegment StartX=50.4028 StartY=-30.075 StartZ=0 EndX=48.9305 EndY=-32.625 EndZ=0
    g11: LineSegment StartX=48.9305 StartY=-32.625 StartZ=0 EndX=50.4028 EndY=-35.175 EndZ=0
    g12: LineSegment StartX=50.4028 StartY=-35.175 StartZ=0 EndX=53.3472 EndY=-35.175 EndZ=0
    g13: Circle CenterX=51.875 CenterY=-32.625 CenterZ=0 NormalX=0 NormalY=0 NormalZ=1 AngleXU=0 Radius=2.94449
  constraints (33):
    c: Coincident(g0,g1)
    c: Coincident(g1,g2)
    c: Coincident(g2,g3)
    c: Coincident(g3,g4)
    c: Coincident(g4,g5)
    c: Coincident(g5,g0)
    c: Equal(g0, g1-g5) x5
    c: PointOnObject(g0,g6)
    c: PointOnObject(g1,g6)
    c: PointOnObject(g2,g6)
    c: PointOnObject(g3,g6)
    c: PointOnObject(g4,g6)
    c: PointOnObject(g5,g6)
    c: Coincident(g6,g-4)
    c: Coincident(g7,g8)
    c: Coincident(g8,g9)
    c: Coincident(g9,g10)
    c: Coincident(g10,g11)
    c: Coincident(g11,g12)
    c: Coincident(g12,g7)
    c: Equal(g7, g8-g12) x5
    c: PointOnObject(g7,g13)
    c: PointOnObject(g8,g13)
    c: PointOnObject(g9,g13)
    c: PointOnObject(g10,g13)
    c: PointOnObject(g11,g13)
    c: PointOnObject(g12,g13)
    c: Coincident(g13,g-3)
    c: Horizontal(g0)
    c: DistanceY(g-6,g-5) = 5.1
    c: DistanceY(g0,g2) = 5.1
    c: Horizontal(g9)
    c: DistanceY(g11,g9) = 5.1
FEATURE [PartDesign::Pocket] Pocket015
  BaseFeature = -> Fillet008
  Direction = (0,0,1)
  Length = 3
  Length2 = 5
  Profile = -> Sketch020
  ReferenceAxis = -> Sketch020 [N_Axis]
  Type = 0
FEATURE [Sketcher::SketchObject] Sketch021
  ExternalGeometry = -> [Pocket015]
  FullyConstrained = true
  MapMode = 5
  Placement = pos=(0,0,0) rot=(1,0,0;3.14159rad)
  Support = -> [Pocket015]
  sketch-geometry (8):
    g0: LineSegment StartX=50.4028 StartY=-35.175 StartZ=0 EndX=53.3472 EndY=-35.175 EndZ=0
    g1: LineSegment StartX=53.3472 StartY=-35.175 StartZ=0 EndX=54.8195 EndY=-32.625 EndZ=0
    g2: LineSegment StartX=54.8195 StartY=-32.625 StartZ=0 EndX=53.3472 EndY=-30.075 EndZ=0
    g3: LineSegment StartX=53.3472 StartY=-30.075 StartZ=0 EndX=50.4028 EndY=-30.075 EndZ=0
    g4: LineSegment StartX=50.4028 StartY=-30.075 StartZ=0 EndX=48.9305 EndY=-32.625 EndZ=0
    g5: LineSegment StartX=48.9305 StartY=-32.625 StartZ=0 EndX=50.4028 EndY=-35.175 EndZ=0
    g6: Circle CenterX=51.875 CenterY=-32.625 CenterZ=0 NormalX=0 NormalY=0 NormalZ=1 AngleXU=0 Radius=2.94449
    g7: Circle CenterX=51.875 CenterY=-32.625 CenterZ=0 NormalX=0 NormalY=0 NormalZ=1 AngleXU=0 Radius=3.625
  constraints (18):
    c: Coincident(g0,g1)
    c: Coincident(g1,g2)
    c: Coincident(g2,g3)
    c: Coincident(g3,g4)
    c: Coincident(g4,g5)
    c: Coincident(g5,g0)
    c: Equal(g0, g1-g5) x5
    c: PointOnObject(g0,g6)
    c: PointOnObject(g1,g6)
    c: PointOnObject(g2,g6)
    c: PointOnObject(g3,g6)
    c: PointOnObject(g4,g6)
    c: PointOnObject(g5,g6)
    c: Coincident(g6,g-3)
    c: Horizontal(g0)
    c: DistanceY(g0,g3) = 5.1
    c: Coincident(g7,g6)
    c: Diameter(g7) = 7.25
FEATURE [PartDesign::Pad] Pad008
  BaseFeature = -> Pocket015
  Direction = (0,0,-1)
  Length = 1
  Length2 = 10
  Profile = -> Sketch021
  ReferenceAxis = -> Sketch021 [N_Axis]
  Refine = true
  Reversed = true
  Type = 0
FEATURE [Sketcher::SketchObject] Sketch022
  ExternalGeometry = -> [Pad008]
  FullyConstrained = true
  MapMode = 5
  Placement = pos=(0,0,-1.53e-14) rot=(1,0,0;3.14159rad)
  Support = -> [Pad008]
  sketch-geometry (8):
    g0: Circle CenterX=-107.25 CenterY=-36.921 CenterZ=0 NormalX=0 NormalY=0 NormalZ=1 AngleXU=0 Radius=3.25
    g1: Circle CenterX=-71.706 CenterY=-50.25 CenterZ=0 NormalX=0 NormalY=0 NormalZ=1 AngleXU=0 Radius=3.25
    g2: Circle CenterX=11.1293 CenterY=-51.25 CenterZ=0 NormalX=0 NormalY=0 NormalZ=1 AngleXU=0 Radius=3.25
    g3: Circle CenterX=47.5 CenterY=-23.8421 CenterZ=0 NormalX=0 NormalY=0 NormalZ=1 AngleXU=0 Radius=4.25
    g4: Circle CenterX=46.8331 CenterY=28.1 CenterZ=0 NormalX=0 NormalY=0 NormalZ=1 AngleXU=0 Radius=4.25
    g5: Circle CenterX=42.2449 CenterY=51.25 CenterZ=0 NormalX=0 NormalY=0 NormalZ=1 AngleXU=0 Radius=3.25
    g6: Circle CenterX=-66.25 CenterY=49.25 CenterZ=0 NormalX=0 NormalY=0 NormalZ=1 AngleXU=0 Radius=4.25
    g7: Circle CenterX=-106.25 CenterY=49.25 CenterZ=0 NormalX=0 NormalY=0 NormalZ=1 AngleXU=0 Radius=4.25
  constraints (16):
    c: Coincident(g0,g-5)
    c: Coincident(g1,g-4)
    c: Coincident(g2,g-3)
    c: Coincident(g3,g-10)
    c: Coincident(g4,g-8)
    c: Coincident(g5,g-9)
    c: Coincident(g6,g-7)
    c: Coincident(g7,g-6)
    c: Equal(g7,g6)
    c: Equal(g7,g4)
    c: Equal(g7,g3)
    c: Diameter(g7) = 8.5
    c: Equal(g0,g1)
    c: Equal(g0,g2)
    c: Equal(g0,g5)
    c: Diameter(g0) = 6.5
FEATURE [PartDesign::Pad] Pad009
  BaseFeature = -> Pad008
  Direction = (-2e-16,5e-16,-1)
  Length = 1
  Length2 = 10
  Profile = -> Sketch022
  ReferenceAxis = -> Sketch022 [N_Axis]
  Refine = true
  Reversed = true
  Type = 0
FEATURE [Sketcher::SketchObject] Sketch024
  FullyConstrained = true
  MapMode = 5
  Placement = pos=(0,0,-1.53e-14) rot=(1,0,0;3.14159rad)
  Support = -> [Pad009]
  sketch-geometry (4):
    g0: LineSegment StartX=-119.825 StartY=60.9905 StartZ=0 EndX=60.8165 EndY=60.9905 EndZ=0
    g1: LineSegment StartX=60.8165 StartY=60.9905 StartZ=0 EndX=60.8165 EndY=-61.8741 EndZ=0
    g2: LineSegment StartX=60.8165 StartY=-61.8741 StartZ=0 EndX=-119.825 EndY=-61.8741 EndZ=0
    g3: LineSegment StartX=-119.825 StartY=-61.8741 StartZ=0 EndX=-119.825 EndY=60.9905 EndZ=0
  constraints (12):
    c: Coincident(g0,g1)
    c: Coincident(g1,g2)
    c: Coincident(g2,g3)
    c: Coincident(g3,g0)
    c: Horizontal(g0)
    c: Horizontal(g2)
    c: Vertical(g1)
    c: Vertical(g3)
    c: DistanceX(g0) = 60.8165
    c: DistanceY(g0) = 60.9905
    c: DistanceX(g2) = -119.825
    c: DistanceY(g2) = -61.8741
FEATURE [PartDesign::Pocket] Pocket016
  BaseFeature = -> Pad009
  Direction = (2e-16,-5e-16,1)
  Length = 0.3
  Length2 = 5
  Profile = -> Sketch024
  ReferenceAxis = -> Sketch024 [N_Axis]
  Type = 0
FEATURE [Sketcher::SketchObject] Sketch025
  ExternalGeometry = -> [Pocket016]
  FullyConstrained = true
  MapMode = 5
  Placement = pos=(0,0,6.4) rot=(0,0,1;0rad)
  Support = -> [Pocket016]
  sketch-geometry (25):
    g0: LineSegment StartX=41.5 StartY=-37.75 StartZ=0 EndX=47.9 EndY=-37.75 EndZ=0
    g1: LineSegment StartX=47.9 StartY=-37.75 StartZ=0 EndX=47.9 EndY=-47.75 EndZ=0
    g2: LineSegment StartX=47.9 StartY=-47.75 StartZ=0 EndX=41.5 EndY=-47.75 EndZ=0
    g3: LineSegment StartX=41.5 StartY=-47.75 StartZ=0 EndX=41.5 EndY=-37.75 EndZ=0
    g4: GeomPoint X=41.5 Y=-42.75 Z=0
    g5: LineSegment StartX=-100 StartY=36.75 StartZ=0 EndX=-90 EndY=36.75 EndZ=0
    g6: LineSegment StartX=-90 StartY=36.75 StartZ=0 EndX=-90 EndY=43.15 EndZ=0
    g7: LineSegment StartX=-90 StartY=43.15 StartZ=0 EndX=-100 EndY=43.15 EndZ=0
    g8: LineSegment StartX=-100 StartY=43.15 StartZ=0 EndX=-100 EndY=36.75 EndZ=0
    g9: LineSegment StartX=-95 StartY=36.75 StartZ=0 EndX=-95 EndY=30.75 EndZ=0
    g10: LineSegment StartX=-100 StartY=-46.25 StartZ=0 EndX=-90 EndY=-46.25 EndZ=0
    g11: LineSegment StartX=-90 StartY=-46.25 StartZ=0 EndX=-90 EndY=-52.65 EndZ=0
    g12: LineSegment StartX=-90 StartY=-52.65 StartZ=0 EndX=-100 EndY=-52.65 EndZ=0
    g13: LineSegment StartX=-100 StartY=-52.65 StartZ=0 EndX=-100 EndY=-46.25 EndZ=0
    g14: LineSegment StartX=-81 StartY=43.15 StartZ=0 EndX=-71 EndY=43.15 EndZ=0
    g15: LineSegment StartX=-71 StartY=43.15 StartZ=0 EndX=-71 EndY=36.75 EndZ=0
    g16: LineSegment StartX=-71 StartY=36.75 StartZ=0 EndX=-81 EndY=36.75 EndZ=0
    g17: LineSegment StartX=-81 StartY=36.75 StartZ=0 EndX=-81 EndY=43.15 EndZ=0
    g18: LineSegment StartX=-95 StartY=-46.25 StartZ=0 EndX=-95 EndY=-40.25 EndZ=0
    g19: LineSegment StartX=-76 StartY=36.75 StartZ=0 EndX=-76 EndY=30.75 EndZ=0
    g20: LineSegment StartX=-81 StartY=-46.25 StartZ=0 EndX=-71 EndY=-46.25 EndZ=0
    g21: LineSegment StartX=-71 StartY=-46.25 StartZ=0 EndX=-71 EndY=-52.65 EndZ=0
    g22: LineSegment StartX=-71 StartY=-52.65 StartZ=0 EndX=-81 EndY=-52.65 EndZ=0
    g23: LineSegment StartX=-81 StartY=-52.65 StartZ=0 EndX=-81 EndY=-46.25 EndZ=0
    g24: LineSegment StartX=-76 StartY=-46.25 StartZ=0 EndX=-76 EndY=-40.25 EndZ=0
  constraints (68):
    c: Coincident(g0,g1)
    c: Coincident(g1,g2)
    c: Coincident(g2,g3)
    c: Coincident(g3,g0)
    c: Horizontal(g0)
    c: Horizontal(g2)
    c: Vertical(g1)
    c: Vertical(g3)
    c: DistanceX(g0,g0) = 6.4
    c: DistanceY(g3,g3) = 10
    c: Symmetric(g0,g2,g4)
    c: Symmetric(g-3,g-3,g4)
    c: Coincident(g5,g6)
    c: Coincident(g6,g7)
    c: Coincident(g7,g8)
    c: Coincident(g8,g5)
    c: Horizontal(g5)
    c: Horizontal(g7)
    c: Vertical(g6)
    c: Vertical(g8)
    c: DistanceY(g8,g8) = 6.4
    c: DistanceX(g7,g7) = 10
    c: Vertical(g9)
    c: Symmetric(g5,g5,g9)
    c: Symmetric(g-4,g-4,g9)
    c: PointOnObject(g5,g-5)
    c: Coincident(g10,g11)
    c: Coincident(g11,g12)
    c: Coincident(g12,g13)
    c: Coincident(g13,g10)
    c: Horizontal(g10)
    c: Horizontal(g12)
    c: Vertical(g11)
    c: Vertical(g13)
    c: Coincident(g14,g15)
    c: Coincident(g15,g16)
    c: Coincident(g16,g17)
    c: Coincident(g17,g14)
    c: Horizontal(g14)
    c: Horizontal(g16)
    c: Vertical(g15)
    c: Vertical(g17)
    c: DistanceY(g17,g17) = 6.4
    c: DistanceX(g14,g14) = 10
    c: DistanceX(g10,g10) = 10
    c: DistanceY(g13,g13) = 6.4
    c: PointOnObject(g16,g-9)
    c: PointOnObject(g10,g-7)
    c: Vertical(g18)
    c: Vertical(g19)
    c: Symmetric(g-8,g-8,g19)
    c: Symmetric(g16,g15,g19)
    c: Coincident(g20,g21)
    c: Coincident(g21,g22)
    c: Coincident(g22,g23)
    c: Coincident(g23,g20)
    c: Horizontal(g20)
    c: Horizontal(g22)
    c: Vertical(g21)
    c: Vertical(g23)
    c: DistanceX(g20,g20) = 10
    c: DistanceY(g23,g23) = 6.4
    c: Vertical(g24)
    c: PointOnObject(g20,g-10)
    c: Symmetric(g10,g10,g18)
    c: Symmetric(g-6,g-6,g18)
    c: Symmetric(g-11,g-11,g24)
    c: Symmetric(g20,g20,g24)
FEATURE [PartDesign::Pocket] Pocket017
  BaseFeature = -> Pocket016
  Direction = (0,0,-1)
  Length = 5.6
  Length2 = 5
  Profile = -> Sketch025
  ReferenceAxis = -> Sketch025 [N_Axis]
  Type = 0
FEATURE [Sketcher::SketchObject] Sketch026
  ExternalGeometry = -> [Pocket017]
  FullyConstrained = false
  MapMode = 5
  Placement = pos=(0,0,6.4) rot=(0,0,1;0rad)
  Support = -> [Pocket017]
  sketch-geometry (4):
    g0: LineSegment StartX=-71 StartY=43.15 StartZ=0 EndX=-70 EndY=43.15 EndZ=0
    g1: LineSegment StartX=-70 StartY=43.15 StartZ=0 EndX=-70 EndY=36.75 EndZ=0
    g2: LineSegment StartX=-70 StartY=36.75 StartZ=0 EndX=-71 EndY=36.75 EndZ=0
    g3: LineSegment StartX=-71 StartY=36.75 StartZ=0 EndX=-71 EndY=43.15 EndZ=0
  constraints (11):
    c: Coincident(g0,g1)
    c: Coincident(g1,g2)
    c: Coincident(g2,g3)
    c: Coincident(g3,g0)
    c: Horizontal(g0)
    c: Horizontal(g2)
    c: Vertical(g1)
    c: Vertical(g3)
    c: Coincident(g0,g-3)
    c: Horizontal(g2,g-5)
    c: PointOnObject(g-4,g1)
FEATURE [PartDesign::Pocket] Pocket018
  BaseFeature = -> Pocket017
  Direction = (0,0,-1)
  Length = 2.4
  Length2 = 5
  Profile = -> Sketch026
  ReferenceAxis = -> Sketch026 [N_Axis]
  Refine = true
  Type = 0
FEATURE [PartDesign::Chamfer] Chamfer001
  Angle = 30
  Base = -> Pocket018 [Edge503,Edge248,Edge281,Edge505,Edge509,Edge359,Edge507,Edge306]
  BaseFeature = -> Pocket018
  ChamferType = 2
  FlipDirection = false
  Size = 2.77
  Size2 = 1
  SupportTransform = false
  UseAllEdges = false
FEATURE [PartDesign::Chamfer] Chamfer002
  Angle = 30
  Base = -> Chamfer001 [Edge370,Edge507]
  BaseFeature = -> Chamfer001
  ChamferType = 2
  FlipDirection = false
  Size = 2.775
  Size2 = 1
  SupportTransform = false
  UseAllEdges = false
FEATURE [PartDesign::Fillet] Fillet009
  Base = -> Chamfer002 [Edge384,Edge374,Edge9,Edge5,Edge465,Edge455,Edge430,Edge420,Edge409,Edge399,Edge499,Edge484]
  BaseFeature = -> Chamfer002
  Radius = 1
  SupportTransform = false
  UseAllEdges = false
FEATURE [Sketcher::SketchObject] Sketch027
  ExternalGeometry = -> [Fillet009]
  FullyConstrained = false
  MapMode = 5
  Placement = pos=(0,0,6.4) rot=(0,0,1;0rad)
  Support = -> [Fillet009]
  sketch-geometry (15):
    g0: LineSegment StartX=-73.6545 StartY=56.9953 StartZ=0 EndX=-68.5753 EndY=58.9 EndZ=0
    g1: LineSegment StartX=-4.4761 StartY=51 StartZ=0 EndX=5.99984 EndY=51 EndZ=0
    g2: LineSegment StartX=5.99984 StartY=51 StartZ=0 EndX=5.99984 EndY=57.4 EndZ=0
    g3: LineSegment StartX=5.99984 StartY=57.4 StartZ=0 EndX=-4.4761 EndY=57.4 EndZ=0
    g4: LineSegment StartX=-4.4761 StartY=57.4 StartZ=0 EndX=-4.4761 EndY=51 EndZ=0
    g5: LineSegment StartX=-68.5753 StartY=58.9 StartZ=0 EndX=13.25 EndY=58.9 EndZ=0
    g6: LineSegment StartX=17.25 StartY=52.9 StartZ=0 EndX=17.25 EndY=54.9 EndZ=0
    g7: LineSegment StartX=17.25 StartY=52.9 StartZ=0 EndX=11.25 EndY=52.9 EndZ=0
    g8: LineSegment StartX=11.25 StartY=52.9 StartZ=0 EndX=11.25 EndY=56.25 EndZ=0
    g9: LineSegment StartX=11.25 StartY=56.25 StartZ=0 EndX=-66.9522 EndY=56.25 EndZ=0
    g10: LineSegment StartX=-73.6545 StartY=56.9953 StartZ=0 EndX=-72.9522 EndY=55.1227 EndZ=0
    g11: LineSegment StartX=-72.9522 StartY=55.1227 StartZ=0 EndX=-66.9522 EndY=55.1227 EndZ=0
    g12: LineSegment StartX=-66.9522 StartY=56.25 StartZ=0 EndX=-66.9522 EndY=55.1227 EndZ=0
    g13: ArcOfCircle CenterX=13.25 CenterY=54.9 CenterZ=0 NormalX=0 NormalY=0 NormalZ=1 AngleXU=0 Radius=4 StartAngle=1e-16 EndAngle=1.5708
    g14: GeomPoint X=17.25 Y=58.9 Z=0
  constraints (40):
    c: Coincident(g0,g-4)
    c: Parallel(g0,g-4)
    c: Coincident(g1,g2)
    c: Coincident(g2,g3)
    c: Coincident(g3,g4)
    c: Coincident(g4,g1)
    c: Horizontal(g1)
    c: Horizontal(g3)
    c: Vertical(g2)
    c: Vertical(g4)
    c: DistanceY(g4,g4) = 6.4
    c: PointOnObject(g1,g-8)
    c: Coincident(g5,g0)
    c: Horizontal(g5)
    c: Vertical(g6)
    c: DistanceY(g2,g14) = 1.5
    c: Coincident(g7,g6)
    c: Horizontal(g7)
    c: Coincident(g8,g7)
    c: Vertical(g8)
    c: Coincident(g9,g8)
    c: Horizontal(g9)
    c: Coincident(g10,g0)
    c: Perpendicular(g0,g10)
    c: Coincident(g11,g10)
    c: Horizontal(g11)
    c: Coincident(g12,g9)
    c: Coincident(g12,g11)
    c: Vertical(g12)
    c: Distance(g10) = 2
    c: DistanceY(g8,g-7) = 1
    c: DistanceY(g6,g14) = 6
    c: PointOnObject(g-7,g6)
    c: DistanceX(g7,g7) = 6
    c: DistanceX(g11,g11) = 6
    c: PointOnObject(g14,g5)
    c: PointOnObject(g14,g6)
    c: Tangent(g5,g13) = 1.5708
    c: Tangent(g6,g13) = -1.5708
    c: DistanceX(g13,g6) = 4
FEATURE [PartDesign::Pad] Pad010
  BaseFeature = -> Fillet009
  Direction = (0,0,1)
  Length = 6.1
  Length2 = 10
  Profile = -> Sketch027
  ReferenceAxis = -> Sketch027 [N_Axis]
  Reversed = true
  Type = 0
FEATURE [Sketcher::SketchObject] Sketch028
  ExternalGeometry = -> [Pad010]
  FullyConstrained = true
  MapMode = 5
  Placement = pos=(0,0,4) rot=(0,0,1;0rad)
  Support = -> [Pad010]
  sketch-geometry (5):
    g0: LineSegment StartX=15.2774 StartY=58.3481 StartZ=0 EndX=53.7123 EndY=35.7499 EndZ=0
    g1: ArcOfCircle CenterX=13.25 CenterY=54.9 CenterZ=0 NormalX=0 NormalY=0 NormalZ=1 AngleXU=0 Radius=4 StartAngle=0 EndAngle=1.03928
    g2: ArcOfCircle CenterX=51.875 CenterY=32.625 CenterZ=0 NormalX=0 NormalY=0 NormalZ=1 AngleXU=0 Radius=3.625 StartAngle=1.03928 EndAngle=3.14159
    g3: LineSegment StartX=17.25 StartY=54.9 StartZ=0 EndX=17.25 EndY=32.625 EndZ=0
    g4: LineSegment StartX=48.25 StartY=32.625 StartZ=0 EndX=17.25 EndY=32.625 EndZ=0
  constraints (13):
    c: Tangent(g0,g-3) = 1.5708
    c: Tangent(g0,g-4) = 1.5708
    c: Coincident(g1,g-3)
    c: Coincident(g1,g0)
    c: Coincident(g1,g-3)
    c: Coincident(g2,g0)
    c: Coincident(g2,g-4)
    c: Horizontal(g2,g2)
    c: Coincident(g3,g1)
    c: Vertical(g3)
    c: Coincident(g4,g2)
    c: Coincident(g4,g3)
    c: Horizontal(g4)
FEATURE [PartDesign::Pad] Pad011
  BaseFeature = -> Pad010
  Direction = (0,0,1)
  Length = 3.7
  Length2 = 10
  Profile = -> Sketch028
  ReferenceAxis = -> Sketch028 [N_Axis]
  Refine = true
  Reversed = true
  Type = 0
FEATURE [PartDesign::Fillet] Fillet010
  Base = -> Pad011 [Edge1]
  BaseFeature = -> Pad011
  Radius = 4
  SupportTransform = false
  UseAllEdges = false
FEATURE [Sketcher::SketchObject] Sketch029
  ExternalGeometry = -> [Fillet010]
  FullyConstrained = true
  MapMode = 5
  Placement = pos=(0,0,6.4) rot=(0,0,1;0rad)
  Support = -> [Fillet010]
  sketch-geometry (10):
    g0: LineSegment StartX=-24 StartY=51 StartZ=0 EndX=-14 EndY=51 EndZ=0
    g1: LineSegment StartX=-14 StartY=51 StartZ=0 EndX=-14 EndY=57.4 EndZ=0
    g2: LineSegment StartX=-14 StartY=57.4 StartZ=0 EndX=-24 EndY=57.4 EndZ=0
    g3: LineSegment StartX=-24 StartY=57.4 StartZ=0 EndX=-24 EndY=51 EndZ=0
    g4: LineSegment StartX=-5 StartY=51 StartZ=0 EndX=5 EndY=51 EndZ=0
    g5: LineSegment StartX=5 StartY=51 StartZ=0 EndX=5 EndY=57.4 EndZ=0
    g6: LineSegment StartX=5 StartY=57.4 StartZ=0 EndX=-5 EndY=57.4 EndZ=0
    g7: LineSegment StartX=-5 StartY=57.4 StartZ=0 EndX=-5 EndY=51 EndZ=0
    g8: LineSegment StartX=-19 StartY=51 StartZ=0 EndX=-19 EndY=45 EndZ=0
    g9: LineSegment StartX=3e-15 StartY=51 StartZ=0 EndX=3e-15 EndY=45 EndZ=0
  constraints (28):
    c: Coincident(g0,g1)
    c: Coincident(g1,g2)
    c: Coincident(g2,g3)
    c: Coincident(g3,g0)
    c: Horizontal(g0)
    c: Horizontal(g2)
    c: Vertical(g1)
    c: Vertical(g3)
    c: Coincident(g4,g5)
    c: Coincident(g5,g6)
    c: Coincident(g6,g7)
    c: Coincident(g7,g4)
    c: Horizontal(g4)
    c: Horizontal(g6)
    c: Vertical(g5)
    c: Vertical(g7)
    c: DistanceX(g2,g2) = 10
    c: DistanceX(g6,g6) = 10
    c: DistanceY(g3,g3) = 6.4
    c: DistanceY(g7,g7) = 6.4
    c: Vertical(g9)
    c: Vertical(g8)
    c: Symmetric(g-3,g-3,g8)
    c: Symmetric(g-4,g-4,g9)
    c: Symmetric(g4,g4,g9)
    c: Symmetric(g0,g0,g8)
    c: PointOnObject(g0,g-5)
    c: PointOnObject(g4,g-6)
FEATURE [PartDesign::Pocket] Pocket019
  BaseFeature = -> Fillet010
  Direction = (0,0,-1)
  Length = 5.6
  Length2 = 5
  Profile = -> Sketch029
  ReferenceAxis = -> Sketch029 [N_Axis]
  Type = 0
FEATURE [PartDesign::Chamfer] Chamfer003
  Angle = 30
  Base = -> Pocket019 [Edge547,Edge522,Edge974,Edge975]
  BaseFeature = -> Pocket019
  ChamferType = 2
  FlipDirection = false
  Size = 2.775
  Size2 = 1
  SupportTransform = false
  UseAllEdges = false
FEATURE [Sketcher::SketchObject] Sketch030
  ExternalGeometry = -> [Chamfer003]
  FullyConstrained = true
  MapMode = 5
  Placement = pos=(0,0,6.4) rot=(0,0,1;0rad)
  Support = -> [Chamfer003]
  sketch-geometry (4):
    g0: LineSegment StartX=-27.5 StartY=55.75 StartZ=0 EndX=-24 EndY=55.75 EndZ=0
    g1: LineSegment StartX=-24 StartY=55.75 StartZ=0 EndX=-24 EndY=51.0858 EndZ=0
    g2: LineSegment StartX=-24 StartY=51.0858 StartZ=0 EndX=-27.5 EndY=51.0858 EndZ=0
    g3: LineSegment StartX=-27.5 StartY=51.0858 StartZ=0 EndX=-27.5 EndY=55.75 EndZ=0
  constraints (10):
    c: Coincident(g0,g1)
    c: Coincident(g1,g2)
    c: Coincident(g2,g3)
    c: Coincident(g3,g0)
    c: Horizontal(g0)
    c: Horizontal(g2)
    c: Vertical(g1)
    c: Vertical(g3)
    c: Coincident(g0,g-3)
    c: Coincident(g1,g-4)
FEATURE [PartDesign::Pocket] Pocket020
  BaseFeature = -> Chamfer003
  Direction = (0,0,-1)
  Length = 2.4
  Length2 = 5
  Profile = -> Sketch030
  ReferenceAxis = -> Sketch030 [N_Axis]
  Refine = true
  Type = 0
FEATURE [PartDesign::Fillet] Fillet011
  Base = -> Pocket020 [Edge484,Edge156,Edge3,Edge495]
  BaseFeature = -> Pocket020
  Radius = 1
  SupportTransform = false
  UseAllEdges = false
FEATURE [Sketcher::SketchObject] Sketch031
  ExternalGeometry = -> [Fillet011]
  FullyConstrained = true
  MapMode = 5
  Placement = pos=(1e-16,-1e-16,0.3) rot=(1,0,0;3.14159rad)
  Support = -> [Fillet011]
  sketch-geometry (21):
    g0: LineSegment StartX=53.7123 StartY=-35.7499 StartZ=0 EndX=15.2774 EndY=-58.3481 EndZ=0
    g1: LineSegment StartX=13.25 StartY=-58.9 StartZ=0 EndX=-67.85 EndY=-58.9 EndZ=0
    g2: LineSegment StartX=-69.2545 StartY=-58.6453 StartZ=0 EndX=-111.654 EndY=-42.7453 EndZ=0
    g3: LineSegment StartX=-114.25 StartY=-39 StartZ=0 EndX=-114.25 EndY=53.25 EndZ=0
    g4: LineSegment StartX=-110.25 StartY=57.25 StartZ=0 EndX=43.75 EndY=57.25 EndZ=0
    g5: LineSegment StartX=47.5937 StartY=54.3574 StartZ=0 EndX=55.3437 EndY=27.4574 EndZ=0
    g6: LineSegment StartX=55.5 StartY=26.35 StartZ=0 EndX=55.5 EndY=-32.625 EndZ=0
    g7: ArcOfCircle CenterX=51.875 CenterY=-32.625 CenterZ=0 NormalX=0 NormalY=0 NormalZ=1 AngleXU=0 Radius=3.625 StartAngle=5.24391 EndAngle=6.28319
    g8: GeomPoint X=55.5 Y=-34.6988 Z=0
    g9: ArcOfCircle CenterX=13.25 CenterY=-54.9 CenterZ=0 NormalX=0 NormalY=0 NormalZ=1 AngleXU=0 Radius=4 StartAngle=4.71239 EndAngle=5.24391
    g10: GeomPoint X=14.3388 Y=-58.9 Z=0
    g11: ArcOfCircle CenterX=-67.85 CenterY=-54.9 CenterZ=0 NormalX=0 NormalY=0 NormalZ=1 AngleXU=0 Radius=4 StartAngle=4.35362 EndAngle=4.71239
    g12: GeomPoint X=-68.5753 Y=-58.9 Z=0
    g13: ArcOfCircle CenterX=-110.25 CenterY=-39 CenterZ=0 NormalX=0 NormalY=0 NormalZ=1 AngleXU=0 Radius=4 StartAngle=3.14159 EndAngle=4.35362
    g14: GeomPoint X=-114.25 Y=-41.772 Z=0
    g15: ArcOfCircle CenterX=-110.25 CenterY=53.25 CenterZ=0 NormalX=0 NormalY=0 NormalZ=1 AngleXU=0 Radius=4 StartAngle=1.5708 EndAngle=3.14159
    g16: GeomPoint X=-114.25 Y=57.25 Z=0
    g17: ArcOfCircle CenterX=43.75 CenterY=53.25 CenterZ=0 NormalX=0 NormalY=0 NormalZ=1 AngleXU=0 Radius=4 StartAngle=0.280508 EndAngle=1.5708
    g18: GeomPoint X=46.7603 Y=57.25 Z=0
    g19: ArcOfCircle CenterX=51.5 CenterY=26.35 CenterZ=0 NormalX=0 NormalY=0 NormalZ=1 AngleXU=0 Radius=4 StartAngle=-9e-16 EndAngle=0.280508
    g20: GeomPoint X=55.5 Y=26.9147 Z=0
  constraints (42):
    c: Tangent(g0,g-4)
    c: Tangent(g5,g-9)
    c: Tangent(g2,g-6)
    c: Tangent(g3,g-7)
    c: Tangent(g4,g-8)
    c: Tangent(g6,g-3)
    c: Tangent(g1,g-5)
    c: PointOnObject(g8,g0)
    c: PointOnObject(g8,g6)
    c: Tangent(g0,g7) = 1.5708
    c: Tangent(g6,g7) = 1.5708
    c: PointOnObject(g10,g0)
    c: PointOnObject(g10,g1)
    c: Tangent(g0,g9) = 1.5708
    c: Tangent(g1,g9) = 1.5708
    c: PointOnObject(g12,g1)
    c: PointOnObject(g12,g2)
    c: Tangent(g1,g11) = 1.5708
    c: Tangent(g2,g11) = 1.5708
    c: PointOnObject(g14,g2)
    c: PointOnObject(g14,g3)
    c: Tangent(g2,g13) = 1.5708
    c: Tangent(g3,g13) = 1.5708
    c: PointOnObject(g16,g3)
    c: PointOnObject(g16,g4)
    c: Tangent(g3,g15) = 1.5708
    c: Tangent(g4,g15) = 1.5708
    c: PointOnObject(g18,g4)
    c: PointOnObject(g18,g5)
    c: Tangent(g4,g17) = 1.5708
    c: Tangent(g5,g17) = 1.5708
    c: PointOnObject(g20,g5)
    c: PointOnObject(g20,g6)
    c: Tangent(g5,g19) = 1.5708
    c: Tangent(g6,g19) = 1.5708
    c: Diameter(g7) = 7.25
    c: Diameter(g9) = 8
    c: Diameter(g11) = 8
    c: Diameter(g13) = 8
    c: Diameter(g15) = 8
    c: Diameter(g17) = 8
    c: Diameter(g19) = 8
FEATURE [Sketcher::SketchObject] Sketch032
  ExternalGeometry = -> [Fillet011]
  FullyConstrained = true
  MapMode = 5
  Placement = pos=(-45.8356,-17.1884,0) rot=(0.714195,-0.494937,-0.494937;1.90121rad)
  Support = -> [Fillet011]
  sketch-geometry (3):
    g0: LineSegment StartX=-79.2282 StartY=0.3 StartZ=0 EndX=-79.2282 EndY=1.3 EndZ=0
    g1: LineSegment StartX=-79.2282 StartY=0.3 StartZ=0 EndX=-78.2282 EndY=0.3 EndZ=0
    g2: LineSegment StartX=-79.2282 StartY=1.3 StartZ=0 EndX=-78.2282 EndY=0.3 EndZ=0
  constraints (8):
    c: Coincident(g0,g-3)
    c: Coincident(g1,g0)
    c: Coincident(g2,g0)
    c: Coincident(g2,g1)
    c: DistanceX(g1,g1) = 1
    c: DistanceY(g0,g0) = 1
    c: Horizontal(g1)
    c: Vertical(g0)
FEATURE [PartDesign::SubtractivePipe] SubtractivePipe003
  AuxilleryCurvelinear = true
  AuxillerySpineTangent = false
  BaseFeature = -> Fillet011
  Binormal = (0,0,0)
  Mode = 0
  Profile = -> Sketch032
  Spine = -> Sketch031
  SpineTangent = false
  Transformation = 0
  Transition = 0
FEATURE [Sketcher::SketchObject] Sketch033
  ExternalGeometry = -> [SubtractivePipe003]
  FullyConstrained = true
  MapMode = 5
  Placement = pos=(1e-16,-1e-16,0.3) rot=(1,0,0;3.14159rad)
  Support = -> [SubtractivePipe003]
  sketch-geometry (8):
    g0: LineSegment StartX=50.4028 StartY=-35.175 StartZ=0 EndX=53.3472 EndY=-35.175 EndZ=0
    g1: LineSegment StartX=53.3472 StartY=-35.175 StartZ=0 EndX=54.8195 EndY=-32.625 EndZ=0
    g2: LineSegment StartX=54.8195 StartY=-32.625 StartZ=0 EndX=53.3472 EndY=-30.075 EndZ=0
    g3: LineSegment StartX=53.3472 StartY=-30.075 StartZ=0 EndX=50.4028 EndY=-30.075 EndZ=0
    g4: LineSegment StartX=50.4028 StartY=-30.075 StartZ=0 EndX=48.9305 EndY=-32.625 EndZ=0
    g5: LineSegment StartX=48.9305 StartY=-32.625 StartZ=0 EndX=50.4028 EndY=-35.175 EndZ=0
    g6: Circle CenterX=51.875 CenterY=-32.625 CenterZ=0 NormalX=0 NormalY=0 NormalZ=1 AngleXU=0 Radius=2.94449
    g7: Circle CenterX=51.875 CenterY=-32.625 CenterZ=0 NormalX=0 NormalY=0 NormalZ=1 AngleXU=0 Radius=3.625
  constraints (18):
    c: Coincident(g0,g1)
    c: Coincident(g1,g2)
    c: Coincident(g2,g3)
    c: Coincident(g3,g4)
    c: Coincident(g4,g5)
    c: Coincident(g5,g0)
    c: Equal(g0, g1-g5) x5
    c: PointOnObject(g0,g6)
    c: PointOnObject(g1,g6)
    c: PointOnObject(g2,g6)
    c: PointOnObject(g3,g6)
    c: PointOnObject(g4,g6)
    c: PointOnObject(g5,g6)
    c: Coincident(g6,g-3)
    c: Horizontal(g0)
    c: DistanceY(g0,g2) = 5.1
    c: Coincident(g7,g6)
    c: Diameter(g7) = 7.25
FEATURE [PartDesign::Pad] Pad012
  BaseFeature = -> SubtractivePipe003
  Direction = (-2e-16,4e-16,-1)
  Length = 1
  Length2 = 10
  Profile = -> Sketch033
  ReferenceAxis = -> Sketch033 [N_Axis]
  Refine = true
  Reversed = true
  Type = 0
FEATURE [PartDesign::Plane] DatumPlane002
  Length = 205.458
  MapMode = 7
  Placement = pos=(15.2774,58.3481,4) rot=(-0.375002,0.655505,0.655505;3.85914rad)
  ResizeMode = 0
  Support = -> [Pad012]
  Width = 69.2957
FEATURE [Sketcher::SketchObject] Sketch034
  FullyConstrained = true
  MapMode = 5
  Placement = pos=(15.2774,58.3481,4) rot=(-0.375002,0.655505,0.655505;3.85914rad)
  Support = -> [DatumPlane002]
  sketch-geometry (3):
    g0: LineSegment StartX=0 StartY=0 StartZ=0 EndX=0 EndY=-1 EndZ=0
    g1: LineSegment StartX=0 StartY=0 StartZ=0 EndX=1 EndY=0 EndZ=0
    g2: LineSegment StartX=0 StartY=-1 StartZ=0 EndX=1 EndY=-1e-16 EndZ=0
  constraints (8):
    c: Coincident(g0,g-1)
    c: Coincident(g1,g0)
    c: Coincident(g2,g0)
    c: Coincident(g2,g1)
    c: Vertical(g0)
    c: Horizontal(g1)
    c: DistanceX(g1,g1) = 1
    c: DistanceY(g0,g0) = 1
FEATURE [PartDesign::SubtractivePipe] SubtractivePipe004
  AuxilleryCurvelinear = true
  AuxillerySpineTangent = false
  BaseFeature = -> Pad012
  Binormal = (0,0,0)
  Mode = 0
  Profile = -> Sketch034
  Spine = -> Pad012 [Edge876]
  SpineTangent = false
  Transformation = 0
  Transition = 0
FEATURE [PartDesign::Pad] Pad013
  BaseFeature = -> SubtractivePipe004
  Direction = (-1e-16,-1e-16,-1)
  Length = 1
  Length2 = 10
  Profile = -> SubtractivePipe004 [Face255,Face264]
  Refine = true
  Type = 0
FEATURE [PartDesign::Body] Body
  Group = -> [Sketch,Pad,Sketch001,Pocket,Sketch002,Pocket001,Sketch003,Pocket002,Sketch004,Pocket003,Pocket004,Pad001,Sketch005,Pocket005,Fillet,Fillet002,Sketch006,Pad002,Sketch007,Pocket006,Fillet003,Fillet004,Fillet005,Fillet006,Fillet007,Sketch008,Pocket007,Sketch009,Pocket008,Sketch010,Pocket009,Chamfer,DatumPlane,Sketch011,SubtractivePipe,Pad003,Sketch012,Pad004,Sketch013,Pocket010,Sketch014,Pocket011,+50 more]
  Origin = -> Origin
  Tip = -> Pad013
